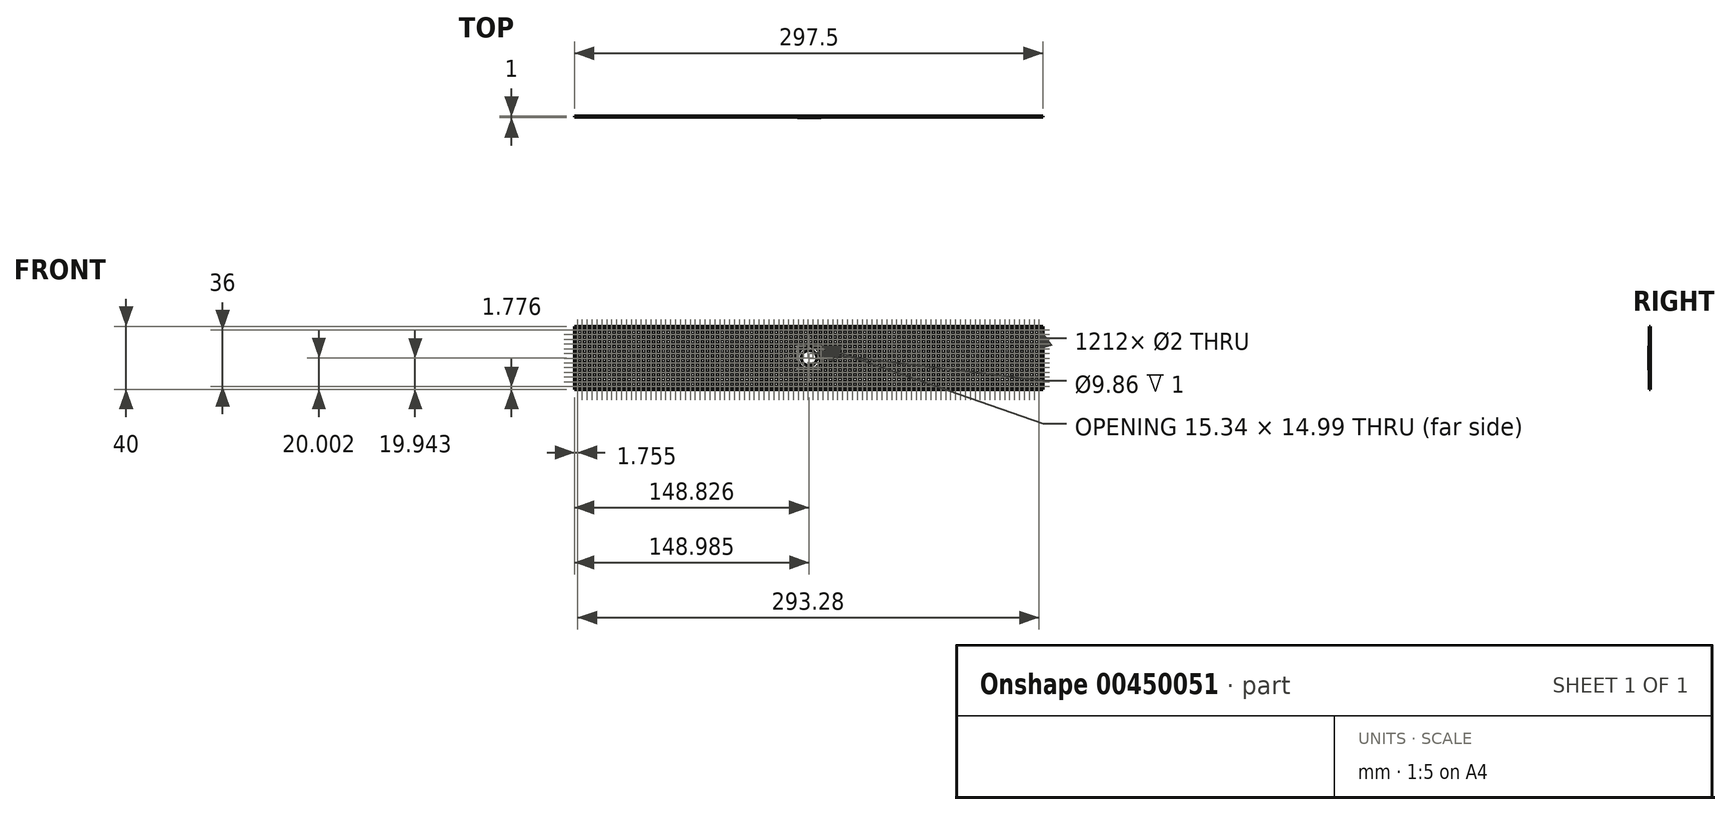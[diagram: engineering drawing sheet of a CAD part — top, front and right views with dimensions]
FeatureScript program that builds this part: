
annotation { "Feature Type Name" : "Feature", "Feature Type Description" : "" }
export const myFeature = defineFeature(function(context is Context, id is Id, definition is map)
    precondition{}
    {
        {
            var Q0;
            Q0=qCreatedBy(makeId("Front.planeOp"),FACE);
            var sketch = newSketch(context, id + "F0", { "sketchPlane" : qUnion([Q0])});
            skLineSegment(sketch, "E0.bottom", {"start": v(-95.63, 31.24) * mm, "end": v(201.87, 31.24) * mm});
            skLineSegment(sketch, "E0.top", {"start": v(-95.63, -8.76) * mm, "end": v(201.87, -8.76) * mm});
            skLineSegment(sketch, "E0.left", {"start": v(-95.63, 31.24) * mm, "end": v(-95.63, -8.76) * mm});
            skLineSegment(sketch, "E0.right", {"start": v(201.87, 31.24) * mm, "end": v(201.87, -8.76) * mm});
            skCircle(sketch, "E1", {"center": v(-93.87, -6.98) * mm, "radius": 1 * mm});
            skCircle(sketch, "E2.0.1.0", {"center": v(-93.87, -3.98) * mm, "radius": 1 * mm});
            skCircle(sketch, "E2.0.2.0", {"center": v(-93.87, -0.98) * mm, "radius": 1 * mm});
            skCircle(sketch, "E2.0.3.0", {"center": v(-93.87, 2.02) * mm, "radius": 1 * mm});
            skCircle(sketch, "E2.0.4.0", {"center": v(-93.87, 5.02) * mm, "radius": 1 * mm});
            skCircle(sketch, "E2.0.5.0", {"center": v(-93.87, 8.02) * mm, "radius": 1 * mm});
            skCircle(sketch, "E2.0.6.0", {"center": v(-93.87, 11.02) * mm, "radius": 1 * mm});
            skCircle(sketch, "E2.0.7.0", {"center": v(-93.87, 14.02) * mm, "radius": 1 * mm});
            skCircle(sketch, "E2.0.8.0", {"center": v(-93.87, 17.02) * mm, "radius": 1 * mm});
            skCircle(sketch, "E2.0.9.0", {"center": v(-93.87, 20.02) * mm, "radius": 1 * mm});
            skCircle(sketch, "E2.0.10.0", {"center": v(-93.87, 23.02) * mm, "radius": 1 * mm});
            skCircle(sketch, "E2.0.11.0", {"center": v(-93.87, 26.02) * mm, "radius": 1 * mm});
            skCircle(sketch, "E2.1.0.0", {"center": v(-90.75, -6.98) * mm, "radius": 1 * mm});
            skCircle(sketch, "E2.1.1.0", {"center": v(-90.75, -3.98) * mm, "radius": 1 * mm});
            skCircle(sketch, "E2.1.2.0", {"center": v(-90.75, -0.98) * mm, "radius": 1 * mm});
            skCircle(sketch, "E2.1.3.0", {"center": v(-90.75, 2.02) * mm, "radius": 1 * mm});
            skCircle(sketch, "E2.1.4.0", {"center": v(-90.75, 5.02) * mm, "radius": 1 * mm});
            skCircle(sketch, "E2.1.5.0", {"center": v(-90.75, 8.02) * mm, "radius": 1 * mm});
            skCircle(sketch, "E2.1.6.0", {"center": v(-90.75, 11.02) * mm, "radius": 1 * mm});
            skCircle(sketch, "E2.1.7.0", {"center": v(-90.75, 14.02) * mm, "radius": 1 * mm});
            skCircle(sketch, "E2.1.8.0", {"center": v(-90.75, 17.02) * mm, "radius": 1 * mm});
            skCircle(sketch, "E2.1.9.0", {"center": v(-90.75, 20.02) * mm, "radius": 1 * mm});
            skCircle(sketch, "E2.1.10.0", {"center": v(-90.75, 23.02) * mm, "radius": 1 * mm});
            skCircle(sketch, "E2.1.11.0", {"center": v(-90.75, 26.02) * mm, "radius": 1 * mm});
            skCircle(sketch, "E2.2.0.0", {"center": v(-87.63, -6.98) * mm, "radius": 1 * mm});
            skCircle(sketch, "E2.2.1.0", {"center": v(-87.63, -3.98) * mm, "radius": 1 * mm});
            skCircle(sketch, "E2.2.2.0", {"center": v(-87.63, -0.98) * mm, "radius": 1 * mm});
            skCircle(sketch, "E2.2.3.0", {"center": v(-87.63, 2.02) * mm, "radius": 1 * mm});
            skCircle(sketch, "E2.2.4.0", {"center": v(-87.63, 5.02) * mm, "radius": 1 * mm});
            skCircle(sketch, "E2.2.5.0", {"center": v(-87.63, 8.02) * mm, "radius": 1 * mm});
            skCircle(sketch, "E2.2.6.0", {"center": v(-87.63, 11.02) * mm, "radius": 1 * mm});
            skCircle(sketch, "E2.2.7.0", {"center": v(-87.63, 14.02) * mm, "radius": 1 * mm});
            skCircle(sketch, "E2.2.8.0", {"center": v(-87.63, 17.02) * mm, "radius": 1 * mm});
            skCircle(sketch, "E2.2.9.0", {"center": v(-87.63, 20.02) * mm, "radius": 1 * mm});
            skCircle(sketch, "E2.2.10.0", {"center": v(-87.63, 23.02) * mm, "radius": 1 * mm});
            skCircle(sketch, "E2.2.11.0", {"center": v(-87.63, 26.02) * mm, "radius": 1 * mm});
            skCircle(sketch, "E2.3.0.0", {"center": v(-84.51, -6.98) * mm, "radius": 1 * mm});
            skCircle(sketch, "E2.3.1.0", {"center": v(-84.51, -3.98) * mm, "radius": 1 * mm});
            skCircle(sketch, "E2.3.2.0", {"center": v(-84.51, -0.98) * mm, "radius": 1 * mm});
            skCircle(sketch, "E2.3.3.0", {"center": v(-84.51, 2.02) * mm, "radius": 1 * mm});
            skCircle(sketch, "E2.3.4.0", {"center": v(-84.51, 5.02) * mm, "radius": 1 * mm});
            skCircle(sketch, "E2.3.5.0", {"center": v(-84.51, 8.02) * mm, "radius": 1 * mm});
            skCircle(sketch, "E2.3.6.0", {"center": v(-84.51, 11.02) * mm, "radius": 1 * mm});
            skCircle(sketch, "E2.3.7.0", {"center": v(-84.51, 14.02) * mm, "radius": 1 * mm});
            skCircle(sketch, "E2.3.8.0", {"center": v(-84.51, 17.02) * mm, "radius": 1 * mm});
            skCircle(sketch, "E2.3.9.0", {"center": v(-84.51, 20.02) * mm, "radius": 1 * mm});
            skCircle(sketch, "E2.3.10.0", {"center": v(-84.51, 23.02) * mm, "radius": 1 * mm});
            skCircle(sketch, "E2.3.11.0", {"center": v(-84.51, 26.02) * mm, "radius": 1 * mm});
            skCircle(sketch, "E2.4.0.0", {"center": v(-81.4, -6.98) * mm, "radius": 1 * mm});
            skCircle(sketch, "E2.4.1.0", {"center": v(-81.4, -3.98) * mm, "radius": 1 * mm});
            skCircle(sketch, "E2.4.2.0", {"center": v(-81.4, -0.98) * mm, "radius": 1 * mm});
            skCircle(sketch, "E2.4.3.0", {"center": v(-81.4, 2.02) * mm, "radius": 1 * mm});
            skCircle(sketch, "E2.4.4.0", {"center": v(-81.4, 5.02) * mm, "radius": 1 * mm});
            skCircle(sketch, "E2.4.5.0", {"center": v(-81.4, 8.02) * mm, "radius": 1 * mm});
            skCircle(sketch, "E2.4.6.0", {"center": v(-81.4, 11.02) * mm, "radius": 1 * mm});
            skCircle(sketch, "E2.4.7.0", {"center": v(-81.4, 14.02) * mm, "radius": 1 * mm});
            skCircle(sketch, "E2.4.8.0", {"center": v(-81.4, 17.02) * mm, "radius": 1 * mm});
            skCircle(sketch, "E2.4.9.0", {"center": v(-81.4, 20.02) * mm, "radius": 1 * mm});
            skCircle(sketch, "E2.4.10.0", {"center": v(-81.4, 23.02) * mm, "radius": 1 * mm});
            skCircle(sketch, "E2.4.11.0", {"center": v(-81.4, 26.02) * mm, "radius": 1 * mm});
            skCircle(sketch, "E2.5.0.0", {"center": v(-78.27, -6.98) * mm, "radius": 1 * mm});
            skCircle(sketch, "E2.5.1.0", {"center": v(-78.27, -3.98) * mm, "radius": 1 * mm});
            skCircle(sketch, "E2.5.2.0", {"center": v(-78.27, -0.98) * mm, "radius": 1 * mm});
            skCircle(sketch, "E2.5.3.0", {"center": v(-78.27, 2.02) * mm, "radius": 1 * mm});
            skCircle(sketch, "E2.5.4.0", {"center": v(-78.27, 5.02) * mm, "radius": 1 * mm});
            skCircle(sketch, "E2.5.5.0", {"center": v(-78.27, 8.02) * mm, "radius": 1 * mm});
            skCircle(sketch, "E2.5.6.0", {"center": v(-78.27, 11.02) * mm, "radius": 1 * mm});
            skCircle(sketch, "E2.5.7.0", {"center": v(-78.27, 14.02) * mm, "radius": 1 * mm});
            skCircle(sketch, "E2.5.8.0", {"center": v(-78.27, 17.02) * mm, "radius": 1 * mm});
            skCircle(sketch, "E2.5.9.0", {"center": v(-78.27, 20.02) * mm, "radius": 1 * mm});
            skCircle(sketch, "E2.5.10.0", {"center": v(-78.27, 23.02) * mm, "radius": 1 * mm});
            skCircle(sketch, "E2.5.11.0", {"center": v(-78.27, 26.02) * mm, "radius": 1 * mm});
            skCircle(sketch, "E2.6.0.0", {"center": v(-75.15, -6.98) * mm, "radius": 1 * mm});
            skCircle(sketch, "E2.6.1.0", {"center": v(-75.15, -3.98) * mm, "radius": 1 * mm});
            skCircle(sketch, "E2.6.2.0", {"center": v(-75.15, -0.98) * mm, "radius": 1 * mm});
            skCircle(sketch, "E2.6.3.0", {"center": v(-75.15, 2.02) * mm, "radius": 1 * mm});
            skCircle(sketch, "E2.6.4.0", {"center": v(-75.15, 5.02) * mm, "radius": 1 * mm});
            skCircle(sketch, "E2.6.5.0", {"center": v(-75.15, 8.02) * mm, "radius": 1 * mm});
            skCircle(sketch, "E2.6.6.0", {"center": v(-75.15, 11.02) * mm, "radius": 1 * mm});
            skCircle(sketch, "E2.6.7.0", {"center": v(-75.15, 14.02) * mm, "radius": 1 * mm});
            skCircle(sketch, "E2.6.8.0", {"center": v(-75.15, 17.02) * mm, "radius": 1 * mm});
            skCircle(sketch, "E2.6.9.0", {"center": v(-75.15, 20.02) * mm, "radius": 1 * mm});
            skCircle(sketch, "E2.6.10.0", {"center": v(-75.15, 23.02) * mm, "radius": 1 * mm});
            skCircle(sketch, "E2.6.11.0", {"center": v(-75.15, 26.02) * mm, "radius": 1 * mm});
            skCircle(sketch, "E2.7.0.0", {"center": v(-72.03, -6.98) * mm, "radius": 1 * mm});
            skCircle(sketch, "E2.7.1.0", {"center": v(-72.03, -3.98) * mm, "radius": 1 * mm});
            skCircle(sketch, "E2.7.2.0", {"center": v(-72.03, -0.98) * mm, "radius": 1 * mm});
            skCircle(sketch, "E2.7.3.0", {"center": v(-72.03, 2.02) * mm, "radius": 1 * mm});
            skCircle(sketch, "E2.7.4.0", {"center": v(-72.03, 5.02) * mm, "radius": 1 * mm});
            skCircle(sketch, "E2.7.5.0", {"center": v(-72.03, 8.02) * mm, "radius": 1 * mm});
            skCircle(sketch, "E2.7.6.0", {"center": v(-72.03, 11.02) * mm, "radius": 1 * mm});
            skCircle(sketch, "E2.7.7.0", {"center": v(-72.03, 14.02) * mm, "radius": 1 * mm});
            skCircle(sketch, "E2.7.8.0", {"center": v(-72.03, 17.02) * mm, "radius": 1 * mm});
            skCircle(sketch, "E2.7.9.0", {"center": v(-72.03, 20.02) * mm, "radius": 1 * mm});
            skCircle(sketch, "E2.7.10.0", {"center": v(-72.03, 23.02) * mm, "radius": 1 * mm});
            skCircle(sketch, "E2.7.11.0", {"center": v(-72.03, 26.02) * mm, "radius": 1 * mm});
            skCircle(sketch, "E2.8.0.0", {"center": v(-68.91, -6.98) * mm, "radius": 1 * mm});
            skCircle(sketch, "E2.8.1.0", {"center": v(-68.91, -3.98) * mm, "radius": 1 * mm});
            skCircle(sketch, "E2.8.2.0", {"center": v(-68.91, -0.98) * mm, "radius": 1 * mm});
            skCircle(sketch, "E2.8.3.0", {"center": v(-68.91, 2.02) * mm, "radius": 1 * mm});
            skCircle(sketch, "E2.8.4.0", {"center": v(-68.91, 5.02) * mm, "radius": 1 * mm});
            skCircle(sketch, "E2.8.5.0", {"center": v(-68.91, 8.02) * mm, "radius": 1 * mm});
            skCircle(sketch, "E2.8.6.0", {"center": v(-68.91, 11.02) * mm, "radius": 1 * mm});
            skCircle(sketch, "E2.8.7.0", {"center": v(-68.91, 14.02) * mm, "radius": 1 * mm});
            skCircle(sketch, "E2.8.8.0", {"center": v(-68.91, 17.02) * mm, "radius": 1 * mm});
            skCircle(sketch, "E2.8.9.0", {"center": v(-68.91, 20.02) * mm, "radius": 1 * mm});
            skCircle(sketch, "E2.8.10.0", {"center": v(-68.91, 23.02) * mm, "radius": 1 * mm});
            skCircle(sketch, "E2.8.11.0", {"center": v(-68.91, 26.02) * mm, "radius": 1 * mm});
            skCircle(sketch, "E2.9.0.0", {"center": v(-65.8, -6.98) * mm, "radius": 1 * mm});
            skCircle(sketch, "E2.9.1.0", {"center": v(-65.8, -3.98) * mm, "radius": 1 * mm});
            skCircle(sketch, "E2.9.2.0", {"center": v(-65.8, -0.98) * mm, "radius": 1 * mm});
            skCircle(sketch, "E2.9.3.0", {"center": v(-65.8, 2.02) * mm, "radius": 1 * mm});
            skCircle(sketch, "E2.9.4.0", {"center": v(-65.8, 5.02) * mm, "radius": 1 * mm});
            skCircle(sketch, "E2.9.5.0", {"center": v(-65.8, 8.02) * mm, "radius": 1 * mm});
            skCircle(sketch, "E2.9.6.0", {"center": v(-65.8, 11.02) * mm, "radius": 1 * mm});
            skCircle(sketch, "E2.9.7.0", {"center": v(-65.8, 14.02) * mm, "radius": 1 * mm});
            skCircle(sketch, "E2.9.8.0", {"center": v(-65.8, 17.02) * mm, "radius": 1 * mm});
            skCircle(sketch, "E2.9.9.0", {"center": v(-65.8, 20.02) * mm, "radius": 1 * mm});
            skCircle(sketch, "E2.9.10.0", {"center": v(-65.8, 23.02) * mm, "radius": 1 * mm});
            skCircle(sketch, "E2.9.11.0", {"center": v(-65.8, 26.02) * mm, "radius": 1 * mm});
            skCircle(sketch, "E2.10.0.0", {"center": v(-62.67, -6.98) * mm, "radius": 1 * mm});
            skCircle(sketch, "E2.10.1.0", {"center": v(-62.67, -3.98) * mm, "radius": 1 * mm});
            skCircle(sketch, "E2.10.2.0", {"center": v(-62.67, -0.98) * mm, "radius": 1 * mm});
            skCircle(sketch, "E2.10.3.0", {"center": v(-62.67, 2.02) * mm, "radius": 1 * mm});
            skCircle(sketch, "E2.10.4.0", {"center": v(-62.67, 5.02) * mm, "radius": 1 * mm});
            skCircle(sketch, "E2.10.5.0", {"center": v(-62.67, 8.02) * mm, "radius": 1 * mm});
            skCircle(sketch, "E2.10.6.0", {"center": v(-62.67, 11.02) * mm, "radius": 1 * mm});
            skCircle(sketch, "E2.10.7.0", {"center": v(-62.67, 14.02) * mm, "radius": 1 * mm});
            skCircle(sketch, "E2.10.8.0", {"center": v(-62.67, 17.02) * mm, "radius": 1 * mm});
            skCircle(sketch, "E2.10.9.0", {"center": v(-62.67, 20.02) * mm, "radius": 1 * mm});
            skCircle(sketch, "E2.10.10.0", {"center": v(-62.67, 23.02) * mm, "radius": 1 * mm});
            skCircle(sketch, "E2.10.11.0", {"center": v(-62.67, 26.02) * mm, "radius": 1 * mm});
            skCircle(sketch, "E2.11.0.0", {"center": v(-59.55, -6.98) * mm, "radius": 1 * mm});
            skCircle(sketch, "E2.11.1.0", {"center": v(-59.55, -3.98) * mm, "radius": 1 * mm});
            skCircle(sketch, "E2.11.2.0", {"center": v(-59.55, -0.98) * mm, "radius": 1 * mm});
            skCircle(sketch, "E2.11.3.0", {"center": v(-59.55, 2.02) * mm, "radius": 1 * mm});
            skCircle(sketch, "E2.11.4.0", {"center": v(-59.55, 5.02) * mm, "radius": 1 * mm});
            skCircle(sketch, "E2.11.5.0", {"center": v(-59.55, 8.02) * mm, "radius": 1 * mm});
            skCircle(sketch, "E2.11.6.0", {"center": v(-59.55, 11.02) * mm, "radius": 1 * mm});
            skCircle(sketch, "E2.11.7.0", {"center": v(-59.55, 14.02) * mm, "radius": 1 * mm});
            skCircle(sketch, "E2.11.8.0", {"center": v(-59.55, 17.02) * mm, "radius": 1 * mm});
            skCircle(sketch, "E2.11.9.0", {"center": v(-59.55, 20.02) * mm, "radius": 1 * mm});
            skCircle(sketch, "E2.11.10.0", {"center": v(-59.55, 23.02) * mm, "radius": 1 * mm});
            skCircle(sketch, "E2.11.11.0", {"center": v(-59.55, 26.02) * mm, "radius": 1 * mm});
            skCircle(sketch, "E2.12.0.0", {"center": v(-56.43, -6.98) * mm, "radius": 1 * mm});
            skCircle(sketch, "E2.12.1.0", {"center": v(-56.43, -3.98) * mm, "radius": 1 * mm});
            skCircle(sketch, "E2.12.2.0", {"center": v(-56.43, -0.98) * mm, "radius": 1 * mm});
            skCircle(sketch, "E2.12.3.0", {"center": v(-56.43, 2.02) * mm, "radius": 1 * mm});
            skCircle(sketch, "E2.12.4.0", {"center": v(-56.43, 5.02) * mm, "radius": 1 * mm});
            skCircle(sketch, "E2.12.5.0", {"center": v(-56.43, 8.02) * mm, "radius": 1 * mm});
            skCircle(sketch, "E2.12.6.0", {"center": v(-56.43, 11.02) * mm, "radius": 1 * mm});
            skCircle(sketch, "E2.12.7.0", {"center": v(-56.43, 14.02) * mm, "radius": 1 * mm});
            skCircle(sketch, "E2.12.8.0", {"center": v(-56.43, 17.02) * mm, "radius": 1 * mm});
            skCircle(sketch, "E2.12.9.0", {"center": v(-56.43, 20.02) * mm, "radius": 1 * mm});
            skCircle(sketch, "E2.12.10.0", {"center": v(-56.43, 23.02) * mm, "radius": 1 * mm});
            skCircle(sketch, "E2.12.11.0", {"center": v(-56.43, 26.02) * mm, "radius": 1 * mm});
            skCircle(sketch, "E2.13.0.0", {"center": v(-53.31, -6.98) * mm, "radius": 1 * mm});
            skCircle(sketch, "E2.13.1.0", {"center": v(-53.31, -3.98) * mm, "radius": 1 * mm});
            skCircle(sketch, "E2.13.2.0", {"center": v(-53.31, -0.98) * mm, "radius": 1 * mm});
            skCircle(sketch, "E2.13.3.0", {"center": v(-53.31, 2.02) * mm, "radius": 1 * mm});
            skCircle(sketch, "E2.13.4.0", {"center": v(-53.31, 5.02) * mm, "radius": 1 * mm});
            skCircle(sketch, "E2.13.5.0", {"center": v(-53.31, 8.02) * mm, "radius": 1 * mm});
            skCircle(sketch, "E2.13.6.0", {"center": v(-53.31, 11.02) * mm, "radius": 1 * mm});
            skCircle(sketch, "E2.13.7.0", {"center": v(-53.31, 14.02) * mm, "radius": 1 * mm});
            skCircle(sketch, "E2.13.8.0", {"center": v(-53.31, 17.02) * mm, "radius": 1 * mm});
            skCircle(sketch, "E2.13.9.0", {"center": v(-53.31, 20.02) * mm, "radius": 1 * mm});
            skCircle(sketch, "E2.13.10.0", {"center": v(-53.31, 23.02) * mm, "radius": 1 * mm});
            skCircle(sketch, "E2.13.11.0", {"center": v(-53.31, 26.02) * mm, "radius": 1 * mm});
            skCircle(sketch, "E2.14.0.0", {"center": v(-50.2, -6.98) * mm, "radius": 1 * mm});
            skCircle(sketch, "E2.14.1.0", {"center": v(-50.2, -3.98) * mm, "radius": 1 * mm});
            skCircle(sketch, "E2.14.2.0", {"center": v(-50.2, -0.98) * mm, "radius": 1 * mm});
            skCircle(sketch, "E2.14.3.0", {"center": v(-50.2, 2.02) * mm, "radius": 1 * mm});
            skCircle(sketch, "E2.14.4.0", {"center": v(-50.2, 5.02) * mm, "radius": 1 * mm});
            skCircle(sketch, "E2.14.5.0", {"center": v(-50.2, 8.02) * mm, "radius": 1 * mm});
            skCircle(sketch, "E2.14.6.0", {"center": v(-50.2, 11.02) * mm, "radius": 1 * mm});
            skCircle(sketch, "E2.14.7.0", {"center": v(-50.2, 14.02) * mm, "radius": 1 * mm});
            skCircle(sketch, "E2.14.8.0", {"center": v(-50.2, 17.02) * mm, "radius": 1 * mm});
            skCircle(sketch, "E2.14.9.0", {"center": v(-50.2, 20.02) * mm, "radius": 1 * mm});
            skCircle(sketch, "E2.14.10.0", {"center": v(-50.2, 23.02) * mm, "radius": 1 * mm});
            skCircle(sketch, "E2.14.11.0", {"center": v(-50.2, 26.02) * mm, "radius": 1 * mm});
            skCircle(sketch, "E2.15.0.0", {"center": v(-47.07, -6.98) * mm, "radius": 1 * mm});
            skCircle(sketch, "E2.15.1.0", {"center": v(-47.07, -3.98) * mm, "radius": 1 * mm});
            skCircle(sketch, "E2.15.2.0", {"center": v(-47.07, -0.98) * mm, "radius": 1 * mm});
            skCircle(sketch, "E2.15.3.0", {"center": v(-47.07, 2.02) * mm, "radius": 1 * mm});
            skCircle(sketch, "E2.15.4.0", {"center": v(-47.07, 5.02) * mm, "radius": 1 * mm});
            skCircle(sketch, "E2.15.5.0", {"center": v(-47.07, 8.02) * mm, "radius": 1 * mm});
            skCircle(sketch, "E2.15.6.0", {"center": v(-47.07, 11.02) * mm, "radius": 1 * mm});
            skCircle(sketch, "E2.15.7.0", {"center": v(-47.07, 14.02) * mm, "radius": 1 * mm});
            skCircle(sketch, "E2.15.8.0", {"center": v(-47.07, 17.02) * mm, "radius": 1 * mm});
            skCircle(sketch, "E2.15.9.0", {"center": v(-47.07, 20.02) * mm, "radius": 1 * mm});
            skCircle(sketch, "E2.15.10.0", {"center": v(-47.07, 23.02) * mm, "radius": 1 * mm});
            skCircle(sketch, "E2.15.11.0", {"center": v(-47.07, 26.02) * mm, "radius": 1 * mm});
            skCircle(sketch, "E2.16.0.0", {"center": v(-43.95, -6.98) * mm, "radius": 1 * mm});
            skCircle(sketch, "E2.16.1.0", {"center": v(-43.95, -3.98) * mm, "radius": 1 * mm});
            skCircle(sketch, "E2.16.2.0", {"center": v(-43.95, -0.98) * mm, "radius": 1 * mm});
            skCircle(sketch, "E2.16.3.0", {"center": v(-43.95, 2.02) * mm, "radius": 1 * mm});
            skCircle(sketch, "E2.16.4.0", {"center": v(-43.95, 5.02) * mm, "radius": 1 * mm});
            skCircle(sketch, "E2.16.5.0", {"center": v(-43.95, 8.02) * mm, "radius": 1 * mm});
            skCircle(sketch, "E2.16.6.0", {"center": v(-43.95, 11.02) * mm, "radius": 1 * mm});
            skCircle(sketch, "E2.16.7.0", {"center": v(-43.95, 14.02) * mm, "radius": 1 * mm});
            skCircle(sketch, "E2.16.8.0", {"center": v(-43.95, 17.02) * mm, "radius": 1 * mm});
            skCircle(sketch, "E2.16.9.0", {"center": v(-43.95, 20.02) * mm, "radius": 1 * mm});
            skCircle(sketch, "E2.16.10.0", {"center": v(-43.95, 23.02) * mm, "radius": 1 * mm});
            skCircle(sketch, "E2.16.11.0", {"center": v(-43.95, 26.02) * mm, "radius": 1 * mm});
            skCircle(sketch, "E2.17.0.0", {"center": v(-40.83, -6.98) * mm, "radius": 1 * mm});
            skCircle(sketch, "E2.17.1.0", {"center": v(-40.83, -3.98) * mm, "radius": 1 * mm});
            skCircle(sketch, "E2.17.2.0", {"center": v(-40.83, -0.98) * mm, "radius": 1 * mm});
            skCircle(sketch, "E2.17.3.0", {"center": v(-40.83, 2.02) * mm, "radius": 1 * mm});
            skCircle(sketch, "E2.17.4.0", {"center": v(-40.83, 5.02) * mm, "radius": 1 * mm});
            skCircle(sketch, "E2.17.5.0", {"center": v(-40.83, 8.02) * mm, "radius": 1 * mm});
            skCircle(sketch, "E2.17.6.0", {"center": v(-40.83, 11.02) * mm, "radius": 1 * mm});
            skCircle(sketch, "E2.17.7.0", {"center": v(-40.83, 14.02) * mm, "radius": 1 * mm});
            skCircle(sketch, "E2.17.8.0", {"center": v(-40.83, 17.02) * mm, "radius": 1 * mm});
            skCircle(sketch, "E2.17.9.0", {"center": v(-40.83, 20.02) * mm, "radius": 1 * mm});
            skCircle(sketch, "E2.17.10.0", {"center": v(-40.83, 23.02) * mm, "radius": 1 * mm});
            skCircle(sketch, "E2.17.11.0", {"center": v(-40.83, 26.02) * mm, "radius": 1 * mm});
            skCircle(sketch, "E2.18.0.0", {"center": v(-37.71, -6.98) * mm, "radius": 1 * mm});
            skCircle(sketch, "E2.18.1.0", {"center": v(-37.71, -3.98) * mm, "radius": 1 * mm});
            skCircle(sketch, "E2.18.2.0", {"center": v(-37.71, -0.98) * mm, "radius": 1 * mm});
            skCircle(sketch, "E2.18.3.0", {"center": v(-37.71, 2.02) * mm, "radius": 1 * mm});
            skCircle(sketch, "E2.18.4.0", {"center": v(-37.71, 5.02) * mm, "radius": 1 * mm});
            skCircle(sketch, "E2.18.5.0", {"center": v(-37.71, 8.02) * mm, "radius": 1 * mm});
            skCircle(sketch, "E2.18.6.0", {"center": v(-37.71, 11.02) * mm, "radius": 1 * mm});
            skCircle(sketch, "E2.18.7.0", {"center": v(-37.71, 14.02) * mm, "radius": 1 * mm});
            skCircle(sketch, "E2.18.8.0", {"center": v(-37.71, 17.02) * mm, "radius": 1 * mm});
            skCircle(sketch, "E2.18.9.0", {"center": v(-37.71, 20.02) * mm, "radius": 1 * mm});
            skCircle(sketch, "E2.18.10.0", {"center": v(-37.71, 23.02) * mm, "radius": 1 * mm});
            skCircle(sketch, "E2.18.11.0", {"center": v(-37.71, 26.02) * mm, "radius": 1 * mm});
            skCircle(sketch, "E2.19.0.0", {"center": v(-34.6, -6.98) * mm, "radius": 1 * mm});
            skCircle(sketch, "E2.19.1.0", {"center": v(-34.6, -3.98) * mm, "radius": 1 * mm});
            skCircle(sketch, "E2.19.2.0", {"center": v(-34.6, -0.98) * mm, "radius": 1 * mm});
            skCircle(sketch, "E2.19.3.0", {"center": v(-34.6, 2.02) * mm, "radius": 1 * mm});
            skCircle(sketch, "E2.19.4.0", {"center": v(-34.6, 5.02) * mm, "radius": 1 * mm});
            skCircle(sketch, "E2.19.5.0", {"center": v(-34.6, 8.02) * mm, "radius": 1 * mm});
            skCircle(sketch, "E2.19.6.0", {"center": v(-34.6, 11.02) * mm, "radius": 1 * mm});
            skCircle(sketch, "E2.19.7.0", {"center": v(-34.6, 14.02) * mm, "radius": 1 * mm});
            skCircle(sketch, "E2.19.8.0", {"center": v(-34.6, 17.02) * mm, "radius": 1 * mm});
            skCircle(sketch, "E2.19.9.0", {"center": v(-34.6, 20.02) * mm, "radius": 1 * mm});
            skCircle(sketch, "E2.19.10.0", {"center": v(-34.6, 23.02) * mm, "radius": 1 * mm});
            skCircle(sketch, "E2.19.11.0", {"center": v(-34.6, 26.02) * mm, "radius": 1 * mm});
            skCircle(sketch, "E2.20.0.0", {"center": v(-31.47, -6.98) * mm, "radius": 1 * mm});
            skCircle(sketch, "E2.20.1.0", {"center": v(-31.47, -3.98) * mm, "radius": 1 * mm});
            skCircle(sketch, "E2.20.2.0", {"center": v(-31.47, -0.98) * mm, "radius": 1 * mm});
            skCircle(sketch, "E2.20.3.0", {"center": v(-31.47, 2.02) * mm, "radius": 1 * mm});
            skCircle(sketch, "E2.20.4.0", {"center": v(-31.47, 5.02) * mm, "radius": 1 * mm});
            skCircle(sketch, "E2.20.5.0", {"center": v(-31.47, 8.02) * mm, "radius": 1 * mm});
            skCircle(sketch, "E2.20.6.0", {"center": v(-31.47, 11.02) * mm, "radius": 1 * mm});
            skCircle(sketch, "E2.20.7.0", {"center": v(-31.47, 14.02) * mm, "radius": 1 * mm});
            skCircle(sketch, "E2.20.8.0", {"center": v(-31.47, 17.02) * mm, "radius": 1 * mm});
            skCircle(sketch, "E2.20.9.0", {"center": v(-31.47, 20.02) * mm, "radius": 1 * mm});
            skCircle(sketch, "E2.20.10.0", {"center": v(-31.47, 23.02) * mm, "radius": 1 * mm});
            skCircle(sketch, "E2.20.11.0", {"center": v(-31.47, 26.02) * mm, "radius": 1 * mm});
            skCircle(sketch, "E2.21.0.0", {"center": v(-28.35, -6.98) * mm, "radius": 1 * mm});
            skCircle(sketch, "E2.21.1.0", {"center": v(-28.35, -3.98) * mm, "radius": 1 * mm});
            skCircle(sketch, "E2.21.2.0", {"center": v(-28.35, -0.98) * mm, "radius": 1 * mm});
            skCircle(sketch, "E2.21.3.0", {"center": v(-28.35, 2.02) * mm, "radius": 1 * mm});
            skCircle(sketch, "E2.21.4.0", {"center": v(-28.35, 5.02) * mm, "radius": 1 * mm});
            skCircle(sketch, "E2.21.5.0", {"center": v(-28.35, 8.02) * mm, "radius": 1 * mm});
            skCircle(sketch, "E2.21.6.0", {"center": v(-28.35, 11.02) * mm, "radius": 1 * mm});
            skCircle(sketch, "E2.21.7.0", {"center": v(-28.35, 14.02) * mm, "radius": 1 * mm});
            skCircle(sketch, "E2.21.8.0", {"center": v(-28.35, 17.02) * mm, "radius": 1 * mm});
            skCircle(sketch, "E2.21.9.0", {"center": v(-28.35, 20.02) * mm, "radius": 1 * mm});
            skCircle(sketch, "E2.21.10.0", {"center": v(-28.35, 23.02) * mm, "radius": 1 * mm});
            skCircle(sketch, "E2.21.11.0", {"center": v(-28.35, 26.02) * mm, "radius": 1 * mm});
            skCircle(sketch, "E2.22.0.0", {"center": v(-25.23, -6.98) * mm, "radius": 1 * mm});
            skCircle(sketch, "E2.22.1.0", {"center": v(-25.23, -3.98) * mm, "radius": 1 * mm});
            skCircle(sketch, "E2.22.2.0", {"center": v(-25.23, -0.98) * mm, "radius": 1 * mm});
            skCircle(sketch, "E2.22.3.0", {"center": v(-25.23, 2.02) * mm, "radius": 1 * mm});
            skCircle(sketch, "E2.22.4.0", {"center": v(-25.23, 5.02) * mm, "radius": 1 * mm});
            skCircle(sketch, "E2.22.5.0", {"center": v(-25.23, 8.02) * mm, "radius": 1 * mm});
            skCircle(sketch, "E2.22.6.0", {"center": v(-25.23, 11.02) * mm, "radius": 1 * mm});
            skCircle(sketch, "E2.22.7.0", {"center": v(-25.23, 14.02) * mm, "radius": 1 * mm});
            skCircle(sketch, "E2.22.8.0", {"center": v(-25.23, 17.02) * mm, "radius": 1 * mm});
            skCircle(sketch, "E2.22.9.0", {"center": v(-25.23, 20.02) * mm, "radius": 1 * mm});
            skCircle(sketch, "E2.22.10.0", {"center": v(-25.23, 23.02) * mm, "radius": 1 * mm});
            skCircle(sketch, "E2.22.11.0", {"center": v(-25.23, 26.02) * mm, "radius": 1 * mm});
            skCircle(sketch, "E2.23.0.0", {"center": v(-22.11, -6.98) * mm, "radius": 1 * mm});
            skCircle(sketch, "E2.23.1.0", {"center": v(-22.11, -3.98) * mm, "radius": 1 * mm});
            skCircle(sketch, "E2.23.2.0", {"center": v(-22.11, -0.98) * mm, "radius": 1 * mm});
            skCircle(sketch, "E2.23.3.0", {"center": v(-22.11, 2.02) * mm, "radius": 1 * mm});
            skCircle(sketch, "E2.23.4.0", {"center": v(-22.11, 5.02) * mm, "radius": 1 * mm});
            skCircle(sketch, "E2.23.5.0", {"center": v(-22.11, 8.02) * mm, "radius": 1 * mm});
            skCircle(sketch, "E2.23.6.0", {"center": v(-22.11, 11.02) * mm, "radius": 1 * mm});
            skCircle(sketch, "E2.23.7.0", {"center": v(-22.11, 14.02) * mm, "radius": 1 * mm});
            skCircle(sketch, "E2.23.8.0", {"center": v(-22.11, 17.02) * mm, "radius": 1 * mm});
            skCircle(sketch, "E2.23.9.0", {"center": v(-22.11, 20.02) * mm, "radius": 1 * mm});
            skCircle(sketch, "E2.23.10.0", {"center": v(-22.11, 23.02) * mm, "radius": 1 * mm});
            skCircle(sketch, "E2.23.11.0", {"center": v(-22.11, 26.02) * mm, "radius": 1 * mm});
            skCircle(sketch, "E2.24.0.0", {"center": v(-19, -6.98) * mm, "radius": 1 * mm});
            skCircle(sketch, "E2.24.1.0", {"center": v(-19, -3.98) * mm, "radius": 1 * mm});
            skCircle(sketch, "E2.24.2.0", {"center": v(-19, -0.98) * mm, "radius": 1 * mm});
            skCircle(sketch, "E2.24.3.0", {"center": v(-19, 2.02) * mm, "radius": 1 * mm});
            skCircle(sketch, "E2.24.4.0", {"center": v(-19, 5.02) * mm, "radius": 1 * mm});
            skCircle(sketch, "E2.24.5.0", {"center": v(-19, 8.02) * mm, "radius": 1 * mm});
            skCircle(sketch, "E2.24.6.0", {"center": v(-19, 11.02) * mm, "radius": 1 * mm});
            skCircle(sketch, "E2.24.7.0", {"center": v(-19, 14.02) * mm, "radius": 1 * mm});
            skCircle(sketch, "E2.24.8.0", {"center": v(-19, 17.02) * mm, "radius": 1 * mm});
            skCircle(sketch, "E2.24.9.0", {"center": v(-19, 20.02) * mm, "radius": 1 * mm});
            skCircle(sketch, "E2.24.10.0", {"center": v(-19, 23.02) * mm, "radius": 1 * mm});
            skCircle(sketch, "E2.24.11.0", {"center": v(-19, 26.02) * mm, "radius": 1 * mm});
            skCircle(sketch, "E2.25.0.0", {"center": v(-15.87, -6.98) * mm, "radius": 1 * mm});
            skCircle(sketch, "E2.25.1.0", {"center": v(-15.87, -3.98) * mm, "radius": 1 * mm});
            skCircle(sketch, "E2.25.2.0", {"center": v(-15.87, -0.98) * mm, "radius": 1 * mm});
            skCircle(sketch, "E2.25.3.0", {"center": v(-15.87, 2.02) * mm, "radius": 1 * mm});
            skCircle(sketch, "E2.25.4.0", {"center": v(-15.87, 5.02) * mm, "radius": 1 * mm});
            skCircle(sketch, "E2.25.5.0", {"center": v(-15.87, 8.02) * mm, "radius": 1 * mm});
            skCircle(sketch, "E2.25.6.0", {"center": v(-15.87, 11.02) * mm, "radius": 1 * mm});
            skCircle(sketch, "E2.25.7.0", {"center": v(-15.87, 14.02) * mm, "radius": 1 * mm});
            skCircle(sketch, "E2.25.8.0", {"center": v(-15.87, 17.02) * mm, "radius": 1 * mm});
            skCircle(sketch, "E2.25.9.0", {"center": v(-15.87, 20.02) * mm, "radius": 1 * mm});
            skCircle(sketch, "E2.25.10.0", {"center": v(-15.87, 23.02) * mm, "radius": 1 * mm});
            skCircle(sketch, "E2.25.11.0", {"center": v(-15.87, 26.02) * mm, "radius": 1 * mm});
            skCircle(sketch, "E2.26.0.0", {"center": v(-12.75, -6.98) * mm, "radius": 1 * mm});
            skCircle(sketch, "E2.26.1.0", {"center": v(-12.75, -3.98) * mm, "radius": 1 * mm});
            skCircle(sketch, "E2.26.2.0", {"center": v(-12.75, -0.98) * mm, "radius": 1 * mm});
            skCircle(sketch, "E2.26.3.0", {"center": v(-12.75, 2.02) * mm, "radius": 1 * mm});
            skCircle(sketch, "E2.26.4.0", {"center": v(-12.75, 5.02) * mm, "radius": 1 * mm});
            skCircle(sketch, "E2.26.5.0", {"center": v(-12.75, 8.02) * mm, "radius": 1 * mm});
            skCircle(sketch, "E2.26.6.0", {"center": v(-12.75, 11.02) * mm, "radius": 1 * mm});
            skCircle(sketch, "E2.26.7.0", {"center": v(-12.75, 14.02) * mm, "radius": 1 * mm});
            skCircle(sketch, "E2.26.8.0", {"center": v(-12.75, 17.02) * mm, "radius": 1 * mm});
            skCircle(sketch, "E2.26.9.0", {"center": v(-12.75, 20.02) * mm, "radius": 1 * mm});
            skCircle(sketch, "E2.26.10.0", {"center": v(-12.75, 23.02) * mm, "radius": 1 * mm});
            skCircle(sketch, "E2.26.11.0", {"center": v(-12.75, 26.02) * mm, "radius": 1 * mm});
            skCircle(sketch, "E2.27.0.0", {"center": v(-9.63, -6.98) * mm, "radius": 1 * mm});
            skCircle(sketch, "E2.27.1.0", {"center": v(-9.63, -3.98) * mm, "radius": 1 * mm});
            skCircle(sketch, "E2.27.2.0", {"center": v(-9.63, -0.98) * mm, "radius": 1 * mm});
            skCircle(sketch, "E2.27.3.0", {"center": v(-9.63, 2.02) * mm, "radius": 1 * mm});
            skCircle(sketch, "E2.27.4.0", {"center": v(-9.63, 5.02) * mm, "radius": 1 * mm});
            skCircle(sketch, "E2.27.5.0", {"center": v(-9.63, 8.02) * mm, "radius": 1 * mm});
            skCircle(sketch, "E2.27.6.0", {"center": v(-9.63, 11.02) * mm, "radius": 1 * mm});
            skCircle(sketch, "E2.27.7.0", {"center": v(-9.63, 14.02) * mm, "radius": 1 * mm});
            skCircle(sketch, "E2.27.8.0", {"center": v(-9.63, 17.02) * mm, "radius": 1 * mm});
            skCircle(sketch, "E2.27.9.0", {"center": v(-9.63, 20.02) * mm, "radius": 1 * mm});
            skCircle(sketch, "E2.27.10.0", {"center": v(-9.63, 23.02) * mm, "radius": 1 * mm});
            skCircle(sketch, "E2.27.11.0", {"center": v(-9.63, 26.02) * mm, "radius": 1 * mm});
            skCircle(sketch, "E2.28.0.0", {"center": v(-6.51, -6.98) * mm, "radius": 1 * mm});
            skCircle(sketch, "E2.28.1.0", {"center": v(-6.51, -3.98) * mm, "radius": 1 * mm});
            skCircle(sketch, "E2.28.2.0", {"center": v(-6.51, -0.98) * mm, "radius": 1 * mm});
            skCircle(sketch, "E2.28.3.0", {"center": v(-6.51, 2.02) * mm, "radius": 1 * mm});
            skCircle(sketch, "E2.28.4.0", {"center": v(-6.51, 5.02) * mm, "radius": 1 * mm});
            skCircle(sketch, "E2.28.5.0", {"center": v(-6.51, 8.02) * mm, "radius": 1 * mm});
            skCircle(sketch, "E2.28.6.0", {"center": v(-6.51, 11.02) * mm, "radius": 1 * mm});
            skCircle(sketch, "E2.28.7.0", {"center": v(-6.51, 14.02) * mm, "radius": 1 * mm});
            skCircle(sketch, "E2.28.8.0", {"center": v(-6.51, 17.02) * mm, "radius": 1 * mm});
            skCircle(sketch, "E2.28.9.0", {"center": v(-6.51, 20.02) * mm, "radius": 1 * mm});
            skCircle(sketch, "E2.28.10.0", {"center": v(-6.51, 23.02) * mm, "radius": 1 * mm});
            skCircle(sketch, "E2.28.11.0", {"center": v(-6.51, 26.02) * mm, "radius": 1 * mm});
            skCircle(sketch, "E2.29.0.0", {"center": v(-3.4, -6.98) * mm, "radius": 1 * mm});
            skCircle(sketch, "E2.29.1.0", {"center": v(-3.4, -3.98) * mm, "radius": 1 * mm});
            skCircle(sketch, "E2.29.2.0", {"center": v(-3.4, -0.98) * mm, "radius": 1 * mm});
            skCircle(sketch, "E2.29.3.0", {"center": v(-3.4, 2.02) * mm, "radius": 1 * mm});
            skCircle(sketch, "E2.29.4.0", {"center": v(-3.4, 5.02) * mm, "radius": 1 * mm});
            skCircle(sketch, "E2.29.5.0", {"center": v(-3.4, 8.02) * mm, "radius": 1 * mm});
            skCircle(sketch, "E2.29.6.0", {"center": v(-3.4, 11.02) * mm, "radius": 1 * mm});
            skCircle(sketch, "E2.29.7.0", {"center": v(-3.4, 14.02) * mm, "radius": 1 * mm});
            skCircle(sketch, "E2.29.8.0", {"center": v(-3.4, 17.02) * mm, "radius": 1 * mm});
            skCircle(sketch, "E2.29.9.0", {"center": v(-3.4, 20.02) * mm, "radius": 1 * mm});
            skCircle(sketch, "E2.29.10.0", {"center": v(-3.4, 23.02) * mm, "radius": 1 * mm});
            skCircle(sketch, "E2.29.11.0", {"center": v(-3.4, 26.02) * mm, "radius": 1 * mm});
            skCircle(sketch, "E2.30.0.0", {"center": v(-0.27, -6.98) * mm, "radius": 1 * mm});
            skCircle(sketch, "E2.30.1.0", {"center": v(-0.27, -3.98) * mm, "radius": 1 * mm});
            skCircle(sketch, "E2.30.2.0", {"center": v(-0.27, -0.98) * mm, "radius": 1 * mm});
            skCircle(sketch, "E2.30.3.0", {"center": v(-0.27, 2.02) * mm, "radius": 1 * mm});
            skCircle(sketch, "E2.30.4.0", {"center": v(-0.27, 5.02) * mm, "radius": 1 * mm});
            skCircle(sketch, "E2.30.5.0", {"center": v(-0.27, 8.02) * mm, "radius": 1 * mm});
            skCircle(sketch, "E2.30.6.0", {"center": v(-0.27, 11.02) * mm, "radius": 1 * mm});
            skCircle(sketch, "E2.30.7.0", {"center": v(-0.27, 14.02) * mm, "radius": 1 * mm});
            skCircle(sketch, "E2.30.8.0", {"center": v(-0.27, 17.02) * mm, "radius": 1 * mm});
            skCircle(sketch, "E2.30.9.0", {"center": v(-0.27, 20.02) * mm, "radius": 1 * mm});
            skCircle(sketch, "E2.30.10.0", {"center": v(-0.27, 23.02) * mm, "radius": 1 * mm});
            skCircle(sketch, "E2.30.11.0", {"center": v(-0.27, 26.02) * mm, "radius": 1 * mm});
            skCircle(sketch, "E2.31.0.0", {"center": v(2.85, -6.98) * mm, "radius": 1 * mm});
            skCircle(sketch, "E2.31.1.0", {"center": v(2.85, -3.98) * mm, "radius": 1 * mm});
            skCircle(sketch, "E2.31.2.0", {"center": v(2.85, -0.98) * mm, "radius": 1 * mm});
            skCircle(sketch, "E2.31.3.0", {"center": v(2.85, 2.02) * mm, "radius": 1 * mm});
            skCircle(sketch, "E2.31.4.0", {"center": v(2.85, 5.02) * mm, "radius": 1 * mm});
            skCircle(sketch, "E2.31.5.0", {"center": v(2.85, 8.02) * mm, "radius": 1 * mm});
            skCircle(sketch, "E2.31.6.0", {"center": v(2.85, 11.02) * mm, "radius": 1 * mm});
            skCircle(sketch, "E2.31.7.0", {"center": v(2.85, 14.02) * mm, "radius": 1 * mm});
            skCircle(sketch, "E2.31.8.0", {"center": v(2.85, 17.02) * mm, "radius": 1 * mm});
            skCircle(sketch, "E2.31.9.0", {"center": v(2.85, 20.02) * mm, "radius": 1 * mm});
            skCircle(sketch, "E2.31.10.0", {"center": v(2.85, 23.02) * mm, "radius": 1 * mm});
            skCircle(sketch, "E2.31.11.0", {"center": v(2.85, 26.02) * mm, "radius": 1 * mm});
            skCircle(sketch, "E2.32.0.0", {"center": v(5.97, -6.98) * mm, "radius": 1 * mm});
            skCircle(sketch, "E2.32.1.0", {"center": v(5.97, -3.98) * mm, "radius": 1 * mm});
            skCircle(sketch, "E2.32.2.0", {"center": v(5.97, -0.98) * mm, "radius": 1 * mm});
            skCircle(sketch, "E2.32.3.0", {"center": v(5.97, 2.02) * mm, "radius": 1 * mm});
            skCircle(sketch, "E2.32.4.0", {"center": v(5.97, 5.02) * mm, "radius": 1 * mm});
            skCircle(sketch, "E2.32.5.0", {"center": v(5.97, 8.02) * mm, "radius": 1 * mm});
            skCircle(sketch, "E2.32.6.0", {"center": v(5.97, 11.02) * mm, "radius": 1 * mm});
            skCircle(sketch, "E2.32.7.0", {"center": v(5.97, 14.02) * mm, "radius": 1 * mm});
            skCircle(sketch, "E2.32.8.0", {"center": v(5.97, 17.02) * mm, "radius": 1 * mm});
            skCircle(sketch, "E2.32.9.0", {"center": v(5.97, 20.02) * mm, "radius": 1 * mm});
            skCircle(sketch, "E2.32.10.0", {"center": v(5.97, 23.02) * mm, "radius": 1 * mm});
            skCircle(sketch, "E2.32.11.0", {"center": v(5.97, 26.02) * mm, "radius": 1 * mm});
            skCircle(sketch, "E2.33.0.0", {"center": v(9.09, -6.98) * mm, "radius": 1 * mm});
            skCircle(sketch, "E2.33.1.0", {"center": v(9.09, -3.98) * mm, "radius": 1 * mm});
            skCircle(sketch, "E2.33.2.0", {"center": v(9.09, -0.98) * mm, "radius": 1 * mm});
            skCircle(sketch, "E2.33.3.0", {"center": v(9.09, 2.02) * mm, "radius": 1 * mm});
            skCircle(sketch, "E2.33.4.0", {"center": v(9.09, 5.02) * mm, "radius": 1 * mm});
            skCircle(sketch, "E2.33.5.0", {"center": v(9.09, 8.02) * mm, "radius": 1 * mm});
            skCircle(sketch, "E2.33.6.0", {"center": v(9.09, 11.02) * mm, "radius": 1 * mm});
            skCircle(sketch, "E2.33.7.0", {"center": v(9.09, 14.02) * mm, "radius": 1 * mm});
            skCircle(sketch, "E2.33.8.0", {"center": v(9.09, 17.02) * mm, "radius": 1 * mm});
            skCircle(sketch, "E2.33.9.0", {"center": v(9.09, 20.02) * mm, "radius": 1 * mm});
            skCircle(sketch, "E2.33.10.0", {"center": v(9.09, 23.02) * mm, "radius": 1 * mm});
            skCircle(sketch, "E2.33.11.0", {"center": v(9.09, 26.02) * mm, "radius": 1 * mm});
            skCircle(sketch, "E2.34.0.0", {"center": v(12.2, -6.98) * mm, "radius": 1 * mm});
            skCircle(sketch, "E2.34.1.0", {"center": v(12.2, -3.98) * mm, "radius": 1 * mm});
            skCircle(sketch, "E2.34.2.0", {"center": v(12.2, -0.98) * mm, "radius": 1 * mm});
            skCircle(sketch, "E2.34.3.0", {"center": v(12.2, 2.02) * mm, "radius": 1 * mm});
            skCircle(sketch, "E2.34.4.0", {"center": v(12.2, 5.02) * mm, "radius": 1 * mm});
            skCircle(sketch, "E2.34.5.0", {"center": v(12.2, 8.02) * mm, "radius": 1 * mm});
            skCircle(sketch, "E2.34.6.0", {"center": v(12.2, 11.02) * mm, "radius": 1 * mm});
            skCircle(sketch, "E2.34.7.0", {"center": v(12.2, 14.02) * mm, "radius": 1 * mm});
            skCircle(sketch, "E2.34.8.0", {"center": v(12.2, 17.02) * mm, "radius": 1 * mm});
            skCircle(sketch, "E2.34.9.0", {"center": v(12.2, 20.02) * mm, "radius": 1 * mm});
            skCircle(sketch, "E2.34.10.0", {"center": v(12.2, 23.02) * mm, "radius": 1 * mm});
            skCircle(sketch, "E2.34.11.0", {"center": v(12.2, 26.02) * mm, "radius": 1 * mm});
            skCircle(sketch, "E2.35.0.0", {"center": v(15.33, -6.98) * mm, "radius": 1 * mm});
            skCircle(sketch, "E2.35.1.0", {"center": v(15.33, -3.98) * mm, "radius": 1 * mm});
            skCircle(sketch, "E2.35.2.0", {"center": v(15.33, -0.98) * mm, "radius": 1 * mm});
            skCircle(sketch, "E2.35.3.0", {"center": v(15.33, 2.02) * mm, "radius": 1 * mm});
            skCircle(sketch, "E2.35.4.0", {"center": v(15.33, 5.02) * mm, "radius": 1 * mm});
            skCircle(sketch, "E2.35.5.0", {"center": v(15.33, 8.02) * mm, "radius": 1 * mm});
            skCircle(sketch, "E2.35.6.0", {"center": v(15.33, 11.02) * mm, "radius": 1 * mm});
            skCircle(sketch, "E2.35.7.0", {"center": v(15.33, 14.02) * mm, "radius": 1 * mm});
            skCircle(sketch, "E2.35.8.0", {"center": v(15.33, 17.02) * mm, "radius": 1 * mm});
            skCircle(sketch, "E2.35.9.0", {"center": v(15.33, 20.02) * mm, "radius": 1 * mm});
            skCircle(sketch, "E2.35.10.0", {"center": v(15.33, 23.02) * mm, "radius": 1 * mm});
            skCircle(sketch, "E2.35.11.0", {"center": v(15.33, 26.02) * mm, "radius": 1 * mm});
            skCircle(sketch, "E2.36.0.0", {"center": v(18.45, -6.98) * mm, "radius": 1 * mm});
            skCircle(sketch, "E2.36.1.0", {"center": v(18.45, -3.98) * mm, "radius": 1 * mm});
            skCircle(sketch, "E2.36.2.0", {"center": v(18.45, -0.98) * mm, "radius": 1 * mm});
            skCircle(sketch, "E2.36.3.0", {"center": v(18.45, 2.02) * mm, "radius": 1 * mm});
            skCircle(sketch, "E2.36.4.0", {"center": v(18.45, 5.02) * mm, "radius": 1 * mm});
            skCircle(sketch, "E2.36.5.0", {"center": v(18.45, 8.02) * mm, "radius": 1 * mm});
            skCircle(sketch, "E2.36.6.0", {"center": v(18.45, 11.02) * mm, "radius": 1 * mm});
            skCircle(sketch, "E2.36.7.0", {"center": v(18.45, 14.02) * mm, "radius": 1 * mm});
            skCircle(sketch, "E2.36.8.0", {"center": v(18.45, 17.02) * mm, "radius": 1 * mm});
            skCircle(sketch, "E2.36.9.0", {"center": v(18.45, 20.02) * mm, "radius": 1 * mm});
            skCircle(sketch, "E2.36.10.0", {"center": v(18.45, 23.02) * mm, "radius": 1 * mm});
            skCircle(sketch, "E2.36.11.0", {"center": v(18.45, 26.02) * mm, "radius": 1 * mm});
            skCircle(sketch, "E2.37.0.0", {"center": v(21.57, -6.98) * mm, "radius": 1 * mm});
            skCircle(sketch, "E2.37.1.0", {"center": v(21.57, -3.98) * mm, "radius": 1 * mm});
            skCircle(sketch, "E2.37.2.0", {"center": v(21.57, -0.98) * mm, "radius": 1 * mm});
            skCircle(sketch, "E2.37.3.0", {"center": v(21.57, 2.02) * mm, "radius": 1 * mm});
            skCircle(sketch, "E2.37.4.0", {"center": v(21.57, 5.02) * mm, "radius": 1 * mm});
            skCircle(sketch, "E2.37.5.0", {"center": v(21.57, 8.02) * mm, "radius": 1 * mm});
            skCircle(sketch, "E2.37.6.0", {"center": v(21.57, 11.02) * mm, "radius": 1 * mm});
            skCircle(sketch, "E2.37.7.0", {"center": v(21.57, 14.02) * mm, "radius": 1 * mm});
            skCircle(sketch, "E2.37.8.0", {"center": v(21.57, 17.02) * mm, "radius": 1 * mm});
            skCircle(sketch, "E2.37.9.0", {"center": v(21.57, 20.02) * mm, "radius": 1 * mm});
            skCircle(sketch, "E2.37.10.0", {"center": v(21.57, 23.02) * mm, "radius": 1 * mm});
            skCircle(sketch, "E2.37.11.0", {"center": v(21.57, 26.02) * mm, "radius": 1 * mm});
            skCircle(sketch, "E2.38.0.0", {"center": v(24.69, -6.98) * mm, "radius": 1 * mm});
            skCircle(sketch, "E2.38.1.0", {"center": v(24.69, -3.98) * mm, "radius": 1 * mm});
            skCircle(sketch, "E2.38.2.0", {"center": v(24.69, -0.98) * mm, "radius": 1 * mm});
            skCircle(sketch, "E2.38.3.0", {"center": v(24.69, 2.02) * mm, "radius": 1 * mm});
            skCircle(sketch, "E2.38.4.0", {"center": v(24.69, 5.02) * mm, "radius": 1 * mm});
            skCircle(sketch, "E2.38.5.0", {"center": v(24.69, 8.02) * mm, "radius": 1 * mm});
            skCircle(sketch, "E2.38.6.0", {"center": v(24.69, 11.02) * mm, "radius": 1 * mm});
            skCircle(sketch, "E2.38.7.0", {"center": v(24.69, 14.02) * mm, "radius": 1 * mm});
            skCircle(sketch, "E2.38.8.0", {"center": v(24.69, 17.02) * mm, "radius": 1 * mm});
            skCircle(sketch, "E2.38.9.0", {"center": v(24.69, 20.02) * mm, "radius": 1 * mm});
            skCircle(sketch, "E2.38.10.0", {"center": v(24.69, 23.02) * mm, "radius": 1 * mm});
            skCircle(sketch, "E2.38.11.0", {"center": v(24.69, 26.02) * mm, "radius": 1 * mm});
            skCircle(sketch, "E2.39.0.0", {"center": v(27.8, -6.98) * mm, "radius": 1 * mm});
            skCircle(sketch, "E2.39.1.0", {"center": v(27.8, -3.98) * mm, "radius": 1 * mm});
            skCircle(sketch, "E2.39.2.0", {"center": v(27.8, -0.98) * mm, "radius": 1 * mm});
            skCircle(sketch, "E2.39.3.0", {"center": v(27.8, 2.02) * mm, "radius": 1 * mm});
            skCircle(sketch, "E2.39.4.0", {"center": v(27.8, 5.02) * mm, "radius": 1 * mm});
            skCircle(sketch, "E2.39.5.0", {"center": v(27.8, 8.02) * mm, "radius": 1 * mm});
            skCircle(sketch, "E2.39.6.0", {"center": v(27.8, 11.02) * mm, "radius": 1 * mm});
            skCircle(sketch, "E2.39.7.0", {"center": v(27.8, 14.02) * mm, "radius": 1 * mm});
            skCircle(sketch, "E2.39.8.0", {"center": v(27.8, 17.02) * mm, "radius": 1 * mm});
            skCircle(sketch, "E2.39.9.0", {"center": v(27.8, 20.02) * mm, "radius": 1 * mm});
            skCircle(sketch, "E2.39.10.0", {"center": v(27.8, 23.02) * mm, "radius": 1 * mm});
            skCircle(sketch, "E2.39.11.0", {"center": v(27.8, 26.02) * mm, "radius": 1 * mm});
            skCircle(sketch, "E2.40.0.0", {"center": v(30.93, -6.98) * mm, "radius": 1 * mm});
            skCircle(sketch, "E2.40.1.0", {"center": v(30.93, -3.98) * mm, "radius": 1 * mm});
            skCircle(sketch, "E2.40.2.0", {"center": v(30.93, -0.98) * mm, "radius": 1 * mm});
            skCircle(sketch, "E2.40.3.0", {"center": v(30.93, 2.02) * mm, "radius": 1 * mm});
            skCircle(sketch, "E2.40.4.0", {"center": v(30.93, 5.02) * mm, "radius": 1 * mm});
            skCircle(sketch, "E2.40.5.0", {"center": v(30.93, 8.02) * mm, "radius": 1 * mm});
            skCircle(sketch, "E2.40.6.0", {"center": v(30.93, 11.02) * mm, "radius": 1 * mm});
            skCircle(sketch, "E2.40.7.0", {"center": v(30.93, 14.02) * mm, "radius": 1 * mm});
            skCircle(sketch, "E2.40.8.0", {"center": v(30.93, 17.02) * mm, "radius": 1 * mm});
            skCircle(sketch, "E2.40.9.0", {"center": v(30.93, 20.02) * mm, "radius": 1 * mm});
            skCircle(sketch, "E2.40.10.0", {"center": v(30.93, 23.02) * mm, "radius": 1 * mm});
            skCircle(sketch, "E2.40.11.0", {"center": v(30.93, 26.02) * mm, "radius": 1 * mm});
            skCircle(sketch, "E2.41.0.0", {"center": v(34.05, -6.98) * mm, "radius": 1 * mm});
            skCircle(sketch, "E2.41.1.0", {"center": v(34.05, -3.98) * mm, "radius": 1 * mm});
            skCircle(sketch, "E2.41.2.0", {"center": v(34.05, -0.98) * mm, "radius": 1 * mm});
            skCircle(sketch, "E2.41.3.0", {"center": v(34.05, 2.02) * mm, "radius": 1 * mm});
            skCircle(sketch, "E2.41.4.0", {"center": v(34.05, 5.02) * mm, "radius": 1 * mm});
            skCircle(sketch, "E2.41.5.0", {"center": v(34.05, 8.02) * mm, "radius": 1 * mm});
            skCircle(sketch, "E2.41.6.0", {"center": v(34.05, 11.02) * mm, "radius": 1 * mm});
            skCircle(sketch, "E2.41.7.0", {"center": v(34.05, 14.02) * mm, "radius": 1 * mm});
            skCircle(sketch, "E2.41.8.0", {"center": v(34.05, 17.02) * mm, "radius": 1 * mm});
            skCircle(sketch, "E2.41.9.0", {"center": v(34.05, 20.02) * mm, "radius": 1 * mm});
            skCircle(sketch, "E2.41.10.0", {"center": v(34.05, 23.02) * mm, "radius": 1 * mm});
            skCircle(sketch, "E2.41.11.0", {"center": v(34.05, 26.02) * mm, "radius": 1 * mm});
            skCircle(sketch, "E2.42.0.0", {"center": v(37.17, -6.98) * mm, "radius": 1 * mm});
            skCircle(sketch, "E2.42.1.0", {"center": v(37.17, -3.98) * mm, "radius": 1 * mm});
            skCircle(sketch, "E2.42.2.0", {"center": v(37.17, -0.98) * mm, "radius": 1 * mm});
            skCircle(sketch, "E2.42.3.0", {"center": v(37.17, 2.02) * mm, "radius": 1 * mm});
            skCircle(sketch, "E2.42.4.0", {"center": v(37.17, 5.02) * mm, "radius": 1 * mm});
            skCircle(sketch, "E2.42.5.0", {"center": v(37.17, 8.02) * mm, "radius": 1 * mm});
            skCircle(sketch, "E2.42.6.0", {"center": v(37.17, 11.02) * mm, "radius": 1 * mm});
            skCircle(sketch, "E2.42.7.0", {"center": v(37.17, 14.02) * mm, "radius": 1 * mm});
            skCircle(sketch, "E2.42.8.0", {"center": v(37.17, 17.02) * mm, "radius": 1 * mm});
            skCircle(sketch, "E2.42.9.0", {"center": v(37.17, 20.02) * mm, "radius": 1 * mm});
            skCircle(sketch, "E2.42.10.0", {"center": v(37.17, 23.02) * mm, "radius": 1 * mm});
            skCircle(sketch, "E2.42.11.0", {"center": v(37.17, 26.02) * mm, "radius": 1 * mm});
            skCircle(sketch, "E2.43.0.0", {"center": v(40.29, -6.98) * mm, "radius": 1 * mm});
            skCircle(sketch, "E2.43.1.0", {"center": v(40.29, -3.98) * mm, "radius": 1 * mm});
            skCircle(sketch, "E2.43.2.0", {"center": v(40.29, -0.98) * mm, "radius": 1 * mm});
            skCircle(sketch, "E2.43.3.0", {"center": v(40.29, 2.02) * mm, "radius": 1 * mm});
            skCircle(sketch, "E2.43.4.0", {"center": v(40.29, 5.02) * mm, "radius": 1 * mm});
            skCircle(sketch, "E2.43.5.0", {"center": v(40.29, 8.02) * mm, "radius": 1 * mm});
            skCircle(sketch, "E2.43.6.0", {"center": v(40.29, 11.02) * mm, "radius": 1 * mm});
            skCircle(sketch, "E2.43.7.0", {"center": v(40.29, 14.02) * mm, "radius": 1 * mm});
            skCircle(sketch, "E2.43.8.0", {"center": v(40.29, 17.02) * mm, "radius": 1 * mm});
            skCircle(sketch, "E2.43.9.0", {"center": v(40.29, 20.02) * mm, "radius": 1 * mm});
            skCircle(sketch, "E2.43.10.0", {"center": v(40.29, 23.02) * mm, "radius": 1 * mm});
            skCircle(sketch, "E2.43.11.0", {"center": v(40.29, 26.02) * mm, "radius": 1 * mm});
            skCircle(sketch, "E2.44.0.0", {"center": v(43.4, -6.98) * mm, "radius": 1 * mm});
            skCircle(sketch, "E2.44.1.0", {"center": v(43.4, -3.98) * mm, "radius": 1 * mm});
            skCircle(sketch, "E2.44.2.0", {"center": v(43.4, -0.98) * mm, "radius": 1 * mm});
            skCircle(sketch, "E2.44.3.0", {"center": v(43.4, 2.02) * mm, "radius": 1 * mm});
            skCircle(sketch, "E2.44.4.0", {"center": v(43.4, 5.02) * mm, "radius": 1 * mm});
            skCircle(sketch, "E2.44.5.0", {"center": v(43.4, 8.02) * mm, "radius": 1 * mm});
            skCircle(sketch, "E2.44.6.0", {"center": v(43.4, 11.02) * mm, "radius": 1 * mm});
            skCircle(sketch, "E2.44.7.0", {"center": v(43.4, 14.02) * mm, "radius": 1 * mm});
            skCircle(sketch, "E2.44.8.0", {"center": v(43.4, 17.02) * mm, "radius": 1 * mm});
            skCircle(sketch, "E2.44.9.0", {"center": v(43.4, 20.02) * mm, "radius": 1 * mm});
            skCircle(sketch, "E2.44.10.0", {"center": v(43.4, 23.02) * mm, "radius": 1 * mm});
            skCircle(sketch, "E2.44.11.0", {"center": v(43.4, 26.02) * mm, "radius": 1 * mm});
            skCircle(sketch, "E2.45.0.0", {"center": v(46.53, -6.98) * mm, "radius": 1 * mm});
            skCircle(sketch, "E2.45.1.0", {"center": v(46.53, -3.98) * mm, "radius": 1 * mm});
            skCircle(sketch, "E2.45.2.0", {"center": v(46.53, -0.98) * mm, "radius": 1 * mm});
            skCircle(sketch, "E2.45.3.0", {"center": v(46.53, 2.02) * mm, "radius": 1 * mm});
            skCircle(sketch, "E2.45.4.0", {"center": v(46.53, 5.02) * mm, "radius": 1 * mm});
            skCircle(sketch, "E2.45.5.0", {"center": v(46.53, 8.02) * mm, "radius": 1 * mm});
            skCircle(sketch, "E2.45.6.0", {"center": v(46.53, 11.02) * mm, "radius": 1 * mm});
            skCircle(sketch, "E2.45.7.0", {"center": v(46.53, 14.02) * mm, "radius": 1 * mm});
            skCircle(sketch, "E2.45.8.0", {"center": v(46.53, 17.02) * mm, "radius": 1 * mm});
            skCircle(sketch, "E2.45.9.0", {"center": v(46.53, 20.02) * mm, "radius": 1 * mm});
            skCircle(sketch, "E2.45.10.0", {"center": v(46.53, 23.02) * mm, "radius": 1 * mm});
            skCircle(sketch, "E2.45.11.0", {"center": v(46.53, 26.02) * mm, "radius": 1 * mm});
            skCircle(sketch, "E2.46.0.0", {"center": v(49.65, -6.98) * mm, "radius": 1 * mm});
            skCircle(sketch, "E2.46.1.0", {"center": v(49.65, -3.98) * mm, "radius": 1 * mm});
            skCircle(sketch, "E2.46.2.0", {"center": v(49.65, -0.98) * mm, "radius": 1 * mm});
            skCircle(sketch, "E2.46.3.0", {"center": v(49.65, 2.02) * mm, "radius": 1 * mm});
            skCircle(sketch, "E2.46.4.0", {"center": v(49.65, 5.02) * mm, "radius": 1 * mm});
            skCircle(sketch, "E2.46.5.0", {"center": v(49.65, 8.02) * mm, "radius": 1 * mm});
            skCircle(sketch, "E2.46.6.0", {"center": v(49.65, 11.02) * mm, "radius": 1 * mm});
            skCircle(sketch, "E2.46.7.0", {"center": v(49.65, 14.02) * mm, "radius": 1 * mm});
            skCircle(sketch, "E2.46.8.0", {"center": v(49.65, 17.02) * mm, "radius": 1 * mm});
            skCircle(sketch, "E2.46.9.0", {"center": v(49.65, 20.02) * mm, "radius": 1 * mm});
            skCircle(sketch, "E2.46.10.0", {"center": v(49.65, 23.02) * mm, "radius": 1 * mm});
            skCircle(sketch, "E2.46.11.0", {"center": v(49.65, 26.02) * mm, "radius": 1 * mm});
            skCircle(sketch, "E2.47.0.0", {"center": v(52.77, -6.98) * mm, "radius": 1 * mm});
            skCircle(sketch, "E2.47.1.0", {"center": v(52.77, -3.98) * mm, "radius": 1 * mm});
            skCircle(sketch, "E2.47.2.0", {"center": v(52.77, -0.98) * mm, "radius": 1 * mm});
            skCircle(sketch, "E2.47.3.0", {"center": v(52.77, 2.02) * mm, "radius": 1 * mm});
            skCircle(sketch, "E2.47.4.0", {"center": v(52.77, 5.02) * mm, "radius": 1 * mm});
            skCircle(sketch, "E2.47.5.0", {"center": v(52.77, 8.02) * mm, "radius": 1 * mm});
            skCircle(sketch, "E2.47.6.0", {"center": v(52.77, 11.02) * mm, "radius": 1 * mm});
            skCircle(sketch, "E2.47.7.0", {"center": v(52.77, 14.02) * mm, "radius": 1 * mm});
            skCircle(sketch, "E2.47.8.0", {"center": v(52.77, 17.02) * mm, "radius": 1 * mm});
            skCircle(sketch, "E2.47.9.0", {"center": v(52.77, 20.02) * mm, "radius": 1 * mm});
            skCircle(sketch, "E2.47.10.0", {"center": v(52.77, 23.02) * mm, "radius": 1 * mm});
            skCircle(sketch, "E2.47.11.0", {"center": v(52.77, 26.02) * mm, "radius": 1 * mm});
            skCircle(sketch, "E2.48.0.0", {"center": v(55.89, -6.98) * mm, "radius": 1 * mm});
            skCircle(sketch, "E2.48.1.0", {"center": v(55.89, -3.98) * mm, "radius": 1 * mm});
            skCircle(sketch, "E2.48.2.0", {"center": v(55.89, -0.98) * mm, "radius": 1 * mm});
            skCircle(sketch, "E2.48.3.0", {"center": v(55.89, 2.02) * mm, "radius": 1 * mm});
            skCircle(sketch, "E2.48.4.0", {"center": v(55.89, 5.02) * mm, "radius": 1 * mm});
            skCircle(sketch, "E2.48.5.0", {"center": v(55.89, 8.02) * mm, "radius": 1 * mm});
            skCircle(sketch, "E2.48.6.0", {"center": v(55.89, 11.02) * mm, "radius": 1 * mm});
            skCircle(sketch, "E2.48.7.0", {"center": v(55.89, 14.02) * mm, "radius": 1 * mm});
            skCircle(sketch, "E2.48.8.0", {"center": v(55.89, 17.02) * mm, "radius": 1 * mm});
            skCircle(sketch, "E2.48.9.0", {"center": v(55.89, 20.02) * mm, "radius": 1 * mm});
            skCircle(sketch, "E2.48.10.0", {"center": v(55.89, 23.02) * mm, "radius": 1 * mm});
            skCircle(sketch, "E2.48.11.0", {"center": v(55.89, 26.02) * mm, "radius": 1 * mm});
            skCircle(sketch, "E2.49.0.0", {"center": v(59, -6.98) * mm, "radius": 1 * mm});
            skCircle(sketch, "E2.49.1.0", {"center": v(59, -3.98) * mm, "radius": 1 * mm});
            skCircle(sketch, "E2.49.2.0", {"center": v(59, -0.98) * mm, "radius": 1 * mm});
            skCircle(sketch, "E2.49.3.0", {"center": v(59, 2.02) * mm, "radius": 1 * mm});
            skCircle(sketch, "E2.49.4.0", {"center": v(59, 5.02) * mm, "radius": 1 * mm});
            skCircle(sketch, "E2.49.5.0", {"center": v(59, 8.02) * mm, "radius": 1 * mm});
            skCircle(sketch, "E2.49.6.0", {"center": v(59, 11.02) * mm, "radius": 1 * mm});
            skCircle(sketch, "E2.49.7.0", {"center": v(59, 14.02) * mm, "radius": 1 * mm});
            skCircle(sketch, "E2.49.8.0", {"center": v(59, 17.02) * mm, "radius": 1 * mm});
            skCircle(sketch, "E2.49.9.0", {"center": v(59, 20.02) * mm, "radius": 1 * mm});
            skCircle(sketch, "E2.49.10.0", {"center": v(59, 23.02) * mm, "radius": 1 * mm});
            skCircle(sketch, "E2.49.11.0", {"center": v(59, 26.02) * mm, "radius": 1 * mm});
            skLineSegment(sketch, "E2.direction1", {"start": v(-93.87, -6.98) * mm, "end": v(-90.75, -6.98) * mm, "construction": true});
            skLineSegment(sketch, "E2.direction2", {"start": v(-93.87, -6.98) * mm, "end": v(-93.87, -3.98) * mm, "construction": true});
            skCircle(sketch, "E3.0.50.0", {"center": v(62.13, -6.98) * mm, "radius": 1 * mm});
            skCircle(sketch, "E3.0.50.1", {"center": v(62.13, -3.98) * mm, "radius": 1 * mm});
            skCircle(sketch, "E3.0.50.2", {"center": v(62.13, -0.98) * mm, "radius": 1 * mm});
            skCircle(sketch, "E3.0.50.3", {"center": v(62.13, 2.02) * mm, "radius": 1 * mm});
            skCircle(sketch, "E3.0.50.4", {"center": v(62.13, 5.02) * mm, "radius": 1 * mm});
            skCircle(sketch, "E3.0.50.5", {"center": v(62.13, 8.02) * mm, "radius": 1 * mm});
            skCircle(sketch, "E3.0.50.6", {"center": v(62.13, 11.02) * mm, "radius": 1 * mm});
            skCircle(sketch, "E3.0.50.7", {"center": v(62.13, 14.02) * mm, "radius": 1 * mm});
            skCircle(sketch, "E3.0.50.8", {"center": v(62.13, 17.02) * mm, "radius": 1 * mm});
            skCircle(sketch, "E3.0.50.9", {"center": v(62.13, 20.02) * mm, "radius": 1 * mm});
            skCircle(sketch, "E3.0.50.10", {"center": v(62.13, 23.02) * mm, "radius": 1 * mm});
            skCircle(sketch, "E3.0.50.11", {"center": v(62.13, 26.02) * mm, "radius": 1 * mm});
            skCircle(sketch, "E3.0.51.0", {"center": v(65.25, -6.98) * mm, "radius": 1 * mm});
            skCircle(sketch, "E3.0.51.1", {"center": v(65.25, -3.98) * mm, "radius": 1 * mm});
            skCircle(sketch, "E3.0.51.2", {"center": v(65.25, -0.98) * mm, "radius": 1 * mm});
            skCircle(sketch, "E3.0.51.3", {"center": v(65.25, 2.02) * mm, "radius": 1 * mm});
            skCircle(sketch, "E3.0.51.4", {"center": v(65.25, 5.02) * mm, "radius": 1 * mm});
            skCircle(sketch, "E3.0.51.5", {"center": v(65.25, 8.02) * mm, "radius": 1 * mm});
            skCircle(sketch, "E3.0.51.6", {"center": v(65.25, 11.02) * mm, "radius": 1 * mm});
            skCircle(sketch, "E3.0.51.7", {"center": v(65.25, 14.02) * mm, "radius": 1 * mm});
            skCircle(sketch, "E3.0.51.8", {"center": v(65.25, 17.02) * mm, "radius": 1 * mm});
            skCircle(sketch, "E3.0.51.9", {"center": v(65.25, 20.02) * mm, "radius": 1 * mm});
            skCircle(sketch, "E3.0.51.10", {"center": v(65.25, 23.02) * mm, "radius": 1 * mm});
            skCircle(sketch, "E3.0.51.11", {"center": v(65.25, 26.02) * mm, "radius": 1 * mm});
            skCircle(sketch, "E3.0.52.0", {"center": v(68.37, -6.98) * mm, "radius": 1 * mm});
            skCircle(sketch, "E3.0.52.1", {"center": v(68.37, -3.98) * mm, "radius": 1 * mm});
            skCircle(sketch, "E3.0.52.2", {"center": v(68.37, -0.98) * mm, "radius": 1 * mm});
            skCircle(sketch, "E3.0.52.3", {"center": v(68.37, 2.02) * mm, "radius": 1 * mm});
            skCircle(sketch, "E3.0.52.4", {"center": v(68.37, 5.02) * mm, "radius": 1 * mm});
            skCircle(sketch, "E3.0.52.5", {"center": v(68.37, 8.02) * mm, "radius": 1 * mm});
            skCircle(sketch, "E3.0.52.6", {"center": v(68.37, 11.02) * mm, "radius": 1 * mm});
            skCircle(sketch, "E3.0.52.7", {"center": v(68.37, 14.02) * mm, "radius": 1 * mm});
            skCircle(sketch, "E3.0.52.8", {"center": v(68.37, 17.02) * mm, "radius": 1 * mm});
            skCircle(sketch, "E3.0.52.9", {"center": v(68.37, 20.02) * mm, "radius": 1 * mm});
            skCircle(sketch, "E3.0.52.10", {"center": v(68.37, 23.02) * mm, "radius": 1 * mm});
            skCircle(sketch, "E3.0.52.11", {"center": v(68.37, 26.02) * mm, "radius": 1 * mm});
            skCircle(sketch, "E3.0.53.0", {"center": v(71.49, -6.98) * mm, "radius": 1 * mm});
            skCircle(sketch, "E3.0.53.1", {"center": v(71.49, -3.98) * mm, "radius": 1 * mm});
            skCircle(sketch, "E3.0.53.2", {"center": v(71.49, -0.98) * mm, "radius": 1 * mm});
            skCircle(sketch, "E3.0.53.3", {"center": v(71.49, 2.02) * mm, "radius": 1 * mm});
            skCircle(sketch, "E3.0.53.4", {"center": v(71.49, 5.02) * mm, "radius": 1 * mm});
            skCircle(sketch, "E3.0.53.5", {"center": v(71.49, 8.02) * mm, "radius": 1 * mm});
            skCircle(sketch, "E3.0.53.6", {"center": v(71.49, 11.02) * mm, "radius": 1 * mm});
            skCircle(sketch, "E3.0.53.7", {"center": v(71.49, 14.02) * mm, "radius": 1 * mm});
            skCircle(sketch, "E3.0.53.8", {"center": v(71.49, 17.02) * mm, "radius": 1 * mm});
            skCircle(sketch, "E3.0.53.9", {"center": v(71.49, 20.02) * mm, "radius": 1 * mm});
            skCircle(sketch, "E3.0.53.10", {"center": v(71.49, 23.02) * mm, "radius": 1 * mm});
            skCircle(sketch, "E3.0.53.11", {"center": v(71.49, 26.02) * mm, "radius": 1 * mm});
            skCircle(sketch, "E3.0.54.0", {"center": v(74.6, -6.98) * mm, "radius": 1 * mm});
            skCircle(sketch, "E3.0.54.1", {"center": v(74.6, -3.98) * mm, "radius": 1 * mm});
            skCircle(sketch, "E3.0.54.2", {"center": v(74.6, -0.98) * mm, "radius": 1 * mm});
            skCircle(sketch, "E3.0.54.3", {"center": v(74.6, 2.02) * mm, "radius": 1 * mm});
            skCircle(sketch, "E3.0.54.4", {"center": v(74.6, 5.02) * mm, "radius": 1 * mm});
            skCircle(sketch, "E3.0.54.5", {"center": v(74.6, 8.02) * mm, "radius": 1 * mm});
            skCircle(sketch, "E3.0.54.6", {"center": v(74.6, 11.02) * mm, "radius": 1 * mm});
            skCircle(sketch, "E3.0.54.7", {"center": v(74.6, 14.02) * mm, "radius": 1 * mm});
            skCircle(sketch, "E3.0.54.8", {"center": v(74.6, 17.02) * mm, "radius": 1 * mm});
            skCircle(sketch, "E3.0.54.9", {"center": v(74.6, 20.02) * mm, "radius": 1 * mm});
            skCircle(sketch, "E3.0.54.10", {"center": v(74.6, 23.02) * mm, "radius": 1 * mm});
            skCircle(sketch, "E3.0.54.11", {"center": v(74.6, 26.02) * mm, "radius": 1 * mm});
            skCircle(sketch, "E3.0.55.0", {"center": v(77.73, -6.98) * mm, "radius": 1 * mm});
            skCircle(sketch, "E3.0.55.1", {"center": v(77.73, -3.98) * mm, "radius": 1 * mm});
            skCircle(sketch, "E3.0.55.2", {"center": v(77.73, -0.98) * mm, "radius": 1 * mm});
            skCircle(sketch, "E3.0.55.3", {"center": v(77.73, 2.02) * mm, "radius": 1 * mm});
            skCircle(sketch, "E3.0.55.4", {"center": v(77.73, 5.02) * mm, "radius": 1 * mm});
            skCircle(sketch, "E3.0.55.5", {"center": v(77.73, 8.02) * mm, "radius": 1 * mm});
            skCircle(sketch, "E3.0.55.6", {"center": v(77.73, 11.02) * mm, "radius": 1 * mm});
            skCircle(sketch, "E3.0.55.7", {"center": v(77.73, 14.02) * mm, "radius": 1 * mm});
            skCircle(sketch, "E3.0.55.8", {"center": v(77.73, 17.02) * mm, "radius": 1 * mm});
            skCircle(sketch, "E3.0.55.9", {"center": v(77.73, 20.02) * mm, "radius": 1 * mm});
            skCircle(sketch, "E3.0.55.10", {"center": v(77.73, 23.02) * mm, "radius": 1 * mm});
            skCircle(sketch, "E3.0.55.11", {"center": v(77.73, 26.02) * mm, "radius": 1 * mm});
            skCircle(sketch, "E3.0.56.0", {"center": v(80.85, -6.98) * mm, "radius": 1 * mm});
            skCircle(sketch, "E3.0.56.1", {"center": v(80.85, -3.98) * mm, "radius": 1 * mm});
            skCircle(sketch, "E3.0.56.2", {"center": v(80.85, -0.98) * mm, "radius": 1 * mm});
            skCircle(sketch, "E3.0.56.3", {"center": v(80.85, 2.02) * mm, "radius": 1 * mm});
            skCircle(sketch, "E3.0.56.4", {"center": v(80.85, 5.02) * mm, "radius": 1 * mm});
            skCircle(sketch, "E3.0.56.5", {"center": v(80.85, 8.02) * mm, "radius": 1 * mm});
            skCircle(sketch, "E3.0.56.6", {"center": v(80.85, 11.02) * mm, "radius": 1 * mm});
            skCircle(sketch, "E3.0.56.7", {"center": v(80.85, 14.02) * mm, "radius": 1 * mm});
            skCircle(sketch, "E3.0.56.8", {"center": v(80.85, 17.02) * mm, "radius": 1 * mm});
            skCircle(sketch, "E3.0.56.9", {"center": v(80.85, 20.02) * mm, "radius": 1 * mm});
            skCircle(sketch, "E3.0.56.10", {"center": v(80.85, 23.02) * mm, "radius": 1 * mm});
            skCircle(sketch, "E3.0.56.11", {"center": v(80.85, 26.02) * mm, "radius": 1 * mm});
            skCircle(sketch, "E3.0.57.0", {"center": v(83.97, -6.98) * mm, "radius": 1 * mm});
            skCircle(sketch, "E3.0.57.1", {"center": v(83.97, -3.98) * mm, "radius": 1 * mm});
            skCircle(sketch, "E3.0.57.2", {"center": v(83.97, -0.98) * mm, "radius": 1 * mm});
            skCircle(sketch, "E3.0.57.3", {"center": v(83.97, 2.02) * mm, "radius": 1 * mm});
            skCircle(sketch, "E3.0.57.4", {"center": v(83.97, 5.02) * mm, "radius": 1 * mm});
            skCircle(sketch, "E3.0.57.5", {"center": v(83.97, 8.02) * mm, "radius": 1 * mm});
            skCircle(sketch, "E3.0.57.6", {"center": v(83.97, 11.02) * mm, "radius": 1 * mm});
            skCircle(sketch, "E3.0.57.7", {"center": v(83.97, 14.02) * mm, "radius": 1 * mm});
            skCircle(sketch, "E3.0.57.8", {"center": v(83.97, 17.02) * mm, "radius": 1 * mm});
            skCircle(sketch, "E3.0.57.9", {"center": v(83.97, 20.02) * mm, "radius": 1 * mm});
            skCircle(sketch, "E3.0.57.10", {"center": v(83.97, 23.02) * mm, "radius": 1 * mm});
            skCircle(sketch, "E3.0.57.11", {"center": v(83.97, 26.02) * mm, "radius": 1 * mm});
            skCircle(sketch, "E3.0.58.0", {"center": v(87.09, -6.98) * mm, "radius": 1 * mm});
            skCircle(sketch, "E3.0.58.1", {"center": v(87.09, -3.98) * mm, "radius": 1 * mm});
            skCircle(sketch, "E3.0.58.2", {"center": v(87.09, -0.98) * mm, "radius": 1 * mm});
            skCircle(sketch, "E3.0.58.3", {"center": v(87.09, 2.02) * mm, "radius": 1 * mm});
            skCircle(sketch, "E3.0.58.4", {"center": v(87.09, 5.02) * mm, "radius": 1 * mm});
            skCircle(sketch, "E3.0.58.5", {"center": v(87.09, 8.02) * mm, "radius": 1 * mm});
            skCircle(sketch, "E3.0.58.6", {"center": v(87.09, 11.02) * mm, "radius": 1 * mm});
            skCircle(sketch, "E3.0.58.7", {"center": v(87.09, 14.02) * mm, "radius": 1 * mm});
            skCircle(sketch, "E3.0.58.8", {"center": v(87.09, 17.02) * mm, "radius": 1 * mm});
            skCircle(sketch, "E3.0.58.9", {"center": v(87.09, 20.02) * mm, "radius": 1 * mm});
            skCircle(sketch, "E3.0.58.10", {"center": v(87.09, 23.02) * mm, "radius": 1 * mm});
            skCircle(sketch, "E3.0.58.11", {"center": v(87.09, 26.02) * mm, "radius": 1 * mm});
            skCircle(sketch, "E3.0.59.0", {"center": v(90.2, -6.98) * mm, "radius": 1 * mm});
            skCircle(sketch, "E3.0.59.1", {"center": v(90.2, -3.98) * mm, "radius": 1 * mm});
            skCircle(sketch, "E3.0.59.2", {"center": v(90.2, -0.98) * mm, "radius": 1 * mm});
            skCircle(sketch, "E3.0.59.3", {"center": v(90.2, 2.02) * mm, "radius": 1 * mm});
            skCircle(sketch, "E3.0.59.4", {"center": v(90.2, 5.02) * mm, "radius": 1 * mm});
            skCircle(sketch, "E3.0.59.5", {"center": v(90.2, 8.02) * mm, "radius": 1 * mm});
            skCircle(sketch, "E3.0.59.6", {"center": v(90.2, 11.02) * mm, "radius": 1 * mm});
            skCircle(sketch, "E3.0.59.7", {"center": v(90.2, 14.02) * mm, "radius": 1 * mm});
            skCircle(sketch, "E3.0.59.8", {"center": v(90.2, 17.02) * mm, "radius": 1 * mm});
            skCircle(sketch, "E3.0.59.9", {"center": v(90.2, 20.02) * mm, "radius": 1 * mm});
            skCircle(sketch, "E3.0.59.10", {"center": v(90.2, 23.02) * mm, "radius": 1 * mm});
            skCircle(sketch, "E3.0.59.11", {"center": v(90.2, 26.02) * mm, "radius": 1 * mm});
            skCircle(sketch, "E3.0.60.0", {"center": v(93.33, -6.98) * mm, "radius": 1 * mm});
            skCircle(sketch, "E3.0.60.1", {"center": v(93.33, -3.98) * mm, "radius": 1 * mm});
            skCircle(sketch, "E3.0.60.2", {"center": v(93.33, -0.98) * mm, "radius": 1 * mm});
            skCircle(sketch, "E3.0.60.3", {"center": v(93.33, 2.02) * mm, "radius": 1 * mm});
            skCircle(sketch, "E3.0.60.4", {"center": v(93.33, 5.02) * mm, "radius": 1 * mm});
            skCircle(sketch, "E3.0.60.5", {"center": v(93.33, 8.02) * mm, "radius": 1 * mm});
            skCircle(sketch, "E3.0.60.6", {"center": v(93.33, 11.02) * mm, "radius": 1 * mm});
            skCircle(sketch, "E3.0.60.7", {"center": v(93.33, 14.02) * mm, "radius": 1 * mm});
            skCircle(sketch, "E3.0.60.8", {"center": v(93.33, 17.02) * mm, "radius": 1 * mm});
            skCircle(sketch, "E3.0.60.9", {"center": v(93.33, 20.02) * mm, "radius": 1 * mm});
            skCircle(sketch, "E3.0.60.10", {"center": v(93.33, 23.02) * mm, "radius": 1 * mm});
            skCircle(sketch, "E3.0.60.11", {"center": v(93.33, 26.02) * mm, "radius": 1 * mm});
            skCircle(sketch, "E3.0.61.0", {"center": v(96.45, -6.98) * mm, "radius": 1 * mm});
            skCircle(sketch, "E3.0.61.1", {"center": v(96.45, -3.98) * mm, "radius": 1 * mm});
            skCircle(sketch, "E3.0.61.2", {"center": v(96.45, -0.98) * mm, "radius": 1 * mm});
            skCircle(sketch, "E3.0.61.3", {"center": v(96.45, 2.02) * mm, "radius": 1 * mm});
            skCircle(sketch, "E3.0.61.4", {"center": v(96.45, 5.02) * mm, "radius": 1 * mm});
            skCircle(sketch, "E3.0.61.5", {"center": v(96.45, 8.02) * mm, "radius": 1 * mm});
            skCircle(sketch, "E3.0.61.6", {"center": v(96.45, 11.02) * mm, "radius": 1 * mm});
            skCircle(sketch, "E3.0.61.7", {"center": v(96.45, 14.02) * mm, "radius": 1 * mm});
            skCircle(sketch, "E3.0.61.8", {"center": v(96.45, 17.02) * mm, "radius": 1 * mm});
            skCircle(sketch, "E3.0.61.9", {"center": v(96.45, 20.02) * mm, "radius": 1 * mm});
            skCircle(sketch, "E3.0.61.10", {"center": v(96.45, 23.02) * mm, "radius": 1 * mm});
            skCircle(sketch, "E3.0.61.11", {"center": v(96.45, 26.02) * mm, "radius": 1 * mm});
            skCircle(sketch, "E3.0.62.0", {"center": v(99.57, -6.98) * mm, "radius": 1 * mm});
            skCircle(sketch, "E3.0.62.1", {"center": v(99.57, -3.98) * mm, "radius": 1 * mm});
            skCircle(sketch, "E3.0.62.2", {"center": v(99.57, -0.98) * mm, "radius": 1 * mm});
            skCircle(sketch, "E3.0.62.3", {"center": v(99.57, 2.02) * mm, "radius": 1 * mm});
            skCircle(sketch, "E3.0.62.4", {"center": v(99.57, 5.02) * mm, "radius": 1 * mm});
            skCircle(sketch, "E3.0.62.5", {"center": v(99.57, 8.02) * mm, "radius": 1 * mm});
            skCircle(sketch, "E3.0.62.6", {"center": v(99.57, 11.02) * mm, "radius": 1 * mm});
            skCircle(sketch, "E3.0.62.7", {"center": v(99.57, 14.02) * mm, "radius": 1 * mm});
            skCircle(sketch, "E3.0.62.8", {"center": v(99.57, 17.02) * mm, "radius": 1 * mm});
            skCircle(sketch, "E3.0.62.9", {"center": v(99.57, 20.02) * mm, "radius": 1 * mm});
            skCircle(sketch, "E3.0.62.10", {"center": v(99.57, 23.02) * mm, "radius": 1 * mm});
            skCircle(sketch, "E3.0.62.11", {"center": v(99.57, 26.02) * mm, "radius": 1 * mm});
            skCircle(sketch, "E3.0.63.0", {"center": v(102.69, -6.98) * mm, "radius": 1 * mm});
            skCircle(sketch, "E3.0.63.1", {"center": v(102.69, -3.98) * mm, "radius": 1 * mm});
            skCircle(sketch, "E3.0.63.2", {"center": v(102.69, -0.98) * mm, "radius": 1 * mm});
            skCircle(sketch, "E3.0.63.3", {"center": v(102.69, 2.02) * mm, "radius": 1 * mm});
            skCircle(sketch, "E3.0.63.4", {"center": v(102.69, 5.02) * mm, "radius": 1 * mm});
            skCircle(sketch, "E3.0.63.5", {"center": v(102.69, 8.02) * mm, "radius": 1 * mm});
            skCircle(sketch, "E3.0.63.6", {"center": v(102.69, 11.02) * mm, "radius": 1 * mm});
            skCircle(sketch, "E3.0.63.7", {"center": v(102.69, 14.02) * mm, "radius": 1 * mm});
            skCircle(sketch, "E3.0.63.8", {"center": v(102.69, 17.02) * mm, "radius": 1 * mm});
            skCircle(sketch, "E3.0.63.9", {"center": v(102.69, 20.02) * mm, "radius": 1 * mm});
            skCircle(sketch, "E3.0.63.10", {"center": v(102.69, 23.02) * mm, "radius": 1 * mm});
            skCircle(sketch, "E3.0.63.11", {"center": v(102.69, 26.02) * mm, "radius": 1 * mm});
            skCircle(sketch, "E3.0.64.0", {"center": v(105.8, -6.98) * mm, "radius": 1 * mm});
            skCircle(sketch, "E3.0.64.1", {"center": v(105.8, -3.98) * mm, "radius": 1 * mm});
            skCircle(sketch, "E3.0.64.2", {"center": v(105.8, -0.98) * mm, "radius": 1 * mm});
            skCircle(sketch, "E3.0.64.3", {"center": v(105.8, 2.02) * mm, "radius": 1 * mm});
            skCircle(sketch, "E3.0.64.4", {"center": v(105.8, 5.02) * mm, "radius": 1 * mm});
            skCircle(sketch, "E3.0.64.5", {"center": v(105.8, 8.02) * mm, "radius": 1 * mm});
            skCircle(sketch, "E3.0.64.6", {"center": v(105.8, 11.02) * mm, "radius": 1 * mm});
            skCircle(sketch, "E3.0.64.7", {"center": v(105.8, 14.02) * mm, "radius": 1 * mm});
            skCircle(sketch, "E3.0.64.8", {"center": v(105.8, 17.02) * mm, "radius": 1 * mm});
            skCircle(sketch, "E3.0.64.9", {"center": v(105.8, 20.02) * mm, "radius": 1 * mm});
            skCircle(sketch, "E3.0.64.10", {"center": v(105.8, 23.02) * mm, "radius": 1 * mm});
            skCircle(sketch, "E3.0.64.11", {"center": v(105.8, 26.02) * mm, "radius": 1 * mm});
            skCircle(sketch, "E3.0.65.0", {"center": v(108.93, -6.98) * mm, "radius": 1 * mm});
            skCircle(sketch, "E3.0.65.1", {"center": v(108.93, -3.98) * mm, "radius": 1 * mm});
            skCircle(sketch, "E3.0.65.2", {"center": v(108.93, -0.98) * mm, "radius": 1 * mm});
            skCircle(sketch, "E3.0.65.3", {"center": v(108.93, 2.02) * mm, "radius": 1 * mm});
            skCircle(sketch, "E3.0.65.4", {"center": v(108.93, 5.02) * mm, "radius": 1 * mm});
            skCircle(sketch, "E3.0.65.5", {"center": v(108.93, 8.02) * mm, "radius": 1 * mm});
            skCircle(sketch, "E3.0.65.6", {"center": v(108.93, 11.02) * mm, "radius": 1 * mm});
            skCircle(sketch, "E3.0.65.7", {"center": v(108.93, 14.02) * mm, "radius": 1 * mm});
            skCircle(sketch, "E3.0.65.8", {"center": v(108.93, 17.02) * mm, "radius": 1 * mm});
            skCircle(sketch, "E3.0.65.9", {"center": v(108.93, 20.02) * mm, "radius": 1 * mm});
            skCircle(sketch, "E3.0.65.10", {"center": v(108.93, 23.02) * mm, "radius": 1 * mm});
            skCircle(sketch, "E3.0.65.11", {"center": v(108.93, 26.02) * mm, "radius": 1 * mm});
            skCircle(sketch, "E3.0.66.0", {"center": v(112.05, -6.98) * mm, "radius": 1 * mm});
            skCircle(sketch, "E3.0.66.1", {"center": v(112.05, -3.98) * mm, "radius": 1 * mm});
            skCircle(sketch, "E3.0.66.2", {"center": v(112.05, -0.98) * mm, "radius": 1 * mm});
            skCircle(sketch, "E3.0.66.3", {"center": v(112.05, 2.02) * mm, "radius": 1 * mm});
            skCircle(sketch, "E3.0.66.4", {"center": v(112.05, 5.02) * mm, "radius": 1 * mm});
            skCircle(sketch, "E3.0.66.5", {"center": v(112.05, 8.02) * mm, "radius": 1 * mm});
            skCircle(sketch, "E3.0.66.6", {"center": v(112.05, 11.02) * mm, "radius": 1 * mm});
            skCircle(sketch, "E3.0.66.7", {"center": v(112.05, 14.02) * mm, "radius": 1 * mm});
            skCircle(sketch, "E3.0.66.8", {"center": v(112.05, 17.02) * mm, "radius": 1 * mm});
            skCircle(sketch, "E3.0.66.9", {"center": v(112.05, 20.02) * mm, "radius": 1 * mm});
            skCircle(sketch, "E3.0.66.10", {"center": v(112.05, 23.02) * mm, "radius": 1 * mm});
            skCircle(sketch, "E3.0.66.11", {"center": v(112.05, 26.02) * mm, "radius": 1 * mm});
            skCircle(sketch, "E3.0.67.0", {"center": v(115.17, -6.98) * mm, "radius": 1 * mm});
            skCircle(sketch, "E3.0.67.1", {"center": v(115.17, -3.98) * mm, "radius": 1 * mm});
            skCircle(sketch, "E3.0.67.2", {"center": v(115.17, -0.98) * mm, "radius": 1 * mm});
            skCircle(sketch, "E3.0.67.3", {"center": v(115.17, 2.02) * mm, "radius": 1 * mm});
            skCircle(sketch, "E3.0.67.4", {"center": v(115.17, 5.02) * mm, "radius": 1 * mm});
            skCircle(sketch, "E3.0.67.5", {"center": v(115.17, 8.02) * mm, "radius": 1 * mm});
            skCircle(sketch, "E3.0.67.6", {"center": v(115.17, 11.02) * mm, "radius": 1 * mm});
            skCircle(sketch, "E3.0.67.7", {"center": v(115.17, 14.02) * mm, "radius": 1 * mm});
            skCircle(sketch, "E3.0.67.8", {"center": v(115.17, 17.02) * mm, "radius": 1 * mm});
            skCircle(sketch, "E3.0.67.9", {"center": v(115.17, 20.02) * mm, "radius": 1 * mm});
            skCircle(sketch, "E3.0.67.10", {"center": v(115.17, 23.02) * mm, "radius": 1 * mm});
            skCircle(sketch, "E3.0.67.11", {"center": v(115.17, 26.02) * mm, "radius": 1 * mm});
            skCircle(sketch, "E3.0.68.0", {"center": v(118.29, -6.98) * mm, "radius": 1 * mm});
            skCircle(sketch, "E3.0.68.1", {"center": v(118.29, -3.98) * mm, "radius": 1 * mm});
            skCircle(sketch, "E3.0.68.2", {"center": v(118.29, -0.98) * mm, "radius": 1 * mm});
            skCircle(sketch, "E3.0.68.3", {"center": v(118.29, 2.02) * mm, "radius": 1 * mm});
            skCircle(sketch, "E3.0.68.4", {"center": v(118.29, 5.02) * mm, "radius": 1 * mm});
            skCircle(sketch, "E3.0.68.5", {"center": v(118.29, 8.02) * mm, "radius": 1 * mm});
            skCircle(sketch, "E3.0.68.6", {"center": v(118.29, 11.02) * mm, "radius": 1 * mm});
            skCircle(sketch, "E3.0.68.7", {"center": v(118.29, 14.02) * mm, "radius": 1 * mm});
            skCircle(sketch, "E3.0.68.8", {"center": v(118.29, 17.02) * mm, "radius": 1 * mm});
            skCircle(sketch, "E3.0.68.9", {"center": v(118.29, 20.02) * mm, "radius": 1 * mm});
            skCircle(sketch, "E3.0.68.10", {"center": v(118.29, 23.02) * mm, "radius": 1 * mm});
            skCircle(sketch, "E3.0.68.11", {"center": v(118.29, 26.02) * mm, "radius": 1 * mm});
            skCircle(sketch, "E3.0.69.0", {"center": v(121.4, -6.98) * mm, "radius": 1 * mm});
            skCircle(sketch, "E3.0.69.1", {"center": v(121.4, -3.98) * mm, "radius": 1 * mm});
            skCircle(sketch, "E3.0.69.2", {"center": v(121.4, -0.98) * mm, "radius": 1 * mm});
            skCircle(sketch, "E3.0.69.3", {"center": v(121.4, 2.02) * mm, "radius": 1 * mm});
            skCircle(sketch, "E3.0.69.4", {"center": v(121.4, 5.02) * mm, "radius": 1 * mm});
            skCircle(sketch, "E3.0.69.5", {"center": v(121.4, 8.02) * mm, "radius": 1 * mm});
            skCircle(sketch, "E3.0.69.6", {"center": v(121.4, 11.02) * mm, "radius": 1 * mm});
            skCircle(sketch, "E3.0.69.7", {"center": v(121.4, 14.02) * mm, "radius": 1 * mm});
            skCircle(sketch, "E3.0.69.8", {"center": v(121.4, 17.02) * mm, "radius": 1 * mm});
            skCircle(sketch, "E3.0.69.9", {"center": v(121.4, 20.02) * mm, "radius": 1 * mm});
            skCircle(sketch, "E3.0.69.10", {"center": v(121.4, 23.02) * mm, "radius": 1 * mm});
            skCircle(sketch, "E3.0.69.11", {"center": v(121.4, 26.02) * mm, "radius": 1 * mm});
            skCircle(sketch, "E3.0.70.0", {"center": v(124.53, -6.98) * mm, "radius": 1 * mm});
            skCircle(sketch, "E3.0.70.1", {"center": v(124.53, -3.98) * mm, "radius": 1 * mm});
            skCircle(sketch, "E3.0.70.2", {"center": v(124.53, -0.98) * mm, "radius": 1 * mm});
            skCircle(sketch, "E3.0.70.3", {"center": v(124.53, 2.02) * mm, "radius": 1 * mm});
            skCircle(sketch, "E3.0.70.4", {"center": v(124.53, 5.02) * mm, "radius": 1 * mm});
            skCircle(sketch, "E3.0.70.5", {"center": v(124.53, 8.02) * mm, "radius": 1 * mm});
            skCircle(sketch, "E3.0.70.6", {"center": v(124.53, 11.02) * mm, "radius": 1 * mm});
            skCircle(sketch, "E3.0.70.7", {"center": v(124.53, 14.02) * mm, "radius": 1 * mm});
            skCircle(sketch, "E3.0.70.8", {"center": v(124.53, 17.02) * mm, "radius": 1 * mm});
            skCircle(sketch, "E3.0.70.9", {"center": v(124.53, 20.02) * mm, "radius": 1 * mm});
            skCircle(sketch, "E3.0.70.10", {"center": v(124.53, 23.02) * mm, "radius": 1 * mm});
            skCircle(sketch, "E3.0.70.11", {"center": v(124.53, 26.02) * mm, "radius": 1 * mm});
            skCircle(sketch, "E3.0.71.0", {"center": v(127.65, -6.98) * mm, "radius": 1 * mm});
            skCircle(sketch, "E3.0.71.1", {"center": v(127.65, -3.98) * mm, "radius": 1 * mm});
            skCircle(sketch, "E3.0.71.2", {"center": v(127.65, -0.98) * mm, "radius": 1 * mm});
            skCircle(sketch, "E3.0.71.3", {"center": v(127.65, 2.02) * mm, "radius": 1 * mm});
            skCircle(sketch, "E3.0.71.4", {"center": v(127.65, 5.02) * mm, "radius": 1 * mm});
            skCircle(sketch, "E3.0.71.5", {"center": v(127.65, 8.02) * mm, "radius": 1 * mm});
            skCircle(sketch, "E3.0.71.6", {"center": v(127.65, 11.02) * mm, "radius": 1 * mm});
            skCircle(sketch, "E3.0.71.7", {"center": v(127.65, 14.02) * mm, "radius": 1 * mm});
            skCircle(sketch, "E3.0.71.8", {"center": v(127.65, 17.02) * mm, "radius": 1 * mm});
            skCircle(sketch, "E3.0.71.9", {"center": v(127.65, 20.02) * mm, "radius": 1 * mm});
            skCircle(sketch, "E3.0.71.10", {"center": v(127.65, 23.02) * mm, "radius": 1 * mm});
            skCircle(sketch, "E3.0.71.11", {"center": v(127.65, 26.02) * mm, "radius": 1 * mm});
            skCircle(sketch, "E3.0.72.0", {"center": v(130.77, -6.98) * mm, "radius": 1 * mm});
            skCircle(sketch, "E3.0.72.1", {"center": v(130.77, -3.98) * mm, "radius": 1 * mm});
            skCircle(sketch, "E3.0.72.2", {"center": v(130.77, -0.98) * mm, "radius": 1 * mm});
            skCircle(sketch, "E3.0.72.3", {"center": v(130.77, 2.02) * mm, "radius": 1 * mm});
            skCircle(sketch, "E3.0.72.4", {"center": v(130.77, 5.02) * mm, "radius": 1 * mm});
            skCircle(sketch, "E3.0.72.5", {"center": v(130.77, 8.02) * mm, "radius": 1 * mm});
            skCircle(sketch, "E3.0.72.6", {"center": v(130.77, 11.02) * mm, "radius": 1 * mm});
            skCircle(sketch, "E3.0.72.7", {"center": v(130.77, 14.02) * mm, "radius": 1 * mm});
            skCircle(sketch, "E3.0.72.8", {"center": v(130.77, 17.02) * mm, "radius": 1 * mm});
            skCircle(sketch, "E3.0.72.9", {"center": v(130.77, 20.02) * mm, "radius": 1 * mm});
            skCircle(sketch, "E3.0.72.10", {"center": v(130.77, 23.02) * mm, "radius": 1 * mm});
            skCircle(sketch, "E3.0.72.11", {"center": v(130.77, 26.02) * mm, "radius": 1 * mm});
            skCircle(sketch, "E3.0.73.0", {"center": v(133.89, -6.98) * mm, "radius": 1 * mm});
            skCircle(sketch, "E3.0.73.1", {"center": v(133.89, -3.98) * mm, "radius": 1 * mm});
            skCircle(sketch, "E3.0.73.2", {"center": v(133.89, -0.98) * mm, "radius": 1 * mm});
            skCircle(sketch, "E3.0.73.3", {"center": v(133.89, 2.02) * mm, "radius": 1 * mm});
            skCircle(sketch, "E3.0.73.4", {"center": v(133.89, 5.02) * mm, "radius": 1 * mm});
            skCircle(sketch, "E3.0.73.5", {"center": v(133.89, 8.02) * mm, "radius": 1 * mm});
            skCircle(sketch, "E3.0.73.6", {"center": v(133.89, 11.02) * mm, "radius": 1 * mm});
            skCircle(sketch, "E3.0.73.7", {"center": v(133.89, 14.02) * mm, "radius": 1 * mm});
            skCircle(sketch, "E3.0.73.8", {"center": v(133.89, 17.02) * mm, "radius": 1 * mm});
            skCircle(sketch, "E3.0.73.9", {"center": v(133.89, 20.02) * mm, "radius": 1 * mm});
            skCircle(sketch, "E3.0.73.10", {"center": v(133.89, 23.02) * mm, "radius": 1 * mm});
            skCircle(sketch, "E3.0.73.11", {"center": v(133.89, 26.02) * mm, "radius": 1 * mm});
            skCircle(sketch, "E3.0.74.0", {"center": v(137, -6.98) * mm, "radius": 1 * mm});
            skCircle(sketch, "E3.0.74.1", {"center": v(137, -3.98) * mm, "radius": 1 * mm});
            skCircle(sketch, "E3.0.74.2", {"center": v(137, -0.98) * mm, "radius": 1 * mm});
            skCircle(sketch, "E3.0.74.3", {"center": v(137, 2.02) * mm, "radius": 1 * mm});
            skCircle(sketch, "E3.0.74.4", {"center": v(137, 5.02) * mm, "radius": 1 * mm});
            skCircle(sketch, "E3.0.74.5", {"center": v(137, 8.02) * mm, "radius": 1 * mm});
            skCircle(sketch, "E3.0.74.6", {"center": v(137, 11.02) * mm, "radius": 1 * mm});
            skCircle(sketch, "E3.0.74.7", {"center": v(137, 14.02) * mm, "radius": 1 * mm});
            skCircle(sketch, "E3.0.74.8", {"center": v(137, 17.02) * mm, "radius": 1 * mm});
            skCircle(sketch, "E3.0.74.9", {"center": v(137, 20.02) * mm, "radius": 1 * mm});
            skCircle(sketch, "E3.0.74.10", {"center": v(137, 23.02) * mm, "radius": 1 * mm});
            skCircle(sketch, "E3.0.74.11", {"center": v(137, 26.02) * mm, "radius": 1 * mm});
            skCircle(sketch, "E3.0.75.0", {"center": v(140.13, -6.98) * mm, "radius": 1 * mm});
            skCircle(sketch, "E3.0.75.1", {"center": v(140.13, -3.98) * mm, "radius": 1 * mm});
            skCircle(sketch, "E3.0.75.2", {"center": v(140.13, -0.98) * mm, "radius": 1 * mm});
            skCircle(sketch, "E3.0.75.3", {"center": v(140.13, 2.02) * mm, "radius": 1 * mm});
            skCircle(sketch, "E3.0.75.4", {"center": v(140.13, 5.02) * mm, "radius": 1 * mm});
            skCircle(sketch, "E3.0.75.5", {"center": v(140.13, 8.02) * mm, "radius": 1 * mm});
            skCircle(sketch, "E3.0.75.6", {"center": v(140.13, 11.02) * mm, "radius": 1 * mm});
            skCircle(sketch, "E3.0.75.7", {"center": v(140.13, 14.02) * mm, "radius": 1 * mm});
            skCircle(sketch, "E3.0.75.8", {"center": v(140.13, 17.02) * mm, "radius": 1 * mm});
            skCircle(sketch, "E3.0.75.9", {"center": v(140.13, 20.02) * mm, "radius": 1 * mm});
            skCircle(sketch, "E3.0.75.10", {"center": v(140.13, 23.02) * mm, "radius": 1 * mm});
            skCircle(sketch, "E3.0.75.11", {"center": v(140.13, 26.02) * mm, "radius": 1 * mm});
            skCircle(sketch, "E3.0.76.0", {"center": v(143.25, -6.98) * mm, "radius": 1 * mm});
            skCircle(sketch, "E3.0.76.1", {"center": v(143.25, -3.98) * mm, "radius": 1 * mm});
            skCircle(sketch, "E3.0.76.2", {"center": v(143.25, -0.98) * mm, "radius": 1 * mm});
            skCircle(sketch, "E3.0.76.3", {"center": v(143.25, 2.02) * mm, "radius": 1 * mm});
            skCircle(sketch, "E3.0.76.4", {"center": v(143.25, 5.02) * mm, "radius": 1 * mm});
            skCircle(sketch, "E3.0.76.5", {"center": v(143.25, 8.02) * mm, "radius": 1 * mm});
            skCircle(sketch, "E3.0.76.6", {"center": v(143.25, 11.02) * mm, "radius": 1 * mm});
            skCircle(sketch, "E3.0.76.7", {"center": v(143.25, 14.02) * mm, "radius": 1 * mm});
            skCircle(sketch, "E3.0.76.8", {"center": v(143.25, 17.02) * mm, "radius": 1 * mm});
            skCircle(sketch, "E3.0.76.9", {"center": v(143.25, 20.02) * mm, "radius": 1 * mm});
            skCircle(sketch, "E3.0.76.10", {"center": v(143.25, 23.02) * mm, "radius": 1 * mm});
            skCircle(sketch, "E3.0.76.11", {"center": v(143.25, 26.02) * mm, "radius": 1 * mm});
            skCircle(sketch, "E3.0.77.0", {"center": v(146.37, -6.98) * mm, "radius": 1 * mm});
            skCircle(sketch, "E3.0.77.1", {"center": v(146.37, -3.98) * mm, "radius": 1 * mm});
            skCircle(sketch, "E3.0.77.2", {"center": v(146.37, -0.98) * mm, "radius": 1 * mm});
            skCircle(sketch, "E3.0.77.3", {"center": v(146.37, 2.02) * mm, "radius": 1 * mm});
            skCircle(sketch, "E3.0.77.4", {"center": v(146.37, 5.02) * mm, "radius": 1 * mm});
            skCircle(sketch, "E3.0.77.5", {"center": v(146.37, 8.02) * mm, "radius": 1 * mm});
            skCircle(sketch, "E3.0.77.6", {"center": v(146.37, 11.02) * mm, "radius": 1 * mm});
            skCircle(sketch, "E3.0.77.7", {"center": v(146.37, 14.02) * mm, "radius": 1 * mm});
            skCircle(sketch, "E3.0.77.8", {"center": v(146.37, 17.02) * mm, "radius": 1 * mm});
            skCircle(sketch, "E3.0.77.9", {"center": v(146.37, 20.02) * mm, "radius": 1 * mm});
            skCircle(sketch, "E3.0.77.10", {"center": v(146.37, 23.02) * mm, "radius": 1 * mm});
            skCircle(sketch, "E3.0.77.11", {"center": v(146.37, 26.02) * mm, "radius": 1 * mm});
            skCircle(sketch, "E3.0.78.0", {"center": v(149.49, -6.98) * mm, "radius": 1 * mm});
            skCircle(sketch, "E3.0.78.1", {"center": v(149.49, -3.98) * mm, "radius": 1 * mm});
            skCircle(sketch, "E3.0.78.2", {"center": v(149.49, -0.98) * mm, "radius": 1 * mm});
            skCircle(sketch, "E3.0.78.3", {"center": v(149.49, 2.02) * mm, "radius": 1 * mm});
            skCircle(sketch, "E3.0.78.4", {"center": v(149.49, 5.02) * mm, "radius": 1 * mm});
            skCircle(sketch, "E3.0.78.5", {"center": v(149.49, 8.02) * mm, "radius": 1 * mm});
            skCircle(sketch, "E3.0.78.6", {"center": v(149.49, 11.02) * mm, "radius": 1 * mm});
            skCircle(sketch, "E3.0.78.7", {"center": v(149.49, 14.02) * mm, "radius": 1 * mm});
            skCircle(sketch, "E3.0.78.8", {"center": v(149.49, 17.02) * mm, "radius": 1 * mm});
            skCircle(sketch, "E3.0.78.9", {"center": v(149.49, 20.02) * mm, "radius": 1 * mm});
            skCircle(sketch, "E3.0.78.10", {"center": v(149.49, 23.02) * mm, "radius": 1 * mm});
            skCircle(sketch, "E3.0.78.11", {"center": v(149.49, 26.02) * mm, "radius": 1 * mm});
            skCircle(sketch, "E3.0.79.0", {"center": v(152.6, -6.98) * mm, "radius": 1 * mm});
            skCircle(sketch, "E3.0.79.1", {"center": v(152.6, -3.98) * mm, "radius": 1 * mm});
            skCircle(sketch, "E3.0.79.2", {"center": v(152.6, -0.98) * mm, "radius": 1 * mm});
            skCircle(sketch, "E3.0.79.3", {"center": v(152.6, 2.02) * mm, "radius": 1 * mm});
            skCircle(sketch, "E3.0.79.4", {"center": v(152.6, 5.02) * mm, "radius": 1 * mm});
            skCircle(sketch, "E3.0.79.5", {"center": v(152.6, 8.02) * mm, "radius": 1 * mm});
            skCircle(sketch, "E3.0.79.6", {"center": v(152.6, 11.02) * mm, "radius": 1 * mm});
            skCircle(sketch, "E3.0.79.7", {"center": v(152.6, 14.02) * mm, "radius": 1 * mm});
            skCircle(sketch, "E3.0.79.8", {"center": v(152.6, 17.02) * mm, "radius": 1 * mm});
            skCircle(sketch, "E3.0.79.9", {"center": v(152.6, 20.02) * mm, "radius": 1 * mm});
            skCircle(sketch, "E3.0.79.10", {"center": v(152.6, 23.02) * mm, "radius": 1 * mm});
            skCircle(sketch, "E3.0.79.11", {"center": v(152.6, 26.02) * mm, "radius": 1 * mm});
            skCircle(sketch, "E3.0.80.0", {"center": v(155.73, -6.98) * mm, "radius": 1 * mm});
            skCircle(sketch, "E3.0.80.1", {"center": v(155.73, -3.98) * mm, "radius": 1 * mm});
            skCircle(sketch, "E3.0.80.2", {"center": v(155.73, -0.98) * mm, "radius": 1 * mm});
            skCircle(sketch, "E3.0.80.3", {"center": v(155.73, 2.02) * mm, "radius": 1 * mm});
            skCircle(sketch, "E3.0.80.4", {"center": v(155.73, 5.02) * mm, "radius": 1 * mm});
            skCircle(sketch, "E3.0.80.5", {"center": v(155.73, 8.02) * mm, "radius": 1 * mm});
            skCircle(sketch, "E3.0.80.6", {"center": v(155.73, 11.02) * mm, "radius": 1 * mm});
            skCircle(sketch, "E3.0.80.7", {"center": v(155.73, 14.02) * mm, "radius": 1 * mm});
            skCircle(sketch, "E3.0.80.8", {"center": v(155.73, 17.02) * mm, "radius": 1 * mm});
            skCircle(sketch, "E3.0.80.9", {"center": v(155.73, 20.02) * mm, "radius": 1 * mm});
            skCircle(sketch, "E3.0.80.10", {"center": v(155.73, 23.02) * mm, "radius": 1 * mm});
            skCircle(sketch, "E3.0.80.11", {"center": v(155.73, 26.02) * mm, "radius": 1 * mm});
            skCircle(sketch, "E3.0.81.0", {"center": v(158.85, -6.98) * mm, "radius": 1 * mm});
            skCircle(sketch, "E3.0.81.1", {"center": v(158.85, -3.98) * mm, "radius": 1 * mm});
            skCircle(sketch, "E3.0.81.2", {"center": v(158.85, -0.98) * mm, "radius": 1 * mm});
            skCircle(sketch, "E3.0.81.3", {"center": v(158.85, 2.02) * mm, "radius": 1 * mm});
            skCircle(sketch, "E3.0.81.4", {"center": v(158.85, 5.02) * mm, "radius": 1 * mm});
            skCircle(sketch, "E3.0.81.5", {"center": v(158.85, 8.02) * mm, "radius": 1 * mm});
            skCircle(sketch, "E3.0.81.6", {"center": v(158.85, 11.02) * mm, "radius": 1 * mm});
            skCircle(sketch, "E3.0.81.7", {"center": v(158.85, 14.02) * mm, "radius": 1 * mm});
            skCircle(sketch, "E3.0.81.8", {"center": v(158.85, 17.02) * mm, "radius": 1 * mm});
            skCircle(sketch, "E3.0.81.9", {"center": v(158.85, 20.02) * mm, "radius": 1 * mm});
            skCircle(sketch, "E3.0.81.10", {"center": v(158.85, 23.02) * mm, "radius": 1 * mm});
            skCircle(sketch, "E3.0.81.11", {"center": v(158.85, 26.02) * mm, "radius": 1 * mm});
            skCircle(sketch, "E3.0.82.0", {"center": v(161.97, -6.98) * mm, "radius": 1 * mm});
            skCircle(sketch, "E3.0.82.1", {"center": v(161.97, -3.98) * mm, "radius": 1 * mm});
            skCircle(sketch, "E3.0.82.2", {"center": v(161.97, -0.98) * mm, "radius": 1 * mm});
            skCircle(sketch, "E3.0.82.3", {"center": v(161.97, 2.02) * mm, "radius": 1 * mm});
            skCircle(sketch, "E3.0.82.4", {"center": v(161.97, 5.02) * mm, "radius": 1 * mm});
            skCircle(sketch, "E3.0.82.5", {"center": v(161.97, 8.02) * mm, "radius": 1 * mm});
            skCircle(sketch, "E3.0.82.6", {"center": v(161.97, 11.02) * mm, "radius": 1 * mm});
            skCircle(sketch, "E3.0.82.7", {"center": v(161.97, 14.02) * mm, "radius": 1 * mm});
            skCircle(sketch, "E3.0.82.8", {"center": v(161.97, 17.02) * mm, "radius": 1 * mm});
            skCircle(sketch, "E3.0.82.9", {"center": v(161.97, 20.02) * mm, "radius": 1 * mm});
            skCircle(sketch, "E3.0.82.10", {"center": v(161.97, 23.02) * mm, "radius": 1 * mm});
            skCircle(sketch, "E3.0.82.11", {"center": v(161.97, 26.02) * mm, "radius": 1 * mm});
            skCircle(sketch, "E3.0.83.0", {"center": v(165.09, -6.98) * mm, "radius": 1 * mm});
            skCircle(sketch, "E3.0.83.1", {"center": v(165.09, -3.98) * mm, "radius": 1 * mm});
            skCircle(sketch, "E3.0.83.2", {"center": v(165.09, -0.98) * mm, "radius": 1 * mm});
            skCircle(sketch, "E3.0.83.3", {"center": v(165.09, 2.02) * mm, "radius": 1 * mm});
            skCircle(sketch, "E3.0.83.4", {"center": v(165.09, 5.02) * mm, "radius": 1 * mm});
            skCircle(sketch, "E3.0.83.5", {"center": v(165.09, 8.02) * mm, "radius": 1 * mm});
            skCircle(sketch, "E3.0.83.6", {"center": v(165.09, 11.02) * mm, "radius": 1 * mm});
            skCircle(sketch, "E3.0.83.7", {"center": v(165.09, 14.02) * mm, "radius": 1 * mm});
            skCircle(sketch, "E3.0.83.8", {"center": v(165.09, 17.02) * mm, "radius": 1 * mm});
            skCircle(sketch, "E3.0.83.9", {"center": v(165.09, 20.02) * mm, "radius": 1 * mm});
            skCircle(sketch, "E3.0.83.10", {"center": v(165.09, 23.02) * mm, "radius": 1 * mm});
            skCircle(sketch, "E3.0.83.11", {"center": v(165.09, 26.02) * mm, "radius": 1 * mm});
            skCircle(sketch, "E3.0.84.0", {"center": v(168.2, -6.98) * mm, "radius": 1 * mm});
            skCircle(sketch, "E3.0.84.1", {"center": v(168.2, -3.98) * mm, "radius": 1 * mm});
            skCircle(sketch, "E3.0.84.2", {"center": v(168.2, -0.98) * mm, "radius": 1 * mm});
            skCircle(sketch, "E3.0.84.3", {"center": v(168.2, 2.02) * mm, "radius": 1 * mm});
            skCircle(sketch, "E3.0.84.4", {"center": v(168.2, 5.02) * mm, "radius": 1 * mm});
            skCircle(sketch, "E3.0.84.5", {"center": v(168.2, 8.02) * mm, "radius": 1 * mm});
            skCircle(sketch, "E3.0.84.6", {"center": v(168.2, 11.02) * mm, "radius": 1 * mm});
            skCircle(sketch, "E3.0.84.7", {"center": v(168.2, 14.02) * mm, "radius": 1 * mm});
            skCircle(sketch, "E3.0.84.8", {"center": v(168.2, 17.02) * mm, "radius": 1 * mm});
            skCircle(sketch, "E3.0.84.9", {"center": v(168.2, 20.02) * mm, "radius": 1 * mm});
            skCircle(sketch, "E3.0.84.10", {"center": v(168.2, 23.02) * mm, "radius": 1 * mm});
            skCircle(sketch, "E3.0.84.11", {"center": v(168.2, 26.02) * mm, "radius": 1 * mm});
            skCircle(sketch, "E3.0.85.0", {"center": v(171.33, -6.98) * mm, "radius": 1 * mm});
            skCircle(sketch, "E3.0.85.1", {"center": v(171.33, -3.98) * mm, "radius": 1 * mm});
            skCircle(sketch, "E3.0.85.2", {"center": v(171.33, -0.98) * mm, "radius": 1 * mm});
            skCircle(sketch, "E3.0.85.3", {"center": v(171.33, 2.02) * mm, "radius": 1 * mm});
            skCircle(sketch, "E3.0.85.4", {"center": v(171.33, 5.02) * mm, "radius": 1 * mm});
            skCircle(sketch, "E3.0.85.5", {"center": v(171.33, 8.02) * mm, "radius": 1 * mm});
            skCircle(sketch, "E3.0.85.6", {"center": v(171.33, 11.02) * mm, "radius": 1 * mm});
            skCircle(sketch, "E3.0.85.7", {"center": v(171.33, 14.02) * mm, "radius": 1 * mm});
            skCircle(sketch, "E3.0.85.8", {"center": v(171.33, 17.02) * mm, "radius": 1 * mm});
            skCircle(sketch, "E3.0.85.9", {"center": v(171.33, 20.02) * mm, "radius": 1 * mm});
            skCircle(sketch, "E3.0.85.10", {"center": v(171.33, 23.02) * mm, "radius": 1 * mm});
            skCircle(sketch, "E3.0.85.11", {"center": v(171.33, 26.02) * mm, "radius": 1 * mm});
            skCircle(sketch, "E3.0.86.0", {"center": v(174.45, -6.98) * mm, "radius": 1 * mm});
            skCircle(sketch, "E3.0.86.1", {"center": v(174.45, -3.98) * mm, "radius": 1 * mm});
            skCircle(sketch, "E3.0.86.2", {"center": v(174.45, -0.98) * mm, "radius": 1 * mm});
            skCircle(sketch, "E3.0.86.3", {"center": v(174.45, 2.02) * mm, "radius": 1 * mm});
            skCircle(sketch, "E3.0.86.4", {"center": v(174.45, 5.02) * mm, "radius": 1 * mm});
            skCircle(sketch, "E3.0.86.5", {"center": v(174.45, 8.02) * mm, "radius": 1 * mm});
            skCircle(sketch, "E3.0.86.6", {"center": v(174.45, 11.02) * mm, "radius": 1 * mm});
            skCircle(sketch, "E3.0.86.7", {"center": v(174.45, 14.02) * mm, "radius": 1 * mm});
            skCircle(sketch, "E3.0.86.8", {"center": v(174.45, 17.02) * mm, "radius": 1 * mm});
            skCircle(sketch, "E3.0.86.9", {"center": v(174.45, 20.02) * mm, "radius": 1 * mm});
            skCircle(sketch, "E3.0.86.10", {"center": v(174.45, 23.02) * mm, "radius": 1 * mm});
            skCircle(sketch, "E3.0.86.11", {"center": v(174.45, 26.02) * mm, "radius": 1 * mm});
            skCircle(sketch, "E3.0.87.0", {"center": v(177.57, -6.98) * mm, "radius": 1 * mm});
            skCircle(sketch, "E3.0.87.1", {"center": v(177.57, -3.98) * mm, "radius": 1 * mm});
            skCircle(sketch, "E3.0.87.2", {"center": v(177.57, -0.98) * mm, "radius": 1 * mm});
            skCircle(sketch, "E3.0.87.3", {"center": v(177.57, 2.02) * mm, "radius": 1 * mm});
            skCircle(sketch, "E3.0.87.4", {"center": v(177.57, 5.02) * mm, "radius": 1 * mm});
            skCircle(sketch, "E3.0.87.5", {"center": v(177.57, 8.02) * mm, "radius": 1 * mm});
            skCircle(sketch, "E3.0.87.6", {"center": v(177.57, 11.02) * mm, "radius": 1 * mm});
            skCircle(sketch, "E3.0.87.7", {"center": v(177.57, 14.02) * mm, "radius": 1 * mm});
            skCircle(sketch, "E3.0.87.8", {"center": v(177.57, 17.02) * mm, "radius": 1 * mm});
            skCircle(sketch, "E3.0.87.9", {"center": v(177.57, 20.02) * mm, "radius": 1 * mm});
            skCircle(sketch, "E3.0.87.10", {"center": v(177.57, 23.02) * mm, "radius": 1 * mm});
            skCircle(sketch, "E3.0.87.11", {"center": v(177.57, 26.02) * mm, "radius": 1 * mm});
            skCircle(sketch, "E3.0.88.0", {"center": v(180.69, -6.98) * mm, "radius": 1 * mm});
            skCircle(sketch, "E3.0.88.1", {"center": v(180.69, -3.98) * mm, "radius": 1 * mm});
            skCircle(sketch, "E3.0.88.2", {"center": v(180.69, -0.98) * mm, "radius": 1 * mm});
            skCircle(sketch, "E3.0.88.3", {"center": v(180.69, 2.02) * mm, "radius": 1 * mm});
            skCircle(sketch, "E3.0.88.4", {"center": v(180.69, 5.02) * mm, "radius": 1 * mm});
            skCircle(sketch, "E3.0.88.5", {"center": v(180.69, 8.02) * mm, "radius": 1 * mm});
            skCircle(sketch, "E3.0.88.6", {"center": v(180.69, 11.02) * mm, "radius": 1 * mm});
            skCircle(sketch, "E3.0.88.7", {"center": v(180.69, 14.02) * mm, "radius": 1 * mm});
            skCircle(sketch, "E3.0.88.8", {"center": v(180.69, 17.02) * mm, "radius": 1 * mm});
            skCircle(sketch, "E3.0.88.9", {"center": v(180.69, 20.02) * mm, "radius": 1 * mm});
            skCircle(sketch, "E3.0.88.10", {"center": v(180.69, 23.02) * mm, "radius": 1 * mm});
            skCircle(sketch, "E3.0.88.11", {"center": v(180.69, 26.02) * mm, "radius": 1 * mm});
            skCircle(sketch, "E3.0.89.0", {"center": v(183.8, -6.98) * mm, "radius": 1 * mm});
            skCircle(sketch, "E3.0.89.1", {"center": v(183.8, -3.98) * mm, "radius": 1 * mm});
            skCircle(sketch, "E3.0.89.2", {"center": v(183.8, -0.98) * mm, "radius": 1 * mm});
            skCircle(sketch, "E3.0.89.3", {"center": v(183.8, 2.02) * mm, "radius": 1 * mm});
            skCircle(sketch, "E3.0.89.4", {"center": v(183.8, 5.02) * mm, "radius": 1 * mm});
            skCircle(sketch, "E3.0.89.5", {"center": v(183.8, 8.02) * mm, "radius": 1 * mm});
            skCircle(sketch, "E3.0.89.6", {"center": v(183.8, 11.02) * mm, "radius": 1 * mm});
            skCircle(sketch, "E3.0.89.7", {"center": v(183.8, 14.02) * mm, "radius": 1 * mm});
            skCircle(sketch, "E3.0.89.8", {"center": v(183.8, 17.02) * mm, "radius": 1 * mm});
            skCircle(sketch, "E3.0.89.9", {"center": v(183.8, 20.02) * mm, "radius": 1 * mm});
            skCircle(sketch, "E3.0.89.10", {"center": v(183.8, 23.02) * mm, "radius": 1 * mm});
            skCircle(sketch, "E3.0.89.11", {"center": v(183.8, 26.02) * mm, "radius": 1 * mm});
            skCircle(sketch, "E3.0.90.0", {"center": v(186.93, -6.98) * mm, "radius": 1 * mm});
            skCircle(sketch, "E3.0.90.1", {"center": v(186.93, -3.98) * mm, "radius": 1 * mm});
            skCircle(sketch, "E3.0.90.2", {"center": v(186.93, -0.98) * mm, "radius": 1 * mm});
            skCircle(sketch, "E3.0.90.3", {"center": v(186.93, 2.02) * mm, "radius": 1 * mm});
            skCircle(sketch, "E3.0.90.4", {"center": v(186.93, 5.02) * mm, "radius": 1 * mm});
            skCircle(sketch, "E3.0.90.5", {"center": v(186.93, 8.02) * mm, "radius": 1 * mm});
            skCircle(sketch, "E3.0.90.6", {"center": v(186.93, 11.02) * mm, "radius": 1 * mm});
            skCircle(sketch, "E3.0.90.7", {"center": v(186.93, 14.02) * mm, "radius": 1 * mm});
            skCircle(sketch, "E3.0.90.8", {"center": v(186.93, 17.02) * mm, "radius": 1 * mm});
            skCircle(sketch, "E3.0.90.9", {"center": v(186.93, 20.02) * mm, "radius": 1 * mm});
            skCircle(sketch, "E3.0.90.10", {"center": v(186.93, 23.02) * mm, "radius": 1 * mm});
            skCircle(sketch, "E3.0.90.11", {"center": v(186.93, 26.02) * mm, "radius": 1 * mm});
            skCircle(sketch, "E3.0.91.0", {"center": v(190.05, -6.98) * mm, "radius": 1 * mm});
            skCircle(sketch, "E3.0.91.1", {"center": v(190.05, -3.98) * mm, "radius": 1 * mm});
            skCircle(sketch, "E3.0.91.2", {"center": v(190.05, -0.98) * mm, "radius": 1 * mm});
            skCircle(sketch, "E3.0.91.3", {"center": v(190.05, 2.02) * mm, "radius": 1 * mm});
            skCircle(sketch, "E3.0.91.4", {"center": v(190.05, 5.02) * mm, "radius": 1 * mm});
            skCircle(sketch, "E3.0.91.5", {"center": v(190.05, 8.02) * mm, "radius": 1 * mm});
            skCircle(sketch, "E3.0.91.6", {"center": v(190.05, 11.02) * mm, "radius": 1 * mm});
            skCircle(sketch, "E3.0.91.7", {"center": v(190.05, 14.02) * mm, "radius": 1 * mm});
            skCircle(sketch, "E3.0.91.8", {"center": v(190.05, 17.02) * mm, "radius": 1 * mm});
            skCircle(sketch, "E3.0.91.9", {"center": v(190.05, 20.02) * mm, "radius": 1 * mm});
            skCircle(sketch, "E3.0.91.10", {"center": v(190.05, 23.02) * mm, "radius": 1 * mm});
            skCircle(sketch, "E3.0.91.11", {"center": v(190.05, 26.02) * mm, "radius": 1 * mm});
            skCircle(sketch, "E3.0.92.0", {"center": v(193.17, -6.98) * mm, "radius": 1 * mm});
            skCircle(sketch, "E3.0.92.1", {"center": v(193.17, -3.98) * mm, "radius": 1 * mm});
            skCircle(sketch, "E3.0.92.2", {"center": v(193.17, -0.98) * mm, "radius": 1 * mm});
            skCircle(sketch, "E3.0.92.3", {"center": v(193.17, 2.02) * mm, "radius": 1 * mm});
            skCircle(sketch, "E3.0.92.4", {"center": v(193.17, 5.02) * mm, "radius": 1 * mm});
            skCircle(sketch, "E3.0.92.5", {"center": v(193.17, 8.02) * mm, "radius": 1 * mm});
            skCircle(sketch, "E3.0.92.6", {"center": v(193.17, 11.02) * mm, "radius": 1 * mm});
            skCircle(sketch, "E3.0.92.7", {"center": v(193.17, 14.02) * mm, "radius": 1 * mm});
            skCircle(sketch, "E3.0.92.8", {"center": v(193.17, 17.02) * mm, "radius": 1 * mm});
            skCircle(sketch, "E3.0.92.9", {"center": v(193.17, 20.02) * mm, "radius": 1 * mm});
            skCircle(sketch, "E3.0.92.10", {"center": v(193.17, 23.02) * mm, "radius": 1 * mm});
            skCircle(sketch, "E3.0.92.11", {"center": v(193.17, 26.02) * mm, "radius": 1 * mm});
            skCircle(sketch, "E3.0.93.0", {"center": v(196.29, -6.98) * mm, "radius": 1 * mm});
            skCircle(sketch, "E3.0.93.1", {"center": v(196.29, -3.98) * mm, "radius": 1 * mm});
            skCircle(sketch, "E3.0.93.2", {"center": v(196.29, -0.98) * mm, "radius": 1 * mm});
            skCircle(sketch, "E3.0.93.3", {"center": v(196.29, 2.02) * mm, "radius": 1 * mm});
            skCircle(sketch, "E3.0.93.4", {"center": v(196.29, 5.02) * mm, "radius": 1 * mm});
            skCircle(sketch, "E3.0.93.5", {"center": v(196.29, 8.02) * mm, "radius": 1 * mm});
            skCircle(sketch, "E3.0.93.6", {"center": v(196.29, 11.02) * mm, "radius": 1 * mm});
            skCircle(sketch, "E3.0.93.7", {"center": v(196.29, 14.02) * mm, "radius": 1 * mm});
            skCircle(sketch, "E3.0.93.8", {"center": v(196.29, 17.02) * mm, "radius": 1 * mm});
            skCircle(sketch, "E3.0.93.9", {"center": v(196.29, 20.02) * mm, "radius": 1 * mm});
            skCircle(sketch, "E3.0.93.10", {"center": v(196.29, 23.02) * mm, "radius": 1 * mm});
            skCircle(sketch, "E3.0.93.11", {"center": v(196.29, 26.02) * mm, "radius": 1 * mm});
            skCircle(sketch, "E3.0.94.0", {"center": v(199.4, -6.98) * mm, "radius": 1 * mm});
            skCircle(sketch, "E3.0.94.1", {"center": v(199.4, -3.98) * mm, "radius": 1 * mm});
            skCircle(sketch, "E3.0.94.2", {"center": v(199.4, -0.98) * mm, "radius": 1 * mm});
            skCircle(sketch, "E3.0.94.3", {"center": v(199.4, 2.02) * mm, "radius": 1 * mm});
            skCircle(sketch, "E3.0.94.4", {"center": v(199.4, 5.02) * mm, "radius": 1 * mm});
            skCircle(sketch, "E3.0.94.5", {"center": v(199.4, 8.02) * mm, "radius": 1 * mm});
            skCircle(sketch, "E3.0.94.6", {"center": v(199.4, 11.02) * mm, "radius": 1 * mm});
            skCircle(sketch, "E3.0.94.7", {"center": v(199.4, 14.02) * mm, "radius": 1 * mm});
            skCircle(sketch, "E3.0.94.8", {"center": v(199.4, 17.02) * mm, "radius": 1 * mm});
            skCircle(sketch, "E3.0.94.9", {"center": v(199.4, 20.02) * mm, "radius": 1 * mm});
            skCircle(sketch, "E3.0.94.10", {"center": v(199.4, 23.02) * mm, "radius": 1 * mm});
            skCircle(sketch, "E3.0.94.11", {"center": v(199.4, 26.02) * mm, "radius": 1 * mm});
            skCircle(sketch, "E4.0.0.12", {"center": v(-93.87, 29.02) * mm, "radius": 1 * mm});
            skCircle(sketch, "E4.0.1.12", {"center": v(-90.75, 29.02) * mm, "radius": 1 * mm});
            skCircle(sketch, "E4.0.2.12", {"center": v(-87.63, 29.02) * mm, "radius": 1 * mm});
            skCircle(sketch, "E4.0.3.12", {"center": v(-84.51, 29.02) * mm, "radius": 1 * mm});
            skCircle(sketch, "E4.0.4.12", {"center": v(-81.4, 29.02) * mm, "radius": 1 * mm});
            skCircle(sketch, "E4.0.5.12", {"center": v(-78.27, 29.02) * mm, "radius": 1 * mm});
            skCircle(sketch, "E4.0.6.12", {"center": v(-75.15, 29.02) * mm, "radius": 1 * mm});
            skCircle(sketch, "E4.0.7.12", {"center": v(-72.03, 29.02) * mm, "radius": 1 * mm});
            skCircle(sketch, "E4.0.8.12", {"center": v(-68.91, 29.02) * mm, "radius": 1 * mm});
            skCircle(sketch, "E4.0.9.12", {"center": v(-65.8, 29.02) * mm, "radius": 1 * mm});
            skCircle(sketch, "E4.0.10.12", {"center": v(-62.67, 29.02) * mm, "radius": 1 * mm});
            skCircle(sketch, "E4.0.11.12", {"center": v(-59.55, 29.02) * mm, "radius": 1 * mm});
            skCircle(sketch, "E4.0.12.12", {"center": v(-56.43, 29.02) * mm, "radius": 1 * mm});
            skCircle(sketch, "E4.0.13.12", {"center": v(-53.31, 29.02) * mm, "radius": 1 * mm});
            skCircle(sketch, "E4.0.14.12", {"center": v(-50.2, 29.02) * mm, "radius": 1 * mm});
            skCircle(sketch, "E4.0.15.12", {"center": v(-47.07, 29.02) * mm, "radius": 1 * mm});
            skCircle(sketch, "E4.0.16.12", {"center": v(-43.95, 29.02) * mm, "radius": 1 * mm});
            skCircle(sketch, "E4.0.17.12", {"center": v(-40.83, 29.02) * mm, "radius": 1 * mm});
            skCircle(sketch, "E4.0.18.12", {"center": v(-37.71, 29.02) * mm, "radius": 1 * mm});
            skCircle(sketch, "E4.0.19.12", {"center": v(-34.6, 29.02) * mm, "radius": 1 * mm});
            skCircle(sketch, "E4.0.20.12", {"center": v(-31.47, 29.02) * mm, "radius": 1 * mm});
            skCircle(sketch, "E4.0.21.12", {"center": v(-28.35, 29.02) * mm, "radius": 1 * mm});
            skCircle(sketch, "E4.0.22.12", {"center": v(-25.23, 29.02) * mm, "radius": 1 * mm});
            skCircle(sketch, "E4.0.23.12", {"center": v(-22.11, 29.02) * mm, "radius": 1 * mm});
            skCircle(sketch, "E4.0.24.12", {"center": v(-19, 29.02) * mm, "radius": 1 * mm});
            skCircle(sketch, "E4.0.25.12", {"center": v(-15.87, 29.02) * mm, "radius": 1 * mm});
            skCircle(sketch, "E4.0.26.12", {"center": v(-12.75, 29.02) * mm, "radius": 1 * mm});
            skCircle(sketch, "E4.0.27.12", {"center": v(-9.63, 29.02) * mm, "radius": 1 * mm});
            skCircle(sketch, "E4.0.28.12", {"center": v(-6.51, 29.02) * mm, "radius": 1 * mm});
            skCircle(sketch, "E4.0.29.12", {"center": v(-3.4, 29.02) * mm, "radius": 1 * mm});
            skCircle(sketch, "E4.0.30.12", {"center": v(-0.27, 29.02) * mm, "radius": 1 * mm});
            skCircle(sketch, "E4.0.31.12", {"center": v(2.85, 29.02) * mm, "radius": 1 * mm});
            skCircle(sketch, "E4.0.32.12", {"center": v(5.97, 29.02) * mm, "radius": 1 * mm});
            skCircle(sketch, "E4.0.33.12", {"center": v(9.09, 29.02) * mm, "radius": 1 * mm});
            skCircle(sketch, "E4.0.34.12", {"center": v(12.2, 29.02) * mm, "radius": 1 * mm});
            skCircle(sketch, "E4.0.35.12", {"center": v(15.33, 29.02) * mm, "radius": 1 * mm});
            skCircle(sketch, "E4.0.36.12", {"center": v(18.45, 29.02) * mm, "radius": 1 * mm});
            skCircle(sketch, "E4.0.37.12", {"center": v(21.57, 29.02) * mm, "radius": 1 * mm});
            skCircle(sketch, "E4.0.38.12", {"center": v(24.69, 29.02) * mm, "radius": 1 * mm});
            skCircle(sketch, "E4.0.39.12", {"center": v(27.8, 29.02) * mm, "radius": 1 * mm});
            skCircle(sketch, "E4.0.40.12", {"center": v(30.93, 29.02) * mm, "radius": 1 * mm});
            skCircle(sketch, "E4.0.41.12", {"center": v(34.05, 29.02) * mm, "radius": 1 * mm});
            skCircle(sketch, "E4.0.42.12", {"center": v(37.17, 29.02) * mm, "radius": 1 * mm});
            skCircle(sketch, "E4.0.43.12", {"center": v(40.29, 29.02) * mm, "radius": 1 * mm});
            skCircle(sketch, "E4.0.44.12", {"center": v(43.4, 29.02) * mm, "radius": 1 * mm});
            skCircle(sketch, "E4.0.45.12", {"center": v(46.53, 29.02) * mm, "radius": 1 * mm});
            skCircle(sketch, "E4.0.46.12", {"center": v(49.65, 29.02) * mm, "radius": 1 * mm});
            skCircle(sketch, "E4.0.47.12", {"center": v(52.77, 29.02) * mm, "radius": 1 * mm});
            skCircle(sketch, "E4.0.48.12", {"center": v(55.89, 29.02) * mm, "radius": 1 * mm});
            skCircle(sketch, "E4.0.49.12", {"center": v(59, 29.02) * mm, "radius": 1 * mm});
            skCircle(sketch, "E4.0.50.12", {"center": v(62.13, 29.02) * mm, "radius": 1 * mm});
            skCircle(sketch, "E4.0.51.12", {"center": v(65.25, 29.02) * mm, "radius": 1 * mm});
            skCircle(sketch, "E4.0.52.12", {"center": v(68.37, 29.02) * mm, "radius": 1 * mm});
            skCircle(sketch, "E4.0.53.12", {"center": v(71.49, 29.02) * mm, "radius": 1 * mm});
            skCircle(sketch, "E4.0.54.12", {"center": v(74.6, 29.02) * mm, "radius": 1 * mm});
            skCircle(sketch, "E4.0.55.12", {"center": v(77.73, 29.02) * mm, "radius": 1 * mm});
            skCircle(sketch, "E4.0.56.12", {"center": v(80.85, 29.02) * mm, "radius": 1 * mm});
            skCircle(sketch, "E4.0.57.12", {"center": v(83.97, 29.02) * mm, "radius": 1 * mm});
            skCircle(sketch, "E4.0.58.12", {"center": v(87.09, 29.02) * mm, "radius": 1 * mm});
            skCircle(sketch, "E4.0.59.12", {"center": v(90.2, 29.02) * mm, "radius": 1 * mm});
            skCircle(sketch, "E4.0.60.12", {"center": v(93.33, 29.02) * mm, "radius": 1 * mm});
            skCircle(sketch, "E4.0.61.12", {"center": v(96.45, 29.02) * mm, "radius": 1 * mm});
            skCircle(sketch, "E4.0.62.12", {"center": v(99.57, 29.02) * mm, "radius": 1 * mm});
            skCircle(sketch, "E4.0.63.12", {"center": v(102.69, 29.02) * mm, "radius": 1 * mm});
            skCircle(sketch, "E4.0.64.12", {"center": v(105.8, 29.02) * mm, "radius": 1 * mm});
            skCircle(sketch, "E4.0.65.12", {"center": v(108.93, 29.02) * mm, "radius": 1 * mm});
            skCircle(sketch, "E4.0.66.12", {"center": v(112.05, 29.02) * mm, "radius": 1 * mm});
            skCircle(sketch, "E4.0.67.12", {"center": v(115.17, 29.02) * mm, "radius": 1 * mm});
            skCircle(sketch, "E4.0.68.12", {"center": v(118.29, 29.02) * mm, "radius": 1 * mm});
            skCircle(sketch, "E4.0.69.12", {"center": v(121.4, 29.02) * mm, "radius": 1 * mm});
            skCircle(sketch, "E4.0.70.12", {"center": v(124.53, 29.02) * mm, "radius": 1 * mm});
            skCircle(sketch, "E4.0.71.12", {"center": v(127.65, 29.02) * mm, "radius": 1 * mm});
            skCircle(sketch, "E4.0.72.12", {"center": v(130.77, 29.02) * mm, "radius": 1 * mm});
            skCircle(sketch, "E4.0.73.12", {"center": v(133.89, 29.02) * mm, "radius": 1 * mm});
            skCircle(sketch, "E4.0.74.12", {"center": v(137, 29.02) * mm, "radius": 1 * mm});
            skCircle(sketch, "E4.0.75.12", {"center": v(140.13, 29.02) * mm, "radius": 1 * mm});
            skCircle(sketch, "E4.0.76.12", {"center": v(143.25, 29.02) * mm, "radius": 1 * mm});
            skCircle(sketch, "E4.0.77.12", {"center": v(146.37, 29.02) * mm, "radius": 1 * mm});
            skCircle(sketch, "E4.0.78.12", {"center": v(149.49, 29.02) * mm, "radius": 1 * mm});
            skCircle(sketch, "E4.0.79.12", {"center": v(152.6, 29.02) * mm, "radius": 1 * mm});
            skCircle(sketch, "E4.0.80.12", {"center": v(155.73, 29.02) * mm, "radius": 1 * mm});
            skCircle(sketch, "E4.0.81.12", {"center": v(158.85, 29.02) * mm, "radius": 1 * mm});
            skCircle(sketch, "E4.0.82.12", {"center": v(161.97, 29.02) * mm, "radius": 1 * mm});
            skCircle(sketch, "E4.0.83.12", {"center": v(165.09, 29.02) * mm, "radius": 1 * mm});
            skCircle(sketch, "E4.0.84.12", {"center": v(168.2, 29.02) * mm, "radius": 1 * mm});
            skCircle(sketch, "E4.0.85.12", {"center": v(171.33, 29.02) * mm, "radius": 1 * mm});
            skCircle(sketch, "E4.0.86.12", {"center": v(174.45, 29.02) * mm, "radius": 1 * mm});
            skCircle(sketch, "E4.0.87.12", {"center": v(177.57, 29.02) * mm, "radius": 1 * mm});
            skCircle(sketch, "E4.0.88.12", {"center": v(180.69, 29.02) * mm, "radius": 1 * mm});
            skCircle(sketch, "E4.0.89.12", {"center": v(183.8, 29.02) * mm, "radius": 1 * mm});
            skCircle(sketch, "E4.0.90.12", {"center": v(186.93, 29.02) * mm, "radius": 1 * mm});
            skCircle(sketch, "E4.0.91.12", {"center": v(190.05, 29.02) * mm, "radius": 1 * mm});
            skCircle(sketch, "E4.0.92.12", {"center": v(193.17, 29.02) * mm, "radius": 1 * mm});
            skCircle(sketch, "E4.0.93.12", {"center": v(196.29, 29.02) * mm, "radius": 1 * mm});
            skCircle(sketch, "E4.0.94.12", {"center": v(199.4, 29.02) * mm, "radius": 1 * mm});
            skSolve(sketch);
        }
        {
            var Q0;
            Q0=makeQuery(id+"F0.imprint","IMPRINT",FACE,{"disambiguationData":[TD([[makeQuery(id+"F0.imprint","IMPRINT",EDGE,{"derivedFrom":sQuery(id+"F0.wireOp",EDGE,"E0.bottom")}),-1.0]])]});
            extrude(context, id + "F1", {"entities" : qUnion([Q0]), "depth" : 0.5 * mm});
        }
        {
            var Q0;
            Q0=makeQuery(id+"F1.opExtrude","CAP_FACE",FACE,{"disambiguationData":[OSD([sQuery(id+"F0.wireOp",EDGE,"E0.bottom"),sQuery(id+"F0.wireOp",EDGE,"E0.top"),sQuery(id+"F0.wireOp",EDGE,"E0.left"),sQuery(id+"F0.wireOp",EDGE,"E0.right"),sQuery(id+"F0.wireOp",EDGE,"E1"),sQuery(id+"F0.wireOp",EDGE,"E2.0.1.0"),sQuery(id+"F0.wireOp",EDGE,"E2.0.2.0"),sQuery(id+"F0.wireOp",EDGE,"E2.0.3.0"),sQuery(id+"F0.wireOp",EDGE,"E2.0.4.0"),sQuery(id+"F0.wireOp",EDGE,"E2.0.5.0"),sQuery(id+"F0.wireOp",EDGE,"E2.0.6.0"),sQuery(id+"F0.wireOp",EDGE,"E2.0.7.0"),sQuery(id+"F0.wireOp",EDGE,"E2.0.8.0"),sQuery(id+"F0.wireOp",EDGE,"E2.0.9.0"),sQuery(id+"F0.wireOp",EDGE,"E2.0.10.0"),sQuery(id+"F0.wireOp",EDGE,"E2.0.11.0"),sQuery(id+"F0.wireOp",EDGE,"E2.1.0.0"),sQuery(id+"F0.wireOp",EDGE,"E2.1.1.0"),sQuery(id+"F0.wireOp",EDGE,"E2.1.2.0"),sQuery(id+"F0.wireOp",EDGE,"E2.1.3.0"),sQuery(id+"F0.wireOp",EDGE,"E2.1.4.0"),sQuery(id+"F0.wireOp",EDGE,"E2.1.5.0"),sQuery(id+"F0.wireOp",EDGE,"E2.1.6.0"),sQuery(id+"F0.wireOp",EDGE,"E2.1.7.0"),sQuery(id+"F0.wireOp",EDGE,"E2.1.8.0"),sQuery(id+"F0.wireOp",EDGE,"E2.1.9.0"),sQuery(id+"F0.wireOp",EDGE,"E2.1.10.0"),sQuery(id+"F0.wireOp",EDGE,"E2.1.11.0"),sQuery(id+"F0.wireOp",EDGE,"E2.2.0.0"),sQuery(id+"F0.wireOp",EDGE,"E2.2.1.0"),sQuery(id+"F0.wireOp",EDGE,"E2.2.2.0"),sQuery(id+"F0.wireOp",EDGE,"E2.2.3.0"),sQuery(id+"F0.wireOp",EDGE,"E2.2.4.0"),sQuery(id+"F0.wireOp",EDGE,"E2.2.5.0"),sQuery(id+"F0.wireOp",EDGE,"E2.2.6.0"),sQuery(id+"F0.wireOp",EDGE,"E2.2.7.0"),sQuery(id+"F0.wireOp",EDGE,"E2.2.8.0"),sQuery(id+"F0.wireOp",EDGE,"E2.2.9.0"),sQuery(id+"F0.wireOp",EDGE,"E2.2.10.0"),sQuery(id+"F0.wireOp",EDGE,"E2.2.11.0"),sQuery(id+"F0.wireOp",EDGE,"E2.3.0.0"),sQuery(id+"F0.wireOp",EDGE,"E2.3.1.0"),sQuery(id+"F0.wireOp",EDGE,"E2.3.2.0"),sQuery(id+"F0.wireOp",EDGE,"E2.3.3.0"),sQuery(id+"F0.wireOp",EDGE,"E2.3.4.0"),sQuery(id+"F0.wireOp",EDGE,"E2.3.5.0"),sQuery(id+"F0.wireOp",EDGE,"E2.3.6.0"),sQuery(id+"F0.wireOp",EDGE,"E2.3.7.0"),sQuery(id+"F0.wireOp",EDGE,"E2.3.8.0"),sQuery(id+"F0.wireOp",EDGE,"E2.3.9.0"),sQuery(id+"F0.wireOp",EDGE,"E2.3.10.0"),sQuery(id+"F0.wireOp",EDGE,"E2.3.11.0"),sQuery(id+"F0.wireOp",EDGE,"E2.4.0.0"),sQuery(id+"F0.wireOp",EDGE,"E2.4.1.0"),sQuery(id+"F0.wireOp",EDGE,"E2.4.2.0"),sQuery(id+"F0.wireOp",EDGE,"E2.4.3.0"),sQuery(id+"F0.wireOp",EDGE,"E2.4.4.0"),sQuery(id+"F0.wireOp",EDGE,"E2.4.5.0"),sQuery(id+"F0.wireOp",EDGE,"E2.4.6.0"),sQuery(id+"F0.wireOp",EDGE,"E2.4.7.0"),sQuery(id+"F0.wireOp",EDGE,"E2.4.8.0"),sQuery(id+"F0.wireOp",EDGE,"E2.4.9.0"),sQuery(id+"F0.wireOp",EDGE,"E2.4.10.0"),sQuery(id+"F0.wireOp",EDGE,"E2.4.11.0"),sQuery(id+"F0.wireOp",EDGE,"E2.5.0.0"),sQuery(id+"F0.wireOp",EDGE,"E2.5.1.0"),sQuery(id+"F0.wireOp",EDGE,"E2.5.2.0"),sQuery(id+"F0.wireOp",EDGE,"E2.5.3.0"),sQuery(id+"F0.wireOp",EDGE,"E2.5.4.0"),sQuery(id+"F0.wireOp",EDGE,"E2.5.5.0"),sQuery(id+"F0.wireOp",EDGE,"E2.5.6.0"),sQuery(id+"F0.wireOp",EDGE,"E2.5.7.0"),sQuery(id+"F0.wireOp",EDGE,"E2.5.8.0"),sQuery(id+"F0.wireOp",EDGE,"E2.5.9.0"),sQuery(id+"F0.wireOp",EDGE,"E2.5.10.0"),sQuery(id+"F0.wireOp",EDGE,"E2.5.11.0"),sQuery(id+"F0.wireOp",EDGE,"E2.6.0.0"),sQuery(id+"F0.wireOp",EDGE,"E2.6.1.0"),sQuery(id+"F0.wireOp",EDGE,"E2.6.2.0"),sQuery(id+"F0.wireOp",EDGE,"E2.6.3.0"),sQuery(id+"F0.wireOp",EDGE,"E2.6.4.0"),sQuery(id+"F0.wireOp",EDGE,"E2.6.5.0"),sQuery(id+"F0.wireOp",EDGE,"E2.6.6.0"),sQuery(id+"F0.wireOp",EDGE,"E2.6.7.0"),sQuery(id+"F0.wireOp",EDGE,"E2.6.8.0"),sQuery(id+"F0.wireOp",EDGE,"E2.6.9.0"),sQuery(id+"F0.wireOp",EDGE,"E2.6.10.0"),sQuery(id+"F0.wireOp",EDGE,"E2.6.11.0"),sQuery(id+"F0.wireOp",EDGE,"E2.7.0.0"),sQuery(id+"F0.wireOp",EDGE,"E2.7.1.0"),sQuery(id+"F0.wireOp",EDGE,"E2.7.2.0"),sQuery(id+"F0.wireOp",EDGE,"E2.7.3.0"),sQuery(id+"F0.wireOp",EDGE,"E2.7.4.0"),sQuery(id+"F0.wireOp",EDGE,"E2.7.5.0"),sQuery(id+"F0.wireOp",EDGE,"E2.7.6.0"),sQuery(id+"F0.wireOp",EDGE,"E2.7.7.0"),sQuery(id+"F0.wireOp",EDGE,"E2.7.8.0"),sQuery(id+"F0.wireOp",EDGE,"E2.7.9.0"),sQuery(id+"F0.wireOp",EDGE,"E2.7.10.0"),sQuery(id+"F0.wireOp",EDGE,"E2.7.11.0"),sQuery(id+"F0.wireOp",EDGE,"E2.8.0.0"),sQuery(id+"F0.wireOp",EDGE,"E2.8.1.0"),sQuery(id+"F0.wireOp",EDGE,"E2.8.2.0"),sQuery(id+"F0.wireOp",EDGE,"E2.8.3.0"),sQuery(id+"F0.wireOp",EDGE,"E2.8.4.0"),sQuery(id+"F0.wireOp",EDGE,"E2.8.5.0"),sQuery(id+"F0.wireOp",EDGE,"E2.8.6.0"),sQuery(id+"F0.wireOp",EDGE,"E2.8.7.0"),sQuery(id+"F0.wireOp",EDGE,"E2.8.8.0"),sQuery(id+"F0.wireOp",EDGE,"E2.8.9.0"),sQuery(id+"F0.wireOp",EDGE,"E2.8.10.0"),sQuery(id+"F0.wireOp",EDGE,"E2.8.11.0"),sQuery(id+"F0.wireOp",EDGE,"E2.9.0.0"),sQuery(id+"F0.wireOp",EDGE,"E2.9.1.0"),sQuery(id+"F0.wireOp",EDGE,"E2.9.2.0"),sQuery(id+"F0.wireOp",EDGE,"E2.9.3.0"),sQuery(id+"F0.wireOp",EDGE,"E2.9.4.0"),sQuery(id+"F0.wireOp",EDGE,"E2.9.5.0"),sQuery(id+"F0.wireOp",EDGE,"E2.9.6.0"),sQuery(id+"F0.wireOp",EDGE,"E2.9.7.0"),sQuery(id+"F0.wireOp",EDGE,"E2.9.8.0"),sQuery(id+"F0.wireOp",EDGE,"E2.9.9.0"),sQuery(id+"F0.wireOp",EDGE,"E2.9.10.0"),sQuery(id+"F0.wireOp",EDGE,"E2.9.11.0"),sQuery(id+"F0.wireOp",EDGE,"E2.10.0.0"),sQuery(id+"F0.wireOp",EDGE,"E2.10.1.0"),sQuery(id+"F0.wireOp",EDGE,"E2.10.2.0"),sQuery(id+"F0.wireOp",EDGE,"E2.10.3.0"),sQuery(id+"F0.wireOp",EDGE,"E2.10.4.0"),sQuery(id+"F0.wireOp",EDGE,"E2.10.5.0"),sQuery(id+"F0.wireOp",EDGE,"E2.10.6.0"),sQuery(id+"F0.wireOp",EDGE,"E2.10.7.0"),sQuery(id+"F0.wireOp",EDGE,"E2.10.8.0"),sQuery(id+"F0.wireOp",EDGE,"E2.10.9.0"),sQuery(id+"F0.wireOp",EDGE,"E2.10.10.0"),sQuery(id+"F0.wireOp",EDGE,"E2.10.11.0"),sQuery(id+"F0.wireOp",EDGE,"E2.11.0.0"),sQuery(id+"F0.wireOp",EDGE,"E2.11.1.0"),sQuery(id+"F0.wireOp",EDGE,"E2.11.2.0"),sQuery(id+"F0.wireOp",EDGE,"E2.11.3.0"),sQuery(id+"F0.wireOp",EDGE,"E2.11.4.0"),sQuery(id+"F0.wireOp",EDGE,"E2.11.5.0"),sQuery(id+"F0.wireOp",EDGE,"E2.11.6.0"),sQuery(id+"F0.wireOp",EDGE,"E2.11.7.0"),sQuery(id+"F0.wireOp",EDGE,"E2.11.8.0"),sQuery(id+"F0.wireOp",EDGE,"E2.11.9.0"),sQuery(id+"F0.wireOp",EDGE,"E2.11.10.0"),sQuery(id+"F0.wireOp",EDGE,"E2.11.11.0"),sQuery(id+"F0.wireOp",EDGE,"E2.12.0.0"),sQuery(id+"F0.wireOp",EDGE,"E2.12.1.0"),sQuery(id+"F0.wireOp",EDGE,"E2.12.2.0"),sQuery(id+"F0.wireOp",EDGE,"E2.12.3.0"),sQuery(id+"F0.wireOp",EDGE,"E2.12.4.0"),sQuery(id+"F0.wireOp",EDGE,"E2.12.5.0"),sQuery(id+"F0.wireOp",EDGE,"E2.12.6.0"),sQuery(id+"F0.wireOp",EDGE,"E2.12.7.0"),sQuery(id+"F0.wireOp",EDGE,"E2.12.8.0"),sQuery(id+"F0.wireOp",EDGE,"E2.12.9.0"),sQuery(id+"F0.wireOp",EDGE,"E2.12.10.0"),sQuery(id+"F0.wireOp",EDGE,"E2.12.11.0"),sQuery(id+"F0.wireOp",EDGE,"E2.13.0.0"),sQuery(id+"F0.wireOp",EDGE,"E2.13.1.0"),sQuery(id+"F0.wireOp",EDGE,"E2.13.2.0"),sQuery(id+"F0.wireOp",EDGE,"E2.13.3.0"),sQuery(id+"F0.wireOp",EDGE,"E2.13.4.0"),sQuery(id+"F0.wireOp",EDGE,"E2.13.5.0"),sQuery(id+"F0.wireOp",EDGE,"E2.13.6.0"),sQuery(id+"F0.wireOp",EDGE,"E2.13.7.0"),sQuery(id+"F0.wireOp",EDGE,"E2.13.8.0"),sQuery(id+"F0.wireOp",EDGE,"E2.13.9.0"),sQuery(id+"F0.wireOp",EDGE,"E2.13.10.0"),sQuery(id+"F0.wireOp",EDGE,"E2.13.11.0"),sQuery(id+"F0.wireOp",EDGE,"E2.14.0.0"),sQuery(id+"F0.wireOp",EDGE,"E2.14.1.0"),sQuery(id+"F0.wireOp",EDGE,"E2.14.2.0"),sQuery(id+"F0.wireOp",EDGE,"E2.14.3.0"),sQuery(id+"F0.wireOp",EDGE,"E2.14.4.0"),sQuery(id+"F0.wireOp",EDGE,"E2.14.5.0"),sQuery(id+"F0.wireOp",EDGE,"E2.14.6.0"),sQuery(id+"F0.wireOp",EDGE,"E2.14.7.0"),sQuery(id+"F0.wireOp",EDGE,"E2.14.8.0"),sQuery(id+"F0.wireOp",EDGE,"E2.14.9.0"),sQuery(id+"F0.wireOp",EDGE,"E2.14.10.0"),sQuery(id+"F0.wireOp",EDGE,"E2.14.11.0"),sQuery(id+"F0.wireOp",EDGE,"E2.15.0.0"),sQuery(id+"F0.wireOp",EDGE,"E2.15.1.0"),sQuery(id+"F0.wireOp",EDGE,"E2.15.2.0"),sQuery(id+"F0.wireOp",EDGE,"E2.15.3.0"),sQuery(id+"F0.wireOp",EDGE,"E2.15.4.0"),sQuery(id+"F0.wireOp",EDGE,"E2.15.5.0"),sQuery(id+"F0.wireOp",EDGE,"E2.15.6.0"),sQuery(id+"F0.wireOp",EDGE,"E2.15.7.0"),sQuery(id+"F0.wireOp",EDGE,"E2.15.8.0"),sQuery(id+"F0.wireOp",EDGE,"E2.15.9.0"),sQuery(id+"F0.wireOp",EDGE,"E2.15.10.0"),sQuery(id+"F0.wireOp",EDGE,"E2.15.11.0"),sQuery(id+"F0.wireOp",EDGE,"E2.16.0.0"),sQuery(id+"F0.wireOp",EDGE,"E2.16.1.0"),sQuery(id+"F0.wireOp",EDGE,"E2.16.2.0"),sQuery(id+"F0.wireOp",EDGE,"E2.16.3.0"),sQuery(id+"F0.wireOp",EDGE,"E2.16.4.0"),sQuery(id+"F0.wireOp",EDGE,"E2.16.5.0"),sQuery(id+"F0.wireOp",EDGE,"E2.16.6.0"),sQuery(id+"F0.wireOp",EDGE,"E2.16.7.0"),sQuery(id+"F0.wireOp",EDGE,"E2.16.8.0"),sQuery(id+"F0.wireOp",EDGE,"E2.16.9.0"),sQuery(id+"F0.wireOp",EDGE,"E2.16.10.0"),sQuery(id+"F0.wireOp",EDGE,"E2.16.11.0"),sQuery(id+"F0.wireOp",EDGE,"E2.17.0.0"),sQuery(id+"F0.wireOp",EDGE,"E2.17.1.0"),sQuery(id+"F0.wireOp",EDGE,"E2.17.2.0"),sQuery(id+"F0.wireOp",EDGE,"E2.17.3.0"),sQuery(id+"F0.wireOp",EDGE,"E2.17.4.0"),sQuery(id+"F0.wireOp",EDGE,"E2.17.5.0"),sQuery(id+"F0.wireOp",EDGE,"E2.17.6.0"),sQuery(id+"F0.wireOp",EDGE,"E2.17.7.0"),sQuery(id+"F0.wireOp",EDGE,"E2.17.8.0"),sQuery(id+"F0.wireOp",EDGE,"E2.17.9.0"),sQuery(id+"F0.wireOp",EDGE,"E2.17.10.0"),sQuery(id+"F0.wireOp",EDGE,"E2.17.11.0"),sQuery(id+"F0.wireOp",EDGE,"E2.18.0.0"),sQuery(id+"F0.wireOp",EDGE,"E2.18.1.0"),sQuery(id+"F0.wireOp",EDGE,"E2.18.2.0"),sQuery(id+"F0.wireOp",EDGE,"E2.18.3.0"),sQuery(id+"F0.wireOp",EDGE,"E2.18.4.0"),sQuery(id+"F0.wireOp",EDGE,"E2.18.5.0"),sQuery(id+"F0.wireOp",EDGE,"E2.18.6.0"),sQuery(id+"F0.wireOp",EDGE,"E2.18.7.0"),sQuery(id+"F0.wireOp",EDGE,"E2.18.8.0"),sQuery(id+"F0.wireOp",EDGE,"E2.18.9.0"),sQuery(id+"F0.wireOp",EDGE,"E2.18.10.0"),sQuery(id+"F0.wireOp",EDGE,"E2.18.11.0"),sQuery(id+"F0.wireOp",EDGE,"E2.19.0.0"),sQuery(id+"F0.wireOp",EDGE,"E2.19.1.0"),sQuery(id+"F0.wireOp",EDGE,"E2.19.2.0"),sQuery(id+"F0.wireOp",EDGE,"E2.19.3.0"),sQuery(id+"F0.wireOp",EDGE,"E2.19.4.0"),sQuery(id+"F0.wireOp",EDGE,"E2.19.5.0"),sQuery(id+"F0.wireOp",EDGE,"E2.19.6.0"),sQuery(id+"F0.wireOp",EDGE,"E2.19.7.0"),sQuery(id+"F0.wireOp",EDGE,"E2.19.8.0"),sQuery(id+"F0.wireOp",EDGE,"E2.19.9.0"),sQuery(id+"F0.wireOp",EDGE,"E2.19.10.0"),sQuery(id+"F0.wireOp",EDGE,"E2.19.11.0"),sQuery(id+"F0.wireOp",EDGE,"E2.20.0.0"),sQuery(id+"F0.wireOp",EDGE,"E2.20.1.0"),sQuery(id+"F0.wireOp",EDGE,"E2.20.2.0"),sQuery(id+"F0.wireOp",EDGE,"E2.20.3.0"),sQuery(id+"F0.wireOp",EDGE,"E2.20.4.0"),sQuery(id+"F0.wireOp",EDGE,"E2.20.5.0"),sQuery(id+"F0.wireOp",EDGE,"E2.20.6.0"),sQuery(id+"F0.wireOp",EDGE,"E2.20.7.0"),sQuery(id+"F0.wireOp",EDGE,"E2.20.8.0"),sQuery(id+"F0.wireOp",EDGE,"E2.20.9.0"),sQuery(id+"F0.wireOp",EDGE,"E2.20.10.0"),sQuery(id+"F0.wireOp",EDGE,"E2.20.11.0"),sQuery(id+"F0.wireOp",EDGE,"E2.21.0.0"),sQuery(id+"F0.wireOp",EDGE,"E2.21.1.0"),sQuery(id+"F0.wireOp",EDGE,"E2.21.2.0"),sQuery(id+"F0.wireOp",EDGE,"E2.21.3.0"),sQuery(id+"F0.wireOp",EDGE,"E2.21.4.0"),sQuery(id+"F0.wireOp",EDGE,"E2.21.5.0"),sQuery(id+"F0.wireOp",EDGE,"E2.21.6.0"),sQuery(id+"F0.wireOp",EDGE,"E2.21.7.0"),sQuery(id+"F0.wireOp",EDGE,"E2.21.8.0"),sQuery(id+"F0.wireOp",EDGE,"E2.21.9.0"),sQuery(id+"F0.wireOp",EDGE,"E2.21.10.0"),sQuery(id+"F0.wireOp",EDGE,"E2.21.11.0"),sQuery(id+"F0.wireOp",EDGE,"E2.22.0.0"),sQuery(id+"F0.wireOp",EDGE,"E2.22.1.0"),sQuery(id+"F0.wireOp",EDGE,"E2.22.2.0"),sQuery(id+"F0.wireOp",EDGE,"E2.22.3.0"),sQuery(id+"F0.wireOp",EDGE,"E2.22.4.0"),sQuery(id+"F0.wireOp",EDGE,"E2.22.5.0"),sQuery(id+"F0.wireOp",EDGE,"E2.22.6.0"),sQuery(id+"F0.wireOp",EDGE,"E2.22.7.0"),sQuery(id+"F0.wireOp",EDGE,"E2.22.8.0"),sQuery(id+"F0.wireOp",EDGE,"E2.22.9.0"),sQuery(id+"F0.wireOp",EDGE,"E2.22.10.0"),sQuery(id+"F0.wireOp",EDGE,"E2.22.11.0"),sQuery(id+"F0.wireOp",EDGE,"E2.23.0.0"),sQuery(id+"F0.wireOp",EDGE,"E2.23.1.0"),sQuery(id+"F0.wireOp",EDGE,"E2.23.2.0"),sQuery(id+"F0.wireOp",EDGE,"E2.23.3.0"),sQuery(id+"F0.wireOp",EDGE,"E2.23.4.0"),sQuery(id+"F0.wireOp",EDGE,"E2.23.5.0"),sQuery(id+"F0.wireOp",EDGE,"E2.23.6.0"),sQuery(id+"F0.wireOp",EDGE,"E2.23.7.0"),sQuery(id+"F0.wireOp",EDGE,"E2.23.8.0"),sQuery(id+"F0.wireOp",EDGE,"E2.23.9.0"),sQuery(id+"F0.wireOp",EDGE,"E2.23.10.0"),sQuery(id+"F0.wireOp",EDGE,"E2.23.11.0"),sQuery(id+"F0.wireOp",EDGE,"E2.24.0.0"),sQuery(id+"F0.wireOp",EDGE,"E2.24.1.0"),sQuery(id+"F0.wireOp",EDGE,"E2.24.2.0"),sQuery(id+"F0.wireOp",EDGE,"E2.24.3.0"),sQuery(id+"F0.wireOp",EDGE,"E2.24.4.0"),sQuery(id+"F0.wireOp",EDGE,"E2.24.5.0"),sQuery(id+"F0.wireOp",EDGE,"E2.24.6.0"),sQuery(id+"F0.wireOp",EDGE,"E2.24.7.0"),sQuery(id+"F0.wireOp",EDGE,"E2.24.8.0"),sQuery(id+"F0.wireOp",EDGE,"E2.24.9.0"),sQuery(id+"F0.wireOp",EDGE,"E2.24.10.0"),sQuery(id+"F0.wireOp",EDGE,"E2.24.11.0"),sQuery(id+"F0.wireOp",EDGE,"E2.25.0.0"),sQuery(id+"F0.wireOp",EDGE,"E2.25.1.0"),sQuery(id+"F0.wireOp",EDGE,"E2.25.2.0"),sQuery(id+"F0.wireOp",EDGE,"E2.25.3.0"),sQuery(id+"F0.wireOp",EDGE,"E2.25.4.0"),sQuery(id+"F0.wireOp",EDGE,"E2.25.5.0"),sQuery(id+"F0.wireOp",EDGE,"E2.25.6.0"),sQuery(id+"F0.wireOp",EDGE,"E2.25.7.0"),sQuery(id+"F0.wireOp",EDGE,"E2.25.8.0"),sQuery(id+"F0.wireOp",EDGE,"E2.25.9.0"),sQuery(id+"F0.wireOp",EDGE,"E2.25.10.0"),sQuery(id+"F0.wireOp",EDGE,"E2.25.11.0"),sQuery(id+"F0.wireOp",EDGE,"E2.26.0.0"),sQuery(id+"F0.wireOp",EDGE,"E2.26.1.0"),sQuery(id+"F0.wireOp",EDGE,"E2.26.2.0"),sQuery(id+"F0.wireOp",EDGE,"E2.26.3.0"),sQuery(id+"F0.wireOp",EDGE,"E2.26.4.0"),sQuery(id+"F0.wireOp",EDGE,"E2.26.5.0"),sQuery(id+"F0.wireOp",EDGE,"E2.26.6.0"),sQuery(id+"F0.wireOp",EDGE,"E2.26.7.0"),sQuery(id+"F0.wireOp",EDGE,"E2.26.8.0"),sQuery(id+"F0.wireOp",EDGE,"E2.26.9.0"),sQuery(id+"F0.wireOp",EDGE,"E2.26.10.0"),sQuery(id+"F0.wireOp",EDGE,"E2.26.11.0"),sQuery(id+"F0.wireOp",EDGE,"E2.27.0.0"),sQuery(id+"F0.wireOp",EDGE,"E2.27.1.0"),sQuery(id+"F0.wireOp",EDGE,"E2.27.2.0"),sQuery(id+"F0.wireOp",EDGE,"E2.27.3.0"),sQuery(id+"F0.wireOp",EDGE,"E2.27.4.0"),sQuery(id+"F0.wireOp",EDGE,"E2.27.5.0"),sQuery(id+"F0.wireOp",EDGE,"E2.27.6.0"),sQuery(id+"F0.wireOp",EDGE,"E2.27.7.0"),sQuery(id+"F0.wireOp",EDGE,"E2.27.8.0"),sQuery(id+"F0.wireOp",EDGE,"E2.27.9.0"),sQuery(id+"F0.wireOp",EDGE,"E2.27.10.0"),sQuery(id+"F0.wireOp",EDGE,"E2.27.11.0"),sQuery(id+"F0.wireOp",EDGE,"E2.28.0.0"),sQuery(id+"F0.wireOp",EDGE,"E2.28.1.0"),sQuery(id+"F0.wireOp",EDGE,"E2.28.2.0"),sQuery(id+"F0.wireOp",EDGE,"E2.28.3.0"),sQuery(id+"F0.wireOp",EDGE,"E2.28.4.0"),sQuery(id+"F0.wireOp",EDGE,"E2.28.5.0"),sQuery(id+"F0.wireOp",EDGE,"E2.28.6.0"),sQuery(id+"F0.wireOp",EDGE,"E2.28.7.0"),sQuery(id+"F0.wireOp",EDGE,"E2.28.8.0"),sQuery(id+"F0.wireOp",EDGE,"E2.28.9.0"),sQuery(id+"F0.wireOp",EDGE,"E2.28.10.0"),sQuery(id+"F0.wireOp",EDGE,"E2.28.11.0"),sQuery(id+"F0.wireOp",EDGE,"E2.29.0.0"),sQuery(id+"F0.wireOp",EDGE,"E2.29.1.0"),sQuery(id+"F0.wireOp",EDGE,"E2.29.2.0"),sQuery(id+"F0.wireOp",EDGE,"E2.29.3.0"),sQuery(id+"F0.wireOp",EDGE,"E2.29.4.0"),sQuery(id+"F0.wireOp",EDGE,"E2.29.5.0"),sQuery(id+"F0.wireOp",EDGE,"E2.29.6.0"),sQuery(id+"F0.wireOp",EDGE,"E2.29.7.0"),sQuery(id+"F0.wireOp",EDGE,"E2.29.8.0"),sQuery(id+"F0.wireOp",EDGE,"E2.29.9.0"),sQuery(id+"F0.wireOp",EDGE,"E2.29.10.0"),sQuery(id+"F0.wireOp",EDGE,"E2.29.11.0"),sQuery(id+"F0.wireOp",EDGE,"E2.30.0.0"),sQuery(id+"F0.wireOp",EDGE,"E2.30.1.0"),sQuery(id+"F0.wireOp",EDGE,"E2.30.2.0"),sQuery(id+"F0.wireOp",EDGE,"E2.30.3.0"),sQuery(id+"F0.wireOp",EDGE,"E2.30.4.0"),sQuery(id+"F0.wireOp",EDGE,"E2.30.5.0"),sQuery(id+"F0.wireOp",EDGE,"E2.30.6.0"),sQuery(id+"F0.wireOp",EDGE,"E2.30.7.0"),sQuery(id+"F0.wireOp",EDGE,"E2.30.8.0"),sQuery(id+"F0.wireOp",EDGE,"E2.30.9.0"),sQuery(id+"F0.wireOp",EDGE,"E2.30.10.0"),sQuery(id+"F0.wireOp",EDGE,"E2.30.11.0"),sQuery(id+"F0.wireOp",EDGE,"E2.31.0.0"),sQuery(id+"F0.wireOp",EDGE,"E2.31.1.0"),sQuery(id+"F0.wireOp",EDGE,"E2.31.2.0"),sQuery(id+"F0.wireOp",EDGE,"E2.31.3.0"),sQuery(id+"F0.wireOp",EDGE,"E2.31.4.0"),sQuery(id+"F0.wireOp",EDGE,"E2.31.5.0"),sQuery(id+"F0.wireOp",EDGE,"E2.31.6.0"),sQuery(id+"F0.wireOp",EDGE,"E2.31.7.0"),sQuery(id+"F0.wireOp",EDGE,"E2.31.8.0"),sQuery(id+"F0.wireOp",EDGE,"E2.31.9.0"),sQuery(id+"F0.wireOp",EDGE,"E2.31.10.0"),sQuery(id+"F0.wireOp",EDGE,"E2.31.11.0"),sQuery(id+"F0.wireOp",EDGE,"E2.32.0.0"),sQuery(id+"F0.wireOp",EDGE,"E2.32.1.0"),sQuery(id+"F0.wireOp",EDGE,"E2.32.2.0"),sQuery(id+"F0.wireOp",EDGE,"E2.32.3.0"),sQuery(id+"F0.wireOp",EDGE,"E2.32.4.0"),sQuery(id+"F0.wireOp",EDGE,"E2.32.5.0"),sQuery(id+"F0.wireOp",EDGE,"E2.32.6.0"),sQuery(id+"F0.wireOp",EDGE,"E2.32.7.0"),sQuery(id+"F0.wireOp",EDGE,"E2.32.8.0"),sQuery(id+"F0.wireOp",EDGE,"E2.32.9.0"),sQuery(id+"F0.wireOp",EDGE,"E2.32.10.0"),sQuery(id+"F0.wireOp",EDGE,"E2.32.11.0"),sQuery(id+"F0.wireOp",EDGE,"E2.33.0.0"),sQuery(id+"F0.wireOp",EDGE,"E2.33.1.0"),sQuery(id+"F0.wireOp",EDGE,"E2.33.2.0"),sQuery(id+"F0.wireOp",EDGE,"E2.33.3.0"),sQuery(id+"F0.wireOp",EDGE,"E2.33.4.0"),sQuery(id+"F0.wireOp",EDGE,"E2.33.5.0"),sQuery(id+"F0.wireOp",EDGE,"E2.33.6.0"),sQuery(id+"F0.wireOp",EDGE,"E2.33.7.0"),sQuery(id+"F0.wireOp",EDGE,"E2.33.8.0"),sQuery(id+"F0.wireOp",EDGE,"E2.33.9.0"),sQuery(id+"F0.wireOp",EDGE,"E2.33.10.0"),sQuery(id+"F0.wireOp",EDGE,"E2.33.11.0"),sQuery(id+"F0.wireOp",EDGE,"E2.34.0.0"),sQuery(id+"F0.wireOp",EDGE,"E2.34.1.0"),sQuery(id+"F0.wireOp",EDGE,"E2.34.2.0"),sQuery(id+"F0.wireOp",EDGE,"E2.34.3.0"),sQuery(id+"F0.wireOp",EDGE,"E2.34.4.0"),sQuery(id+"F0.wireOp",EDGE,"E2.34.5.0"),sQuery(id+"F0.wireOp",EDGE,"E2.34.6.0"),sQuery(id+"F0.wireOp",EDGE,"E2.34.7.0"),sQuery(id+"F0.wireOp",EDGE,"E2.34.8.0"),sQuery(id+"F0.wireOp",EDGE,"E2.34.9.0"),sQuery(id+"F0.wireOp",EDGE,"E2.34.10.0"),sQuery(id+"F0.wireOp",EDGE,"E2.34.11.0"),sQuery(id+"F0.wireOp",EDGE,"E2.35.0.0"),sQuery(id+"F0.wireOp",EDGE,"E2.35.1.0"),sQuery(id+"F0.wireOp",EDGE,"E2.35.2.0"),sQuery(id+"F0.wireOp",EDGE,"E2.35.3.0"),sQuery(id+"F0.wireOp",EDGE,"E2.35.4.0"),sQuery(id+"F0.wireOp",EDGE,"E2.35.5.0"),sQuery(id+"F0.wireOp",EDGE,"E2.35.6.0"),sQuery(id+"F0.wireOp",EDGE,"E2.35.7.0"),sQuery(id+"F0.wireOp",EDGE,"E2.35.8.0"),sQuery(id+"F0.wireOp",EDGE,"E2.35.9.0"),sQuery(id+"F0.wireOp",EDGE,"E2.35.10.0"),sQuery(id+"F0.wireOp",EDGE,"E2.35.11.0"),sQuery(id+"F0.wireOp",EDGE,"E2.36.0.0"),sQuery(id+"F0.wireOp",EDGE,"E2.36.1.0"),sQuery(id+"F0.wireOp",EDGE,"E2.36.2.0"),sQuery(id+"F0.wireOp",EDGE,"E2.36.3.0"),sQuery(id+"F0.wireOp",EDGE,"E2.36.4.0"),sQuery(id+"F0.wireOp",EDGE,"E2.36.5.0"),sQuery(id+"F0.wireOp",EDGE,"E2.36.6.0"),sQuery(id+"F0.wireOp",EDGE,"E2.36.7.0"),sQuery(id+"F0.wireOp",EDGE,"E2.36.8.0"),sQuery(id+"F0.wireOp",EDGE,"E2.36.9.0"),sQuery(id+"F0.wireOp",EDGE,"E2.36.10.0"),sQuery(id+"F0.wireOp",EDGE,"E2.36.11.0"),sQuery(id+"F0.wireOp",EDGE,"E2.37.0.0"),sQuery(id+"F0.wireOp",EDGE,"E2.37.1.0"),sQuery(id+"F0.wireOp",EDGE,"E2.37.2.0"),sQuery(id+"F0.wireOp",EDGE,"E2.37.3.0"),sQuery(id+"F0.wireOp",EDGE,"E2.37.4.0"),sQuery(id+"F0.wireOp",EDGE,"E2.37.5.0"),sQuery(id+"F0.wireOp",EDGE,"E2.37.6.0"),sQuery(id+"F0.wireOp",EDGE,"E2.37.7.0"),sQuery(id+"F0.wireOp",EDGE,"E2.37.8.0"),sQuery(id+"F0.wireOp",EDGE,"E2.37.9.0"),sQuery(id+"F0.wireOp",EDGE,"E2.37.10.0"),sQuery(id+"F0.wireOp",EDGE,"E2.37.11.0"),sQuery(id+"F0.wireOp",EDGE,"E2.38.0.0"),sQuery(id+"F0.wireOp",EDGE,"E2.38.1.0"),sQuery(id+"F0.wireOp",EDGE,"E2.38.2.0"),sQuery(id+"F0.wireOp",EDGE,"E2.38.3.0"),sQuery(id+"F0.wireOp",EDGE,"E2.38.4.0"),sQuery(id+"F0.wireOp",EDGE,"E2.38.5.0"),sQuery(id+"F0.wireOp",EDGE,"E2.38.6.0"),sQuery(id+"F0.wireOp",EDGE,"E2.38.7.0"),sQuery(id+"F0.wireOp",EDGE,"E2.38.8.0"),sQuery(id+"F0.wireOp",EDGE,"E2.38.9.0"),sQuery(id+"F0.wireOp",EDGE,"E2.38.10.0"),sQuery(id+"F0.wireOp",EDGE,"E2.38.11.0"),sQuery(id+"F0.wireOp",EDGE,"E2.39.0.0"),sQuery(id+"F0.wireOp",EDGE,"E2.39.1.0"),sQuery(id+"F0.wireOp",EDGE,"E2.39.2.0"),sQuery(id+"F0.wireOp",EDGE,"E2.39.3.0"),sQuery(id+"F0.wireOp",EDGE,"E2.39.4.0"),sQuery(id+"F0.wireOp",EDGE,"E2.39.5.0"),sQuery(id+"F0.wireOp",EDGE,"E2.39.6.0"),sQuery(id+"F0.wireOp",EDGE,"E2.39.7.0"),sQuery(id+"F0.wireOp",EDGE,"E2.39.8.0"),sQuery(id+"F0.wireOp",EDGE,"E2.39.9.0"),sQuery(id+"F0.wireOp",EDGE,"E2.39.10.0"),sQuery(id+"F0.wireOp",EDGE,"E2.39.11.0"),sQuery(id+"F0.wireOp",EDGE,"E2.40.0.0"),sQuery(id+"F0.wireOp",EDGE,"E2.40.1.0"),sQuery(id+"F0.wireOp",EDGE,"E2.40.2.0"),sQuery(id+"F0.wireOp",EDGE,"E2.40.3.0"),sQuery(id+"F0.wireOp",EDGE,"E2.40.4.0"),sQuery(id+"F0.wireOp",EDGE,"E2.40.5.0"),sQuery(id+"F0.wireOp",EDGE,"E2.40.6.0"),sQuery(id+"F0.wireOp",EDGE,"E2.40.7.0"),sQuery(id+"F0.wireOp",EDGE,"E2.40.8.0"),sQuery(id+"F0.wireOp",EDGE,"E2.40.9.0"),sQuery(id+"F0.wireOp",EDGE,"E2.40.10.0"),sQuery(id+"F0.wireOp",EDGE,"E2.40.11.0"),sQuery(id+"F0.wireOp",EDGE,"E2.41.0.0"),sQuery(id+"F0.wireOp",EDGE,"E2.41.1.0"),sQuery(id+"F0.wireOp",EDGE,"E2.41.2.0"),sQuery(id+"F0.wireOp",EDGE,"E2.41.3.0"),sQuery(id+"F0.wireOp",EDGE,"E2.41.4.0"),sQuery(id+"F0.wireOp",EDGE,"E2.41.5.0"),sQuery(id+"F0.wireOp",EDGE,"E2.41.6.0"),sQuery(id+"F0.wireOp",EDGE,"E2.41.7.0"),sQuery(id+"F0.wireOp",EDGE,"E2.41.8.0"),sQuery(id+"F0.wireOp",EDGE,"E2.41.9.0"),sQuery(id+"F0.wireOp",EDGE,"E2.41.10.0"),sQuery(id+"F0.wireOp",EDGE,"E2.41.11.0"),sQuery(id+"F0.wireOp",EDGE,"E2.42.0.0"),sQuery(id+"F0.wireOp",EDGE,"E2.42.1.0"),sQuery(id+"F0.wireOp",EDGE,"E2.42.2.0"),sQuery(id+"F0.wireOp",EDGE,"E2.42.3.0"),sQuery(id+"F0.wireOp",EDGE,"E2.42.4.0"),sQuery(id+"F0.wireOp",EDGE,"E2.42.5.0"),sQuery(id+"F0.wireOp",EDGE,"E2.42.6.0"),sQuery(id+"F0.wireOp",EDGE,"E2.42.7.0"),sQuery(id+"F0.wireOp",EDGE,"E2.42.8.0"),sQuery(id+"F0.wireOp",EDGE,"E2.42.9.0"),sQuery(id+"F0.wireOp",EDGE,"E2.42.10.0"),sQuery(id+"F0.wireOp",EDGE,"E2.42.11.0"),sQuery(id+"F0.wireOp",EDGE,"E2.43.0.0"),sQuery(id+"F0.wireOp",EDGE,"E2.43.1.0"),sQuery(id+"F0.wireOp",EDGE,"E2.43.2.0"),sQuery(id+"F0.wireOp",EDGE,"E2.43.3.0"),sQuery(id+"F0.wireOp",EDGE,"E2.43.4.0"),sQuery(id+"F0.wireOp",EDGE,"E2.43.5.0"),sQuery(id+"F0.wireOp",EDGE,"E2.43.6.0"),sQuery(id+"F0.wireOp",EDGE,"E2.43.7.0"),sQuery(id+"F0.wireOp",EDGE,"E2.43.8.0"),sQuery(id+"F0.wireOp",EDGE,"E2.43.9.0"),sQuery(id+"F0.wireOp",EDGE,"E2.43.10.0"),sQuery(id+"F0.wireOp",EDGE,"E2.43.11.0"),sQuery(id+"F0.wireOp",EDGE,"E2.44.0.0"),sQuery(id+"F0.wireOp",EDGE,"E2.44.1.0"),sQuery(id+"F0.wireOp",EDGE,"E2.44.2.0"),sQuery(id+"F0.wireOp",EDGE,"E2.44.3.0"),sQuery(id+"F0.wireOp",EDGE,"E2.44.4.0"),sQuery(id+"F0.wireOp",EDGE,"E2.44.5.0"),sQuery(id+"F0.wireOp",EDGE,"E2.44.6.0"),sQuery(id+"F0.wireOp",EDGE,"E2.44.7.0"),sQuery(id+"F0.wireOp",EDGE,"E2.44.8.0"),sQuery(id+"F0.wireOp",EDGE,"E2.44.9.0"),sQuery(id+"F0.wireOp",EDGE,"E2.44.10.0"),sQuery(id+"F0.wireOp",EDGE,"E2.44.11.0"),sQuery(id+"F0.wireOp",EDGE,"E2.45.0.0"),sQuery(id+"F0.wireOp",EDGE,"E2.45.1.0"),sQuery(id+"F0.wireOp",EDGE,"E2.45.2.0"),sQuery(id+"F0.wireOp",EDGE,"E2.45.3.0"),sQuery(id+"F0.wireOp",EDGE,"E2.45.4.0"),sQuery(id+"F0.wireOp",EDGE,"E2.45.5.0"),sQuery(id+"F0.wireOp",EDGE,"E2.45.6.0"),sQuery(id+"F0.wireOp",EDGE,"E2.45.7.0"),sQuery(id+"F0.wireOp",EDGE,"E2.45.8.0"),sQuery(id+"F0.wireOp",EDGE,"E2.45.9.0"),sQuery(id+"F0.wireOp",EDGE,"E2.45.10.0"),sQuery(id+"F0.wireOp",EDGE,"E2.45.11.0"),sQuery(id+"F0.wireOp",EDGE,"E2.46.0.0"),sQuery(id+"F0.wireOp",EDGE,"E2.46.1.0"),sQuery(id+"F0.wireOp",EDGE,"E2.46.2.0"),sQuery(id+"F0.wireOp",EDGE,"E2.46.3.0"),sQuery(id+"F0.wireOp",EDGE,"E2.46.4.0"),sQuery(id+"F0.wireOp",EDGE,"E2.46.5.0"),sQuery(id+"F0.wireOp",EDGE,"E2.46.6.0"),sQuery(id+"F0.wireOp",EDGE,"E2.46.7.0"),sQuery(id+"F0.wireOp",EDGE,"E2.46.8.0"),sQuery(id+"F0.wireOp",EDGE,"E2.46.9.0"),sQuery(id+"F0.wireOp",EDGE,"E2.46.10.0"),sQuery(id+"F0.wireOp",EDGE,"E2.46.11.0"),sQuery(id+"F0.wireOp",EDGE,"E2.47.0.0"),sQuery(id+"F0.wireOp",EDGE,"E2.47.1.0"),sQuery(id+"F0.wireOp",EDGE,"E2.47.2.0"),sQuery(id+"F0.wireOp",EDGE,"E2.47.3.0"),sQuery(id+"F0.wireOp",EDGE,"E2.47.4.0"),sQuery(id+"F0.wireOp",EDGE,"E2.47.5.0"),sQuery(id+"F0.wireOp",EDGE,"E2.47.6.0"),sQuery(id+"F0.wireOp",EDGE,"E2.47.7.0"),sQuery(id+"F0.wireOp",EDGE,"E2.47.8.0"),sQuery(id+"F0.wireOp",EDGE,"E2.47.9.0"),sQuery(id+"F0.wireOp",EDGE,"E2.47.10.0"),sQuery(id+"F0.wireOp",EDGE,"E2.47.11.0"),sQuery(id+"F0.wireOp",EDGE,"E2.48.0.0"),sQuery(id+"F0.wireOp",EDGE,"E2.48.1.0"),sQuery(id+"F0.wireOp",EDGE,"E2.48.2.0"),sQuery(id+"F0.wireOp",EDGE,"E2.48.3.0"),sQuery(id+"F0.wireOp",EDGE,"E2.48.4.0"),sQuery(id+"F0.wireOp",EDGE,"E2.48.5.0"),sQuery(id+"F0.wireOp",EDGE,"E2.48.6.0"),sQuery(id+"F0.wireOp",EDGE,"E2.48.7.0"),sQuery(id+"F0.wireOp",EDGE,"E2.48.8.0"),sQuery(id+"F0.wireOp",EDGE,"E2.48.9.0"),sQuery(id+"F0.wireOp",EDGE,"E2.48.10.0"),sQuery(id+"F0.wireOp",EDGE,"E2.48.11.0"),sQuery(id+"F0.wireOp",EDGE,"E2.49.0.0"),sQuery(id+"F0.wireOp",EDGE,"E2.49.1.0"),sQuery(id+"F0.wireOp",EDGE,"E2.49.2.0"),sQuery(id+"F0.wireOp",EDGE,"E2.49.3.0"),sQuery(id+"F0.wireOp",EDGE,"E2.49.4.0"),sQuery(id+"F0.wireOp",EDGE,"E2.49.5.0"),sQuery(id+"F0.wireOp",EDGE,"E2.49.6.0"),sQuery(id+"F0.wireOp",EDGE,"E2.49.7.0"),sQuery(id+"F0.wireOp",EDGE,"E2.49.8.0"),sQuery(id+"F0.wireOp",EDGE,"E2.49.9.0"),sQuery(id+"F0.wireOp",EDGE,"E2.49.10.0"),sQuery(id+"F0.wireOp",EDGE,"E2.49.11.0"),sQuery(id+"F0.wireOp",EDGE,"E3.0.50.0"),sQuery(id+"F0.wireOp",EDGE,"E3.0.50.1"),sQuery(id+"F0.wireOp",EDGE,"E3.0.50.2"),sQuery(id+"F0.wireOp",EDGE,"E3.0.50.3"),sQuery(id+"F0.wireOp",EDGE,"E3.0.50.4"),sQuery(id+"F0.wireOp",EDGE,"E3.0.50.5"),sQuery(id+"F0.wireOp",EDGE,"E3.0.50.6"),sQuery(id+"F0.wireOp",EDGE,"E3.0.50.7"),sQuery(id+"F0.wireOp",EDGE,"E3.0.50.8"),sQuery(id+"F0.wireOp",EDGE,"E3.0.50.9"),sQuery(id+"F0.wireOp",EDGE,"E3.0.50.10"),sQuery(id+"F0.wireOp",EDGE,"E3.0.50.11"),sQuery(id+"F0.wireOp",EDGE,"E3.0.51.0"),sQuery(id+"F0.wireOp",EDGE,"E3.0.51.1"),sQuery(id+"F0.wireOp",EDGE,"E3.0.51.2"),sQuery(id+"F0.wireOp",EDGE,"E3.0.51.3"),sQuery(id+"F0.wireOp",EDGE,"E3.0.51.4"),sQuery(id+"F0.wireOp",EDGE,"E3.0.51.5"),sQuery(id+"F0.wireOp",EDGE,"E3.0.51.6"),sQuery(id+"F0.wireOp",EDGE,"E3.0.51.7"),sQuery(id+"F0.wireOp",EDGE,"E3.0.51.8"),sQuery(id+"F0.wireOp",EDGE,"E3.0.51.9"),sQuery(id+"F0.wireOp",EDGE,"E3.0.51.10"),sQuery(id+"F0.wireOp",EDGE,"E3.0.51.11"),sQuery(id+"F0.wireOp",EDGE,"E3.0.52.0"),sQuery(id+"F0.wireOp",EDGE,"E3.0.52.1"),sQuery(id+"F0.wireOp",EDGE,"E3.0.52.2"),sQuery(id+"F0.wireOp",EDGE,"E3.0.52.3"),sQuery(id+"F0.wireOp",EDGE,"E3.0.52.4"),sQuery(id+"F0.wireOp",EDGE,"E3.0.52.5"),sQuery(id+"F0.wireOp",EDGE,"E3.0.52.6"),sQuery(id+"F0.wireOp",EDGE,"E3.0.52.7"),sQuery(id+"F0.wireOp",EDGE,"E3.0.52.8"),sQuery(id+"F0.wireOp",EDGE,"E3.0.52.9"),sQuery(id+"F0.wireOp",EDGE,"E3.0.52.10"),sQuery(id+"F0.wireOp",EDGE,"E3.0.52.11"),sQuery(id+"F0.wireOp",EDGE,"E3.0.53.0"),sQuery(id+"F0.wireOp",EDGE,"E3.0.53.1"),sQuery(id+"F0.wireOp",EDGE,"E3.0.53.2"),sQuery(id+"F0.wireOp",EDGE,"E3.0.53.3"),sQuery(id+"F0.wireOp",EDGE,"E3.0.53.4"),sQuery(id+"F0.wireOp",EDGE,"E3.0.53.5"),sQuery(id+"F0.wireOp",EDGE,"E3.0.53.6"),sQuery(id+"F0.wireOp",EDGE,"E3.0.53.7"),sQuery(id+"F0.wireOp",EDGE,"E3.0.53.8"),sQuery(id+"F0.wireOp",EDGE,"E3.0.53.9"),sQuery(id+"F0.wireOp",EDGE,"E3.0.53.10"),sQuery(id+"F0.wireOp",EDGE,"E3.0.53.11"),sQuery(id+"F0.wireOp",EDGE,"E3.0.54.0"),sQuery(id+"F0.wireOp",EDGE,"E3.0.54.1"),sQuery(id+"F0.wireOp",EDGE,"E3.0.54.2"),sQuery(id+"F0.wireOp",EDGE,"E3.0.54.3"),sQuery(id+"F0.wireOp",EDGE,"E3.0.54.4"),sQuery(id+"F0.wireOp",EDGE,"E3.0.54.5"),sQuery(id+"F0.wireOp",EDGE,"E3.0.54.6"),sQuery(id+"F0.wireOp",EDGE,"E3.0.54.7"),sQuery(id+"F0.wireOp",EDGE,"E3.0.54.8"),sQuery(id+"F0.wireOp",EDGE,"E3.0.54.9"),sQuery(id+"F0.wireOp",EDGE,"E3.0.54.10"),sQuery(id+"F0.wireOp",EDGE,"E3.0.54.11"),sQuery(id+"F0.wireOp",EDGE,"E3.0.55.0"),sQuery(id+"F0.wireOp",EDGE,"E3.0.55.1"),sQuery(id+"F0.wireOp",EDGE,"E3.0.55.2"),sQuery(id+"F0.wireOp",EDGE,"E3.0.55.3"),sQuery(id+"F0.wireOp",EDGE,"E3.0.55.4"),sQuery(id+"F0.wireOp",EDGE,"E3.0.55.5"),sQuery(id+"F0.wireOp",EDGE,"E3.0.55.6"),sQuery(id+"F0.wireOp",EDGE,"E3.0.55.7"),sQuery(id+"F0.wireOp",EDGE,"E3.0.55.8"),sQuery(id+"F0.wireOp",EDGE,"E3.0.55.9"),sQuery(id+"F0.wireOp",EDGE,"E3.0.55.10"),sQuery(id+"F0.wireOp",EDGE,"E3.0.55.11"),sQuery(id+"F0.wireOp",EDGE,"E3.0.56.0"),sQuery(id+"F0.wireOp",EDGE,"E3.0.56.1"),sQuery(id+"F0.wireOp",EDGE,"E3.0.56.2"),sQuery(id+"F0.wireOp",EDGE,"E3.0.56.3"),sQuery(id+"F0.wireOp",EDGE,"E3.0.56.4"),sQuery(id+"F0.wireOp",EDGE,"E3.0.56.5"),sQuery(id+"F0.wireOp",EDGE,"E3.0.56.6"),sQuery(id+"F0.wireOp",EDGE,"E3.0.56.7"),sQuery(id+"F0.wireOp",EDGE,"E3.0.56.8"),sQuery(id+"F0.wireOp",EDGE,"E3.0.56.9"),sQuery(id+"F0.wireOp",EDGE,"E3.0.56.10"),sQuery(id+"F0.wireOp",EDGE,"E3.0.56.11"),sQuery(id+"F0.wireOp",EDGE,"E3.0.57.0"),sQuery(id+"F0.wireOp",EDGE,"E3.0.57.1"),sQuery(id+"F0.wireOp",EDGE,"E3.0.57.2"),sQuery(id+"F0.wireOp",EDGE,"E3.0.57.3"),sQuery(id+"F0.wireOp",EDGE,"E3.0.57.4"),sQuery(id+"F0.wireOp",EDGE,"E3.0.57.5"),sQuery(id+"F0.wireOp",EDGE,"E3.0.57.6"),sQuery(id+"F0.wireOp",EDGE,"E3.0.57.7"),sQuery(id+"F0.wireOp",EDGE,"E3.0.57.8"),sQuery(id+"F0.wireOp",EDGE,"E3.0.57.9"),sQuery(id+"F0.wireOp",EDGE,"E3.0.57.10"),sQuery(id+"F0.wireOp",EDGE,"E3.0.57.11"),sQuery(id+"F0.wireOp",EDGE,"E3.0.58.0"),sQuery(id+"F0.wireOp",EDGE,"E3.0.58.1"),sQuery(id+"F0.wireOp",EDGE,"E3.0.58.2"),sQuery(id+"F0.wireOp",EDGE,"E3.0.58.3"),sQuery(id+"F0.wireOp",EDGE,"E3.0.58.4"),sQuery(id+"F0.wireOp",EDGE,"E3.0.58.5"),sQuery(id+"F0.wireOp",EDGE,"E3.0.58.6"),sQuery(id+"F0.wireOp",EDGE,"E3.0.58.7"),sQuery(id+"F0.wireOp",EDGE,"E3.0.58.8"),sQuery(id+"F0.wireOp",EDGE,"E3.0.58.9"),sQuery(id+"F0.wireOp",EDGE,"E3.0.58.10"),sQuery(id+"F0.wireOp",EDGE,"E3.0.58.11"),sQuery(id+"F0.wireOp",EDGE,"E3.0.59.0"),sQuery(id+"F0.wireOp",EDGE,"E3.0.59.1"),sQuery(id+"F0.wireOp",EDGE,"E3.0.59.2"),sQuery(id+"F0.wireOp",EDGE,"E3.0.59.3"),sQuery(id+"F0.wireOp",EDGE,"E3.0.59.4"),sQuery(id+"F0.wireOp",EDGE,"E3.0.59.5"),sQuery(id+"F0.wireOp",EDGE,"E3.0.59.6"),sQuery(id+"F0.wireOp",EDGE,"E3.0.59.7"),sQuery(id+"F0.wireOp",EDGE,"E3.0.59.8"),sQuery(id+"F0.wireOp",EDGE,"E3.0.59.9"),sQuery(id+"F0.wireOp",EDGE,"E3.0.59.10"),sQuery(id+"F0.wireOp",EDGE,"E3.0.59.11"),sQuery(id+"F0.wireOp",EDGE,"E3.0.60.0"),sQuery(id+"F0.wireOp",EDGE,"E3.0.60.1"),sQuery(id+"F0.wireOp",EDGE,"E3.0.60.2"),sQuery(id+"F0.wireOp",EDGE,"E3.0.60.3"),sQuery(id+"F0.wireOp",EDGE,"E3.0.60.4"),sQuery(id+"F0.wireOp",EDGE,"E3.0.60.5"),sQuery(id+"F0.wireOp",EDGE,"E3.0.60.6"),sQuery(id+"F0.wireOp",EDGE,"E3.0.60.7"),sQuery(id+"F0.wireOp",EDGE,"E3.0.60.8"),sQuery(id+"F0.wireOp",EDGE,"E3.0.60.9"),sQuery(id+"F0.wireOp",EDGE,"E3.0.60.10"),sQuery(id+"F0.wireOp",EDGE,"E3.0.60.11"),sQuery(id+"F0.wireOp",EDGE,"E3.0.61.0"),sQuery(id+"F0.wireOp",EDGE,"E3.0.61.1"),sQuery(id+"F0.wireOp",EDGE,"E3.0.61.2"),sQuery(id+"F0.wireOp",EDGE,"E3.0.61.3"),sQuery(id+"F0.wireOp",EDGE,"E3.0.61.4"),sQuery(id+"F0.wireOp",EDGE,"E3.0.61.5"),sQuery(id+"F0.wireOp",EDGE,"E3.0.61.6"),sQuery(id+"F0.wireOp",EDGE,"E3.0.61.7"),sQuery(id+"F0.wireOp",EDGE,"E3.0.61.8"),sQuery(id+"F0.wireOp",EDGE,"E3.0.61.9"),sQuery(id+"F0.wireOp",EDGE,"E3.0.61.10"),sQuery(id+"F0.wireOp",EDGE,"E3.0.61.11"),sQuery(id+"F0.wireOp",EDGE,"E3.0.62.0"),sQuery(id+"F0.wireOp",EDGE,"E3.0.62.1"),sQuery(id+"F0.wireOp",EDGE,"E3.0.62.2"),sQuery(id+"F0.wireOp",EDGE,"E3.0.62.3"),sQuery(id+"F0.wireOp",EDGE,"E3.0.62.4"),sQuery(id+"F0.wireOp",EDGE,"E3.0.62.5"),sQuery(id+"F0.wireOp",EDGE,"E3.0.62.6"),sQuery(id+"F0.wireOp",EDGE,"E3.0.62.7"),sQuery(id+"F0.wireOp",EDGE,"E3.0.62.8"),sQuery(id+"F0.wireOp",EDGE,"E3.0.62.9"),sQuery(id+"F0.wireOp",EDGE,"E3.0.62.10"),sQuery(id+"F0.wireOp",EDGE,"E3.0.62.11"),sQuery(id+"F0.wireOp",EDGE,"E3.0.63.0"),sQuery(id+"F0.wireOp",EDGE,"E3.0.63.1"),sQuery(id+"F0.wireOp",EDGE,"E3.0.63.2"),sQuery(id+"F0.wireOp",EDGE,"E3.0.63.3"),sQuery(id+"F0.wireOp",EDGE,"E3.0.63.4"),sQuery(id+"F0.wireOp",EDGE,"E3.0.63.5"),sQuery(id+"F0.wireOp",EDGE,"E3.0.63.6"),sQuery(id+"F0.wireOp",EDGE,"E3.0.63.7"),sQuery(id+"F0.wireOp",EDGE,"E3.0.63.8"),sQuery(id+"F0.wireOp",EDGE,"E3.0.63.9"),sQuery(id+"F0.wireOp",EDGE,"E3.0.63.10"),sQuery(id+"F0.wireOp",EDGE,"E3.0.63.11"),sQuery(id+"F0.wireOp",EDGE,"E3.0.64.0"),sQuery(id+"F0.wireOp",EDGE,"E3.0.64.1"),sQuery(id+"F0.wireOp",EDGE,"E3.0.64.2"),sQuery(id+"F0.wireOp",EDGE,"E3.0.64.3"),sQuery(id+"F0.wireOp",EDGE,"E3.0.64.4"),sQuery(id+"F0.wireOp",EDGE,"E3.0.64.5"),sQuery(id+"F0.wireOp",EDGE,"E3.0.64.6"),sQuery(id+"F0.wireOp",EDGE,"E3.0.64.7"),sQuery(id+"F0.wireOp",EDGE,"E3.0.64.8"),sQuery(id+"F0.wireOp",EDGE,"E3.0.64.9"),sQuery(id+"F0.wireOp",EDGE,"E3.0.64.10"),sQuery(id+"F0.wireOp",EDGE,"E3.0.64.11"),sQuery(id+"F0.wireOp",EDGE,"E3.0.65.0"),sQuery(id+"F0.wireOp",EDGE,"E3.0.65.1"),sQuery(id+"F0.wireOp",EDGE,"E3.0.65.2"),sQuery(id+"F0.wireOp",EDGE,"E3.0.65.3"),sQuery(id+"F0.wireOp",EDGE,"E3.0.65.4"),sQuery(id+"F0.wireOp",EDGE,"E3.0.65.5"),sQuery(id+"F0.wireOp",EDGE,"E3.0.65.6"),sQuery(id+"F0.wireOp",EDGE,"E3.0.65.7"),sQuery(id+"F0.wireOp",EDGE,"E3.0.65.8"),sQuery(id+"F0.wireOp",EDGE,"E3.0.65.9"),sQuery(id+"F0.wireOp",EDGE,"E3.0.65.10"),sQuery(id+"F0.wireOp",EDGE,"E3.0.65.11"),sQuery(id+"F0.wireOp",EDGE,"E3.0.66.0"),sQuery(id+"F0.wireOp",EDGE,"E3.0.66.1"),sQuery(id+"F0.wireOp",EDGE,"E3.0.66.2"),sQuery(id+"F0.wireOp",EDGE,"E3.0.66.3"),sQuery(id+"F0.wireOp",EDGE,"E3.0.66.4"),sQuery(id+"F0.wireOp",EDGE,"E3.0.66.5"),sQuery(id+"F0.wireOp",EDGE,"E3.0.66.6"),sQuery(id+"F0.wireOp",EDGE,"E3.0.66.7"),sQuery(id+"F0.wireOp",EDGE,"E3.0.66.8"),sQuery(id+"F0.wireOp",EDGE,"E3.0.66.9"),sQuery(id+"F0.wireOp",EDGE,"E3.0.66.10"),sQuery(id+"F0.wireOp",EDGE,"E3.0.66.11"),sQuery(id+"F0.wireOp",EDGE,"E3.0.67.0"),sQuery(id+"F0.wireOp",EDGE,"E3.0.67.1"),sQuery(id+"F0.wireOp",EDGE,"E3.0.67.2"),sQuery(id+"F0.wireOp",EDGE,"E3.0.67.3"),sQuery(id+"F0.wireOp",EDGE,"E3.0.67.4"),sQuery(id+"F0.wireOp",EDGE,"E3.0.67.5"),sQuery(id+"F0.wireOp",EDGE,"E3.0.67.6"),sQuery(id+"F0.wireOp",EDGE,"E3.0.67.7"),sQuery(id+"F0.wireOp",EDGE,"E3.0.67.8"),sQuery(id+"F0.wireOp",EDGE,"E3.0.67.9"),sQuery(id+"F0.wireOp",EDGE,"E3.0.67.10"),sQuery(id+"F0.wireOp",EDGE,"E3.0.67.11"),sQuery(id+"F0.wireOp",EDGE,"E3.0.68.0"),sQuery(id+"F0.wireOp",EDGE,"E3.0.68.1"),sQuery(id+"F0.wireOp",EDGE,"E3.0.68.2"),sQuery(id+"F0.wireOp",EDGE,"E3.0.68.3"),sQuery(id+"F0.wireOp",EDGE,"E3.0.68.4"),sQuery(id+"F0.wireOp",EDGE,"E3.0.68.5"),sQuery(id+"F0.wireOp",EDGE,"E3.0.68.6"),sQuery(id+"F0.wireOp",EDGE,"E3.0.68.7"),sQuery(id+"F0.wireOp",EDGE,"E3.0.68.8"),sQuery(id+"F0.wireOp",EDGE,"E3.0.68.9"),sQuery(id+"F0.wireOp",EDGE,"E3.0.68.10"),sQuery(id+"F0.wireOp",EDGE,"E3.0.68.11"),sQuery(id+"F0.wireOp",EDGE,"E3.0.69.0"),sQuery(id+"F0.wireOp",EDGE,"E3.0.69.1"),sQuery(id+"F0.wireOp",EDGE,"E3.0.69.2"),sQuery(id+"F0.wireOp",EDGE,"E3.0.69.3"),sQuery(id+"F0.wireOp",EDGE,"E3.0.69.4"),sQuery(id+"F0.wireOp",EDGE,"E3.0.69.5"),sQuery(id+"F0.wireOp",EDGE,"E3.0.69.6"),sQuery(id+"F0.wireOp",EDGE,"E3.0.69.7"),sQuery(id+"F0.wireOp",EDGE,"E3.0.69.8"),sQuery(id+"F0.wireOp",EDGE,"E3.0.69.9"),sQuery(id+"F0.wireOp",EDGE,"E3.0.69.10"),sQuery(id+"F0.wireOp",EDGE,"E3.0.69.11"),sQuery(id+"F0.wireOp",EDGE,"E3.0.70.0"),sQuery(id+"F0.wireOp",EDGE,"E3.0.70.1"),sQuery(id+"F0.wireOp",EDGE,"E3.0.70.2"),sQuery(id+"F0.wireOp",EDGE,"E3.0.70.3"),sQuery(id+"F0.wireOp",EDGE,"E3.0.70.4"),sQuery(id+"F0.wireOp",EDGE,"E3.0.70.5"),sQuery(id+"F0.wireOp",EDGE,"E3.0.70.6"),sQuery(id+"F0.wireOp",EDGE,"E3.0.70.7"),sQuery(id+"F0.wireOp",EDGE,"E3.0.70.8"),sQuery(id+"F0.wireOp",EDGE,"E3.0.70.9"),sQuery(id+"F0.wireOp",EDGE,"E3.0.70.10"),sQuery(id+"F0.wireOp",EDGE,"E3.0.70.11"),sQuery(id+"F0.wireOp",EDGE,"E3.0.71.0"),sQuery(id+"F0.wireOp",EDGE,"E3.0.71.1"),sQuery(id+"F0.wireOp",EDGE,"E3.0.71.2"),sQuery(id+"F0.wireOp",EDGE,"E3.0.71.3"),sQuery(id+"F0.wireOp",EDGE,"E3.0.71.4"),sQuery(id+"F0.wireOp",EDGE,"E3.0.71.5"),sQuery(id+"F0.wireOp",EDGE,"E3.0.71.6"),sQuery(id+"F0.wireOp",EDGE,"E3.0.71.7"),sQuery(id+"F0.wireOp",EDGE,"E3.0.71.8"),sQuery(id+"F0.wireOp",EDGE,"E3.0.71.9"),sQuery(id+"F0.wireOp",EDGE,"E3.0.71.10"),sQuery(id+"F0.wireOp",EDGE,"E3.0.71.11"),sQuery(id+"F0.wireOp",EDGE,"E3.0.72.0"),sQuery(id+"F0.wireOp",EDGE,"E3.0.72.1"),sQuery(id+"F0.wireOp",EDGE,"E3.0.72.2"),sQuery(id+"F0.wireOp",EDGE,"E3.0.72.3"),sQuery(id+"F0.wireOp",EDGE,"E3.0.72.4"),sQuery(id+"F0.wireOp",EDGE,"E3.0.72.5"),sQuery(id+"F0.wireOp",EDGE,"E3.0.72.6"),sQuery(id+"F0.wireOp",EDGE,"E3.0.72.7"),sQuery(id+"F0.wireOp",EDGE,"E3.0.72.8"),sQuery(id+"F0.wireOp",EDGE,"E3.0.72.9"),sQuery(id+"F0.wireOp",EDGE,"E3.0.72.10"),sQuery(id+"F0.wireOp",EDGE,"E3.0.72.11"),sQuery(id+"F0.wireOp",EDGE,"E3.0.73.0"),sQuery(id+"F0.wireOp",EDGE,"E3.0.73.1"),sQuery(id+"F0.wireOp",EDGE,"E3.0.73.2"),sQuery(id+"F0.wireOp",EDGE,"E3.0.73.3"),sQuery(id+"F0.wireOp",EDGE,"E3.0.73.4"),sQuery(id+"F0.wireOp",EDGE,"E3.0.73.5"),sQuery(id+"F0.wireOp",EDGE,"E3.0.73.6"),sQuery(id+"F0.wireOp",EDGE,"E3.0.73.7"),sQuery(id+"F0.wireOp",EDGE,"E3.0.73.8"),sQuery(id+"F0.wireOp",EDGE,"E3.0.73.9"),sQuery(id+"F0.wireOp",EDGE,"E3.0.73.10"),sQuery(id+"F0.wireOp",EDGE,"E3.0.73.11"),sQuery(id+"F0.wireOp",EDGE,"E3.0.74.0"),sQuery(id+"F0.wireOp",EDGE,"E3.0.74.1"),sQuery(id+"F0.wireOp",EDGE,"E3.0.74.2"),sQuery(id+"F0.wireOp",EDGE,"E3.0.74.3"),sQuery(id+"F0.wireOp",EDGE,"E3.0.74.4"),sQuery(id+"F0.wireOp",EDGE,"E3.0.74.5"),sQuery(id+"F0.wireOp",EDGE,"E3.0.74.6"),sQuery(id+"F0.wireOp",EDGE,"E3.0.74.7"),sQuery(id+"F0.wireOp",EDGE,"E3.0.74.8"),sQuery(id+"F0.wireOp",EDGE,"E3.0.74.9"),sQuery(id+"F0.wireOp",EDGE,"E3.0.74.10"),sQuery(id+"F0.wireOp",EDGE,"E3.0.74.11"),sQuery(id+"F0.wireOp",EDGE,"E3.0.75.0"),sQuery(id+"F0.wireOp",EDGE,"E3.0.75.1"),sQuery(id+"F0.wireOp",EDGE,"E3.0.75.2"),sQuery(id+"F0.wireOp",EDGE,"E3.0.75.3"),sQuery(id+"F0.wireOp",EDGE,"E3.0.75.4"),sQuery(id+"F0.wireOp",EDGE,"E3.0.75.5"),sQuery(id+"F0.wireOp",EDGE,"E3.0.75.6"),sQuery(id+"F0.wireOp",EDGE,"E3.0.75.7"),sQuery(id+"F0.wireOp",EDGE,"E3.0.75.8"),sQuery(id+"F0.wireOp",EDGE,"E3.0.75.9"),sQuery(id+"F0.wireOp",EDGE,"E3.0.75.10"),sQuery(id+"F0.wireOp",EDGE,"E3.0.75.11"),sQuery(id+"F0.wireOp",EDGE,"E3.0.76.0"),sQuery(id+"F0.wireOp",EDGE,"E3.0.76.1"),sQuery(id+"F0.wireOp",EDGE,"E3.0.76.2"),sQuery(id+"F0.wireOp",EDGE,"E3.0.76.3"),sQuery(id+"F0.wireOp",EDGE,"E3.0.76.4"),sQuery(id+"F0.wireOp",EDGE,"E3.0.76.5"),sQuery(id+"F0.wireOp",EDGE,"E3.0.76.6"),sQuery(id+"F0.wireOp",EDGE,"E3.0.76.7"),sQuery(id+"F0.wireOp",EDGE,"E3.0.76.8"),sQuery(id+"F0.wireOp",EDGE,"E3.0.76.9"),sQuery(id+"F0.wireOp",EDGE,"E3.0.76.10"),sQuery(id+"F0.wireOp",EDGE,"E3.0.76.11"),sQuery(id+"F0.wireOp",EDGE,"E3.0.77.0"),sQuery(id+"F0.wireOp",EDGE,"E3.0.77.1"),sQuery(id+"F0.wireOp",EDGE,"E3.0.77.2"),sQuery(id+"F0.wireOp",EDGE,"E3.0.77.3"),sQuery(id+"F0.wireOp",EDGE,"E3.0.77.4"),sQuery(id+"F0.wireOp",EDGE,"E3.0.77.5"),sQuery(id+"F0.wireOp",EDGE,"E3.0.77.6"),sQuery(id+"F0.wireOp",EDGE,"E3.0.77.7"),sQuery(id+"F0.wireOp",EDGE,"E3.0.77.8"),sQuery(id+"F0.wireOp",EDGE,"E3.0.77.9"),sQuery(id+"F0.wireOp",EDGE,"E3.0.77.10"),sQuery(id+"F0.wireOp",EDGE,"E3.0.77.11"),sQuery(id+"F0.wireOp",EDGE,"E3.0.78.0"),sQuery(id+"F0.wireOp",EDGE,"E3.0.78.1"),sQuery(id+"F0.wireOp",EDGE,"E3.0.78.2"),sQuery(id+"F0.wireOp",EDGE,"E3.0.78.3"),sQuery(id+"F0.wireOp",EDGE,"E3.0.78.4"),sQuery(id+"F0.wireOp",EDGE,"E3.0.78.5"),sQuery(id+"F0.wireOp",EDGE,"E3.0.78.6"),sQuery(id+"F0.wireOp",EDGE,"E3.0.78.7"),sQuery(id+"F0.wireOp",EDGE,"E3.0.78.8"),sQuery(id+"F0.wireOp",EDGE,"E3.0.78.9"),sQuery(id+"F0.wireOp",EDGE,"E3.0.78.10"),sQuery(id+"F0.wireOp",EDGE,"E3.0.78.11"),sQuery(id+"F0.wireOp",EDGE,"E3.0.79.0"),sQuery(id+"F0.wireOp",EDGE,"E3.0.79.1"),sQuery(id+"F0.wireOp",EDGE,"E3.0.79.2"),sQuery(id+"F0.wireOp",EDGE,"E3.0.79.3"),sQuery(id+"F0.wireOp",EDGE,"E3.0.79.4"),sQuery(id+"F0.wireOp",EDGE,"E3.0.79.5"),sQuery(id+"F0.wireOp",EDGE,"E3.0.79.6"),sQuery(id+"F0.wireOp",EDGE,"E3.0.79.7"),sQuery(id+"F0.wireOp",EDGE,"E3.0.79.8"),sQuery(id+"F0.wireOp",EDGE,"E3.0.79.9"),sQuery(id+"F0.wireOp",EDGE,"E3.0.79.10"),sQuery(id+"F0.wireOp",EDGE,"E3.0.79.11"),sQuery(id+"F0.wireOp",EDGE,"E3.0.80.0"),sQuery(id+"F0.wireOp",EDGE,"E3.0.80.1"),sQuery(id+"F0.wireOp",EDGE,"E3.0.80.2"),sQuery(id+"F0.wireOp",EDGE,"E3.0.80.3"),sQuery(id+"F0.wireOp",EDGE,"E3.0.80.4"),sQuery(id+"F0.wireOp",EDGE,"E3.0.80.5"),sQuery(id+"F0.wireOp",EDGE,"E3.0.80.6"),sQuery(id+"F0.wireOp",EDGE,"E3.0.80.7"),sQuery(id+"F0.wireOp",EDGE,"E3.0.80.8"),sQuery(id+"F0.wireOp",EDGE,"E3.0.80.9"),sQuery(id+"F0.wireOp",EDGE,"E3.0.80.10"),sQuery(id+"F0.wireOp",EDGE,"E3.0.80.11"),sQuery(id+"F0.wireOp",EDGE,"E3.0.81.0"),sQuery(id+"F0.wireOp",EDGE,"E3.0.81.1"),sQuery(id+"F0.wireOp",EDGE,"E3.0.81.2"),sQuery(id+"F0.wireOp",EDGE,"E3.0.81.3"),sQuery(id+"F0.wireOp",EDGE,"E3.0.81.4"),sQuery(id+"F0.wireOp",EDGE,"E3.0.81.5"),sQuery(id+"F0.wireOp",EDGE,"E3.0.81.6"),sQuery(id+"F0.wireOp",EDGE,"E3.0.81.7"),sQuery(id+"F0.wireOp",EDGE,"E3.0.81.8"),sQuery(id+"F0.wireOp",EDGE,"E3.0.81.9"),sQuery(id+"F0.wireOp",EDGE,"E3.0.81.10"),sQuery(id+"F0.wireOp",EDGE,"E3.0.81.11"),sQuery(id+"F0.wireOp",EDGE,"E3.0.82.0"),sQuery(id+"F0.wireOp",EDGE,"E3.0.82.1"),sQuery(id+"F0.wireOp",EDGE,"E3.0.82.2"),sQuery(id+"F0.wireOp",EDGE,"E3.0.82.3"),sQuery(id+"F0.wireOp",EDGE,"E3.0.82.4"),sQuery(id+"F0.wireOp",EDGE,"E3.0.82.5"),sQuery(id+"F0.wireOp",EDGE,"E3.0.82.6"),sQuery(id+"F0.wireOp",EDGE,"E3.0.82.7"),sQuery(id+"F0.wireOp",EDGE,"E3.0.82.8"),sQuery(id+"F0.wireOp",EDGE,"E3.0.82.9"),sQuery(id+"F0.wireOp",EDGE,"E3.0.82.10"),sQuery(id+"F0.wireOp",EDGE,"E3.0.82.11"),sQuery(id+"F0.wireOp",EDGE,"E3.0.83.0"),sQuery(id+"F0.wireOp",EDGE,"E3.0.83.1"),sQuery(id+"F0.wireOp",EDGE,"E3.0.83.2"),sQuery(id+"F0.wireOp",EDGE,"E3.0.83.3"),sQuery(id+"F0.wireOp",EDGE,"E3.0.83.4"),sQuery(id+"F0.wireOp",EDGE,"E3.0.83.5"),sQuery(id+"F0.wireOp",EDGE,"E3.0.83.6"),sQuery(id+"F0.wireOp",EDGE,"E3.0.83.7"),sQuery(id+"F0.wireOp",EDGE,"E3.0.83.8"),sQuery(id+"F0.wireOp",EDGE,"E3.0.83.9"),sQuery(id+"F0.wireOp",EDGE,"E3.0.83.10"),sQuery(id+"F0.wireOp",EDGE,"E3.0.83.11"),sQuery(id+"F0.wireOp",EDGE,"E3.0.84.0"),sQuery(id+"F0.wireOp",EDGE,"E3.0.84.1"),sQuery(id+"F0.wireOp",EDGE,"E3.0.84.2"),sQuery(id+"F0.wireOp",EDGE,"E3.0.84.3"),sQuery(id+"F0.wireOp",EDGE,"E3.0.84.4"),sQuery(id+"F0.wireOp",EDGE,"E3.0.84.5"),sQuery(id+"F0.wireOp",EDGE,"E3.0.84.6"),sQuery(id+"F0.wireOp",EDGE,"E3.0.84.7"),sQuery(id+"F0.wireOp",EDGE,"E3.0.84.8"),sQuery(id+"F0.wireOp",EDGE,"E3.0.84.9"),sQuery(id+"F0.wireOp",EDGE,"E3.0.84.10"),sQuery(id+"F0.wireOp",EDGE,"E3.0.84.11"),sQuery(id+"F0.wireOp",EDGE,"E3.0.85.0"),sQuery(id+"F0.wireOp",EDGE,"E3.0.85.1"),sQuery(id+"F0.wireOp",EDGE,"E3.0.85.2"),sQuery(id+"F0.wireOp",EDGE,"E3.0.85.3"),sQuery(id+"F0.wireOp",EDGE,"E3.0.85.4"),sQuery(id+"F0.wireOp",EDGE,"E3.0.85.5"),sQuery(id+"F0.wireOp",EDGE,"E3.0.85.6"),sQuery(id+"F0.wireOp",EDGE,"E3.0.85.7"),sQuery(id+"F0.wireOp",EDGE,"E3.0.85.8"),sQuery(id+"F0.wireOp",EDGE,"E3.0.85.9"),sQuery(id+"F0.wireOp",EDGE,"E3.0.85.10"),sQuery(id+"F0.wireOp",EDGE,"E3.0.85.11"),sQuery(id+"F0.wireOp",EDGE,"E3.0.86.0"),sQuery(id+"F0.wireOp",EDGE,"E3.0.86.1"),sQuery(id+"F0.wireOp",EDGE,"E3.0.86.2"),sQuery(id+"F0.wireOp",EDGE,"E3.0.86.3"),sQuery(id+"F0.wireOp",EDGE,"E3.0.86.4"),sQuery(id+"F0.wireOp",EDGE,"E3.0.86.5"),sQuery(id+"F0.wireOp",EDGE,"E3.0.86.6"),sQuery(id+"F0.wireOp",EDGE,"E3.0.86.7"),sQuery(id+"F0.wireOp",EDGE,"E3.0.86.8"),sQuery(id+"F0.wireOp",EDGE,"E3.0.86.9"),sQuery(id+"F0.wireOp",EDGE,"E3.0.86.10"),sQuery(id+"F0.wireOp",EDGE,"E3.0.86.11"),sQuery(id+"F0.wireOp",EDGE,"E3.0.87.0"),sQuery(id+"F0.wireOp",EDGE,"E3.0.87.1"),sQuery(id+"F0.wireOp",EDGE,"E3.0.87.2"),sQuery(id+"F0.wireOp",EDGE,"E3.0.87.3"),sQuery(id+"F0.wireOp",EDGE,"E3.0.87.4"),sQuery(id+"F0.wireOp",EDGE,"E3.0.87.5"),sQuery(id+"F0.wireOp",EDGE,"E3.0.87.6"),sQuery(id+"F0.wireOp",EDGE,"E3.0.87.7"),sQuery(id+"F0.wireOp",EDGE,"E3.0.87.8"),sQuery(id+"F0.wireOp",EDGE,"E3.0.87.9"),sQuery(id+"F0.wireOp",EDGE,"E3.0.87.10"),sQuery(id+"F0.wireOp",EDGE,"E3.0.87.11"),sQuery(id+"F0.wireOp",EDGE,"E3.0.88.0"),sQuery(id+"F0.wireOp",EDGE,"E3.0.88.1"),sQuery(id+"F0.wireOp",EDGE,"E3.0.88.2"),sQuery(id+"F0.wireOp",EDGE,"E3.0.88.3"),sQuery(id+"F0.wireOp",EDGE,"E3.0.88.4"),sQuery(id+"F0.wireOp",EDGE,"E3.0.88.5"),sQuery(id+"F0.wireOp",EDGE,"E3.0.88.6"),sQuery(id+"F0.wireOp",EDGE,"E3.0.88.7"),sQuery(id+"F0.wireOp",EDGE,"E3.0.88.8"),sQuery(id+"F0.wireOp",EDGE,"E3.0.88.9"),sQuery(id+"F0.wireOp",EDGE,"E3.0.88.10"),sQuery(id+"F0.wireOp",EDGE,"E3.0.88.11"),sQuery(id+"F0.wireOp",EDGE,"E3.0.89.0"),sQuery(id+"F0.wireOp",EDGE,"E3.0.89.1"),sQuery(id+"F0.wireOp",EDGE,"E3.0.89.2"),sQuery(id+"F0.wireOp",EDGE,"E3.0.89.3"),sQuery(id+"F0.wireOp",EDGE,"E3.0.89.4"),sQuery(id+"F0.wireOp",EDGE,"E3.0.89.5"),sQuery(id+"F0.wireOp",EDGE,"E3.0.89.6"),sQuery(id+"F0.wireOp",EDGE,"E3.0.89.7"),sQuery(id+"F0.wireOp",EDGE,"E3.0.89.8"),sQuery(id+"F0.wireOp",EDGE,"E3.0.89.9"),sQuery(id+"F0.wireOp",EDGE,"E3.0.89.10"),sQuery(id+"F0.wireOp",EDGE,"E3.0.89.11"),sQuery(id+"F0.wireOp",EDGE,"E3.0.90.0"),sQuery(id+"F0.wireOp",EDGE,"E3.0.90.1"),sQuery(id+"F0.wireOp",EDGE,"E3.0.90.2"),sQuery(id+"F0.wireOp",EDGE,"E3.0.90.3"),sQuery(id+"F0.wireOp",EDGE,"E3.0.90.4"),sQuery(id+"F0.wireOp",EDGE,"E3.0.90.5"),sQuery(id+"F0.wireOp",EDGE,"E3.0.90.6"),sQuery(id+"F0.wireOp",EDGE,"E3.0.90.7"),sQuery(id+"F0.wireOp",EDGE,"E3.0.90.8"),sQuery(id+"F0.wireOp",EDGE,"E3.0.90.9"),sQuery(id+"F0.wireOp",EDGE,"E3.0.90.10"),sQuery(id+"F0.wireOp",EDGE,"E3.0.90.11"),sQuery(id+"F0.wireOp",EDGE,"E3.0.91.0"),sQuery(id+"F0.wireOp",EDGE,"E3.0.91.1"),sQuery(id+"F0.wireOp",EDGE,"E3.0.91.2"),sQuery(id+"F0.wireOp",EDGE,"E3.0.91.3"),sQuery(id+"F0.wireOp",EDGE,"E3.0.91.4"),sQuery(id+"F0.wireOp",EDGE,"E3.0.91.5"),sQuery(id+"F0.wireOp",EDGE,"E3.0.91.6"),sQuery(id+"F0.wireOp",EDGE,"E3.0.91.7"),sQuery(id+"F0.wireOp",EDGE,"E3.0.91.8"),sQuery(id+"F0.wireOp",EDGE,"E3.0.91.9"),sQuery(id+"F0.wireOp",EDGE,"E3.0.91.10"),sQuery(id+"F0.wireOp",EDGE,"E3.0.91.11"),sQuery(id+"F0.wireOp",EDGE,"E3.0.92.0"),sQuery(id+"F0.wireOp",EDGE,"E3.0.92.1"),sQuery(id+"F0.wireOp",EDGE,"E3.0.92.2"),sQuery(id+"F0.wireOp",EDGE,"E3.0.92.3"),sQuery(id+"F0.wireOp",EDGE,"E3.0.92.4"),sQuery(id+"F0.wireOp",EDGE,"E3.0.92.5"),sQuery(id+"F0.wireOp",EDGE,"E3.0.92.6"),sQuery(id+"F0.wireOp",EDGE,"E3.0.92.7"),sQuery(id+"F0.wireOp",EDGE,"E3.0.92.8"),sQuery(id+"F0.wireOp",EDGE,"E3.0.92.9"),sQuery(id+"F0.wireOp",EDGE,"E3.0.92.10"),sQuery(id+"F0.wireOp",EDGE,"E3.0.92.11"),sQuery(id+"F0.wireOp",EDGE,"E3.0.93.0"),sQuery(id+"F0.wireOp",EDGE,"E3.0.93.1"),sQuery(id+"F0.wireOp",EDGE,"E3.0.93.2"),sQuery(id+"F0.wireOp",EDGE,"E3.0.93.3"),sQuery(id+"F0.wireOp",EDGE,"E3.0.93.4"),sQuery(id+"F0.wireOp",EDGE,"E3.0.93.5"),sQuery(id+"F0.wireOp",EDGE,"E3.0.93.6"),sQuery(id+"F0.wireOp",EDGE,"E3.0.93.7"),sQuery(id+"F0.wireOp",EDGE,"E3.0.93.8"),sQuery(id+"F0.wireOp",EDGE,"E3.0.93.9"),sQuery(id+"F0.wireOp",EDGE,"E3.0.93.10"),sQuery(id+"F0.wireOp",EDGE,"E3.0.93.11"),sQuery(id+"F0.wireOp",EDGE,"E3.0.94.0"),sQuery(id+"F0.wireOp",EDGE,"E3.0.94.1"),sQuery(id+"F0.wireOp",EDGE,"E3.0.94.2"),sQuery(id+"F0.wireOp",EDGE,"E3.0.94.3"),sQuery(id+"F0.wireOp",EDGE,"E3.0.94.4"),sQuery(id+"F0.wireOp",EDGE,"E3.0.94.5"),sQuery(id+"F0.wireOp",EDGE,"E3.0.94.6"),sQuery(id+"F0.wireOp",EDGE,"E3.0.94.7"),sQuery(id+"F0.wireOp",EDGE,"E3.0.94.8"),sQuery(id+"F0.wireOp",EDGE,"E3.0.94.9"),sQuery(id+"F0.wireOp",EDGE,"E3.0.94.10"),sQuery(id+"F0.wireOp",EDGE,"E3.0.94.11"),sQuery(id+"F0.wireOp",EDGE,"E3.0.95.0"),sQuery(id+"F0.wireOp",EDGE,"E3.0.95.1"),sQuery(id+"F0.wireOp",EDGE,"E3.0.95.2"),sQuery(id+"F0.wireOp",EDGE,"E3.0.95.3"),sQuery(id+"F0.wireOp",EDGE,"E3.0.95.4"),sQuery(id+"F0.wireOp",EDGE,"E3.0.95.5"),sQuery(id+"F0.wireOp",EDGE,"E3.0.95.6"),sQuery(id+"F0.wireOp",EDGE,"E3.0.95.7"),sQuery(id+"F0.wireOp",EDGE,"E3.0.95.8"),sQuery(id+"F0.wireOp",EDGE,"E3.0.95.9"),sQuery(id+"F0.wireOp",EDGE,"E3.0.95.10"),sQuery(id+"F0.wireOp",EDGE,"E3.0.95.11"),sQuery(id+"F0.wireOp",EDGE,"E3.0.96.0"),sQuery(id+"F0.wireOp",EDGE,"E3.0.96.1"),sQuery(id+"F0.wireOp",EDGE,"E3.0.96.2"),sQuery(id+"F0.wireOp",EDGE,"E3.0.96.3"),sQuery(id+"F0.wireOp",EDGE,"E3.0.96.4"),sQuery(id+"F0.wireOp",EDGE,"E3.0.96.5"),sQuery(id+"F0.wireOp",EDGE,"E3.0.96.6"),sQuery(id+"F0.wireOp",EDGE,"E3.0.96.7"),sQuery(id+"F0.wireOp",EDGE,"E3.0.96.8"),sQuery(id+"F0.wireOp",EDGE,"E3.0.96.9"),sQuery(id+"F0.wireOp",EDGE,"E3.0.96.10"),sQuery(id+"F0.wireOp",EDGE,"E3.0.96.11"),sQuery(id+"F0.wireOp",EDGE,"E3.0.97.0"),sQuery(id+"F0.wireOp",EDGE,"E3.0.97.1"),sQuery(id+"F0.wireOp",EDGE,"E3.0.97.2"),sQuery(id+"F0.wireOp",EDGE,"E3.0.97.3"),sQuery(id+"F0.wireOp",EDGE,"E3.0.97.4"),sQuery(id+"F0.wireOp",EDGE,"E3.0.97.5"),sQuery(id+"F0.wireOp",EDGE,"E3.0.97.6"),sQuery(id+"F0.wireOp",EDGE,"E3.0.97.7"),sQuery(id+"F0.wireOp",EDGE,"E3.0.97.8"),sQuery(id+"F0.wireOp",EDGE,"E3.0.97.9"),sQuery(id+"F0.wireOp",EDGE,"E3.0.97.10"),sQuery(id+"F0.wireOp",EDGE,"E3.0.97.11"),sQuery(id+"F0.wireOp",EDGE,"E3.0.98.0"),sQuery(id+"F0.wireOp",EDGE,"E3.0.98.1"),sQuery(id+"F0.wireOp",EDGE,"E3.0.98.2"),sQuery(id+"F0.wireOp",EDGE,"E3.0.98.3"),sQuery(id+"F0.wireOp",EDGE,"E3.0.98.4"),sQuery(id+"F0.wireOp",EDGE,"E3.0.98.5"),sQuery(id+"F0.wireOp",EDGE,"E3.0.98.6"),sQuery(id+"F0.wireOp",EDGE,"E3.0.98.7"),sQuery(id+"F0.wireOp",EDGE,"E3.0.98.8"),sQuery(id+"F0.wireOp",EDGE,"E3.0.98.9"),sQuery(id+"F0.wireOp",EDGE,"E3.0.98.10"),sQuery(id+"F0.wireOp",EDGE,"E3.0.98.11"),sQuery(id+"F0.wireOp",EDGE,"E3.0.99.0"),sQuery(id+"F0.wireOp",EDGE,"E3.0.99.1"),sQuery(id+"F0.wireOp",EDGE,"E3.0.99.2"),sQuery(id+"F0.wireOp",EDGE,"E3.0.99.3"),sQuery(id+"F0.wireOp",EDGE,"E3.0.99.4"),sQuery(id+"F0.wireOp",EDGE,"E3.0.99.5"),sQuery(id+"F0.wireOp",EDGE,"E3.0.99.6"),sQuery(id+"F0.wireOp",EDGE,"E3.0.99.7"),sQuery(id+"F0.wireOp",EDGE,"E3.0.99.8"),sQuery(id+"F0.wireOp",EDGE,"E3.0.99.9"),sQuery(id+"F0.wireOp",EDGE,"E3.0.99.10"),sQuery(id+"F0.wireOp",EDGE,"E3.0.99.11"),sQuery(id+"F0.wireOp",EDGE,"E4.0.0.12"),sQuery(id+"F0.wireOp",EDGE,"E4.0.1.12"),sQuery(id+"F0.wireOp",EDGE,"E4.0.2.12"),sQuery(id+"F0.wireOp",EDGE,"E4.0.3.12"),sQuery(id+"F0.wireOp",EDGE,"E4.0.4.12"),sQuery(id+"F0.wireOp",EDGE,"E4.0.5.12"),sQuery(id+"F0.wireOp",EDGE,"E4.0.6.12"),sQuery(id+"F0.wireOp",EDGE,"E4.0.7.12"),sQuery(id+"F0.wireOp",EDGE,"E4.0.8.12"),sQuery(id+"F0.wireOp",EDGE,"E4.0.9.12"),sQuery(id+"F0.wireOp",EDGE,"E4.0.10.12"),sQuery(id+"F0.wireOp",EDGE,"E4.0.11.12"),sQuery(id+"F0.wireOp",EDGE,"E4.0.12.12"),sQuery(id+"F0.wireOp",EDGE,"E4.0.13.12"),sQuery(id+"F0.wireOp",EDGE,"E4.0.14.12"),sQuery(id+"F0.wireOp",EDGE,"E4.0.15.12"),sQuery(id+"F0.wireOp",EDGE,"E4.0.16.12"),sQuery(id+"F0.wireOp",EDGE,"E4.0.17.12"),sQuery(id+"F0.wireOp",EDGE,"E4.0.18.12"),sQuery(id+"F0.wireOp",EDGE,"E4.0.19.12"),sQuery(id+"F0.wireOp",EDGE,"E4.0.20.12"),sQuery(id+"F0.wireOp",EDGE,"E4.0.21.12"),sQuery(id+"F0.wireOp",EDGE,"E4.0.22.12"),sQuery(id+"F0.wireOp",EDGE,"E4.0.23.12"),sQuery(id+"F0.wireOp",EDGE,"E4.0.24.12"),sQuery(id+"F0.wireOp",EDGE,"E4.0.25.12"),sQuery(id+"F0.wireOp",EDGE,"E4.0.26.12"),sQuery(id+"F0.wireOp",EDGE,"E4.0.27.12"),sQuery(id+"F0.wireOp",EDGE,"E4.0.28.12"),sQuery(id+"F0.wireOp",EDGE,"E4.0.29.12"),sQuery(id+"F0.wireOp",EDGE,"E4.0.30.12"),sQuery(id+"F0.wireOp",EDGE,"E4.0.31.12"),sQuery(id+"F0.wireOp",EDGE,"E4.0.32.12"),sQuery(id+"F0.wireOp",EDGE,"E4.0.33.12"),sQuery(id+"F0.wireOp",EDGE,"E4.0.34.12"),sQuery(id+"F0.wireOp",EDGE,"E4.0.35.12"),sQuery(id+"F0.wireOp",EDGE,"E4.0.36.12"),sQuery(id+"F0.wireOp",EDGE,"E4.0.37.12"),sQuery(id+"F0.wireOp",EDGE,"E4.0.38.12"),sQuery(id+"F0.wireOp",EDGE,"E4.0.39.12"),sQuery(id+"F0.wireOp",EDGE,"E4.0.40.12"),sQuery(id+"F0.wireOp",EDGE,"E4.0.41.12"),sQuery(id+"F0.wireOp",EDGE,"E4.0.42.12"),sQuery(id+"F0.wireOp",EDGE,"E4.0.43.12"),sQuery(id+"F0.wireOp",EDGE,"E4.0.44.12"),sQuery(id+"F0.wireOp",EDGE,"E4.0.45.12"),sQuery(id+"F0.wireOp",EDGE,"E4.0.46.12"),sQuery(id+"F0.wireOp",EDGE,"E4.0.47.12"),sQuery(id+"F0.wireOp",EDGE,"E4.0.48.12"),sQuery(id+"F0.wireOp",EDGE,"E4.0.49.12"),sQuery(id+"F0.wireOp",EDGE,"E4.0.50.12"),sQuery(id+"F0.wireOp",EDGE,"E4.0.51.12"),sQuery(id+"F0.wireOp",EDGE,"E4.0.52.12"),sQuery(id+"F0.wireOp",EDGE,"E4.0.53.12"),sQuery(id+"F0.wireOp",EDGE,"E4.0.54.12"),sQuery(id+"F0.wireOp",EDGE,"E4.0.55.12"),sQuery(id+"F0.wireOp",EDGE,"E4.0.56.12"),sQuery(id+"F0.wireOp",EDGE,"E4.0.57.12"),sQuery(id+"F0.wireOp",EDGE,"E4.0.58.12"),sQuery(id+"F0.wireOp",EDGE,"E4.0.59.12"),sQuery(id+"F0.wireOp",EDGE,"E4.0.60.12"),sQuery(id+"F0.wireOp",EDGE,"E4.0.61.12"),sQuery(id+"F0.wireOp",EDGE,"E4.0.62.12"),sQuery(id+"F0.wireOp",EDGE,"E4.0.63.12"),sQuery(id+"F0.wireOp",EDGE,"E4.0.64.12"),sQuery(id+"F0.wireOp",EDGE,"E4.0.65.12"),sQuery(id+"F0.wireOp",EDGE,"E4.0.66.12"),sQuery(id+"F0.wireOp",EDGE,"E4.0.67.12"),sQuery(id+"F0.wireOp",EDGE,"E4.0.68.12"),sQuery(id+"F0.wireOp",EDGE,"E4.0.69.12"),sQuery(id+"F0.wireOp",EDGE,"E4.0.70.12"),sQuery(id+"F0.wireOp",EDGE,"E4.0.71.12"),sQuery(id+"F0.wireOp",EDGE,"E4.0.72.12"),sQuery(id+"F0.wireOp",EDGE,"E4.0.73.12"),sQuery(id+"F0.wireOp",EDGE,"E4.0.74.12"),sQuery(id+"F0.wireOp",EDGE,"E4.0.75.12"),sQuery(id+"F0.wireOp",EDGE,"E4.0.76.12"),sQuery(id+"F0.wireOp",EDGE,"E4.0.77.12"),sQuery(id+"F0.wireOp",EDGE,"E4.0.78.12"),sQuery(id+"F0.wireOp",EDGE,"E4.0.79.12"),sQuery(id+"F0.wireOp",EDGE,"E4.0.80.12"),sQuery(id+"F0.wireOp",EDGE,"E4.0.81.12"),sQuery(id+"F0.wireOp",EDGE,"E4.0.82.12"),sQuery(id+"F0.wireOp",EDGE,"E4.0.83.12"),sQuery(id+"F0.wireOp",EDGE,"E4.0.84.12"),sQuery(id+"F0.wireOp",EDGE,"E4.0.85.12"),sQuery(id+"F0.wireOp",EDGE,"E4.0.86.12"),sQuery(id+"F0.wireOp",EDGE,"E4.0.87.12"),sQuery(id+"F0.wireOp",EDGE,"E4.0.88.12"),sQuery(id+"F0.wireOp",EDGE,"E4.0.89.12"),sQuery(id+"F0.wireOp",EDGE,"E4.0.90.12"),sQuery(id+"F0.wireOp",EDGE,"E4.0.91.12"),sQuery(id+"F0.wireOp",EDGE,"E4.0.92.12"),sQuery(id+"F0.wireOp",EDGE,"E4.0.93.12"),sQuery(id+"F0.wireOp",EDGE,"E4.0.94.12"),sQuery(id+"F0.wireOp",EDGE,"E4.0.95.12"),sQuery(id+"F0.wireOp",EDGE,"E4.0.96.12"),sQuery(id+"F0.wireOp",EDGE,"E4.0.97.12"),sQuery(id+"F0.wireOp",EDGE,"E4.0.98.12"),sQuery(id+"F0.wireOp",EDGE,"E4.0.99.12")])],"isStart":false});
            var sketch = newSketch(context, id + "F2", { "sketchPlane" : qUnion([Q0])});
            skCircle(sketch, "E5", {"center": v(53.37, 11.24) * mm, "radius": 7.5 * mm});
            skSolve(sketch);
        }
        {
            var Q0;
            Q0 = qSketchRegion(id + "F2", true);
            extrude(context, id + "F3", {"entities" : qUnion([Q0]), "operationType" : NewBodyOperationType.REMOVE, "oppositeDirection" : true, "depth" : 1 * mm});
        }
        {
            var Q0;
            Q0=qCreatedBy(makeId("Front.planeOp"),FACE);
            var sketch = newSketch(context, id + "F4", { "sketchPlane" : qUnion([Q0])});
            skCircle(sketch, "E6", {"center": v(53.35, 11.18) * mm, "radius": 7.5 * mm});
            skCircle(sketch, "E7", {"center": v(53.35, 11.18) * mm, "radius": 4.93 * mm});
            skSolve(sketch);
        }
        {
            var Q0;
            Q0 = qSketchRegion(id + "F4", true);
            extrude(context, id + "F5", {"entities" : qUnion([Q0]), "depth" : 1 * mm});
        }
    });
